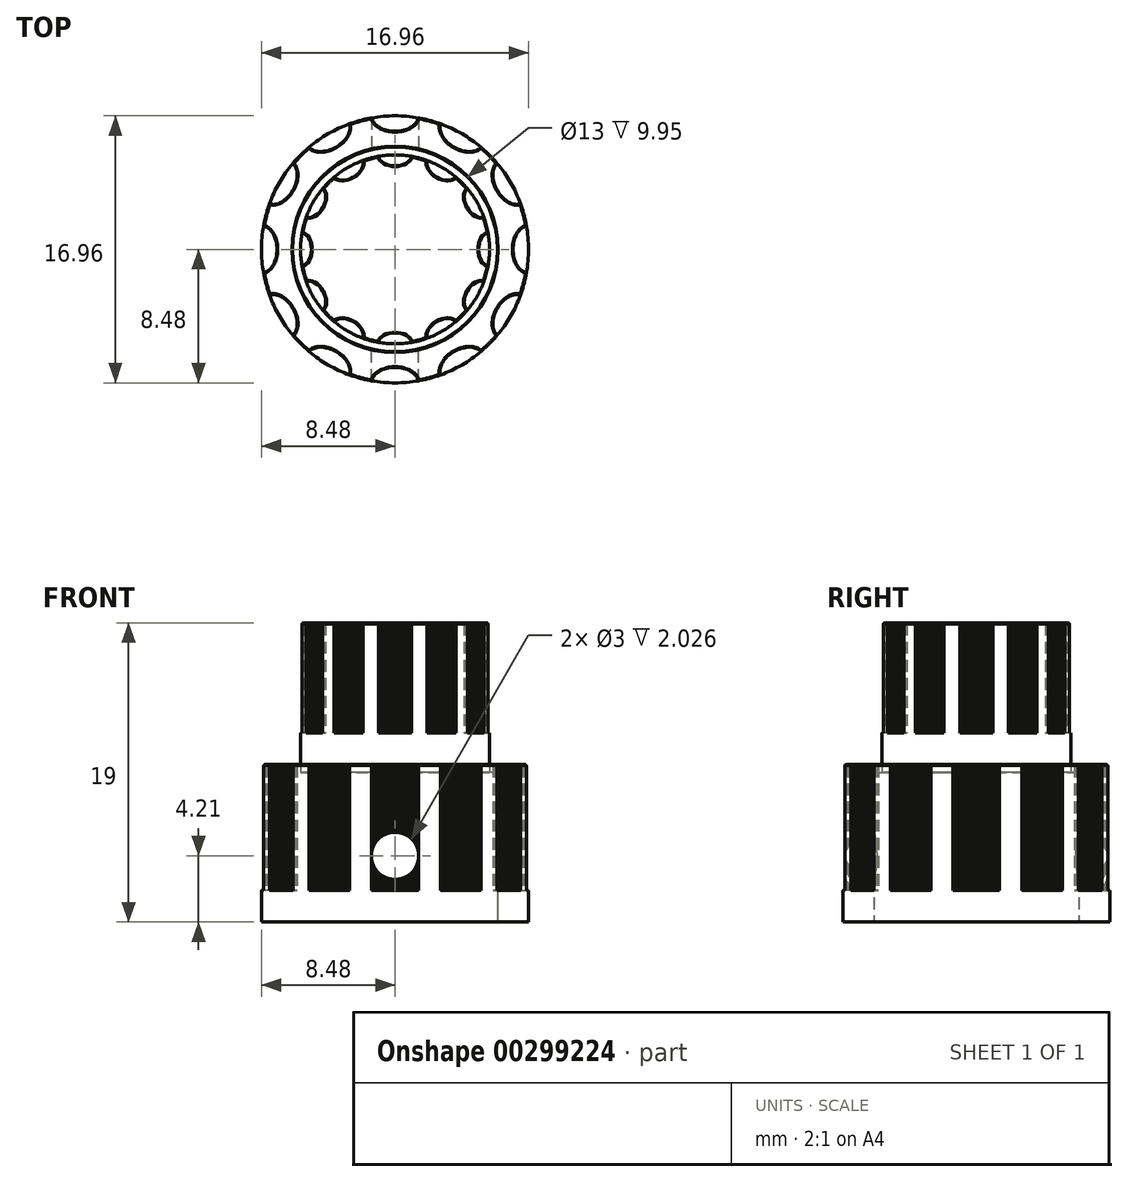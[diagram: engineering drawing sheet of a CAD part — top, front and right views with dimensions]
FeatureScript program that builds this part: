
annotation { "Feature Type Name" : "Feature", "Feature Type Description" : "" }
export const myFeature = defineFeature(function(context is Context, id is Id, definition is map)
    precondition{}
    {
        {
            var Q0;
            Q0=qCreatedBy(makeId("Top.planeOp"),FACE);
            var sketch = newSketch(context, id + "F0", { "sketchPlane" : qUnion([Q0])});
            skLineSegment(sketch, "E0", {"start": v(1.05, 5.92) * mm, "end": v(1.03, 5.86) * mm});
            skLineSegment(sketch, "E1", {"start": v(1.03, 5.86) * mm, "end": v(1, 5.8) * mm});
            skLineSegment(sketch, "E2", {"start": v(1, 5.8) * mm, "end": v(0.98, 5.74) * mm});
            skLineSegment(sketch, "E3", {"start": v(0.98, 5.74) * mm, "end": v(0.93, 5.68) * mm});
            skLineSegment(sketch, "E4", {"start": v(0.93, 5.68) * mm, "end": v(0.83, 5.57) * mm});
            skLineSegment(sketch, "E5", {"start": v(0.83, 5.57) * mm, "end": v(0.7, 5.48) * mm});
            skLineSegment(sketch, "E6", {"start": v(0.7, 5.48) * mm, "end": v(0.55, 5.4) * mm});
            skLineSegment(sketch, "E7", {"start": v(0.55, 5.4) * mm, "end": v(0.38, 5.35) * mm});
            skLineSegment(sketch, "E8", {"start": v(0.38, 5.35) * mm, "end": v(0.2, 5.32) * mm});
            skLineSegment(sketch, "E9", {"start": v(0.2, 5.32) * mm, "end": v(0, 5.3) * mm});
            skLineSegment(sketch, "E10", {"start": v(0, 5.3) * mm, "end": v(-0.2, 5.32) * mm});
            skLineSegment(sketch, "E11", {"start": v(-0.2, 5.32) * mm, "end": v(-0.38, 5.35) * mm});
            skLineSegment(sketch, "E12", {"start": v(-0.38, 5.35) * mm, "end": v(-0.55, 5.4) * mm});
            skLineSegment(sketch, "E13", {"start": v(-0.55, 5.4) * mm, "end": v(-0.7, 5.48) * mm});
            skLineSegment(sketch, "E14", {"start": v(-0.7, 5.48) * mm, "end": v(-0.83, 5.57) * mm});
            skLineSegment(sketch, "E15", {"start": v(-0.83, 5.57) * mm, "end": v(-0.93, 5.68) * mm});
            skLineSegment(sketch, "E16", {"start": v(-0.93, 5.68) * mm, "end": v(-0.98, 5.74) * mm});
            skLineSegment(sketch, "E17", {"start": v(-0.98, 5.74) * mm, "end": v(-1, 5.8) * mm});
            skLineSegment(sketch, "E18", {"start": v(-1, 5.8) * mm, "end": v(-1.03, 5.86) * mm});
            skLineSegment(sketch, "E19", {"start": v(-1.03, 5.86) * mm, "end": v(-1.05, 5.92) * mm});
            skLineSegment(sketch, "E20", {"start": v(3.87, 4.6) * mm, "end": v(3.82, 4.55) * mm});
            skLineSegment(sketch, "E21", {"start": v(3.82, 4.55) * mm, "end": v(3.77, 4.51) * mm});
            skLineSegment(sketch, "E22", {"start": v(3.77, 4.51) * mm, "end": v(3.7, 4.48) * mm});
            skLineSegment(sketch, "E23", {"start": v(3.7, 4.48) * mm, "end": v(3.64, 4.45) * mm});
            skLineSegment(sketch, "E24", {"start": v(3.64, 4.45) * mm, "end": v(3.5, 4.41) * mm});
            skLineSegment(sketch, "E25", {"start": v(3.5, 4.41) * mm, "end": v(3.35, 4.4) * mm});
            skLineSegment(sketch, "E26", {"start": v(3.35, 4.4) * mm, "end": v(3.18, 4.4) * mm});
            skLineSegment(sketch, "E27", {"start": v(3.18, 4.4) * mm, "end": v(3, 4.45) * mm});
            skLineSegment(sketch, "E28", {"start": v(3, 4.45) * mm, "end": v(2.83, 4.5) * mm});
            skLineSegment(sketch, "E29", {"start": v(2.83, 4.5) * mm, "end": v(2.65, 4.6) * mm});
            skLineSegment(sketch, "E30", {"start": v(2.65, 4.6) * mm, "end": v(2.49, 4.7) * mm});
            skLineSegment(sketch, "E31", {"start": v(2.49, 4.7) * mm, "end": v(2.35, 4.83) * mm});
            skLineSegment(sketch, "E32", {"start": v(2.35, 4.83) * mm, "end": v(2.23, 4.96) * mm});
            skLineSegment(sketch, "E33", {"start": v(2.23, 4.96) * mm, "end": v(2.13, 5.1) * mm});
            skLineSegment(sketch, "E34", {"start": v(2.13, 5.1) * mm, "end": v(2.07, 5.24) * mm});
            skLineSegment(sketch, "E35", {"start": v(2.07, 5.24) * mm, "end": v(2.03, 5.38) * mm});
            skLineSegment(sketch, "E36", {"start": v(2.03, 5.38) * mm, "end": v(2.02, 5.45) * mm});
            skLineSegment(sketch, "E37", {"start": v(2.02, 5.45) * mm, "end": v(2.02, 5.52) * mm});
            skLineSegment(sketch, "E38", {"start": v(2.02, 5.52) * mm, "end": v(2.03, 5.59) * mm});
            skLineSegment(sketch, "E39", {"start": v(2.03, 5.59) * mm, "end": v(2.05, 5.65) * mm});
            skLineSegment(sketch, "E40", {"start": v(-3.87, 4.6) * mm, "end": v(-3.82, 4.55) * mm});
            skLineSegment(sketch, "E41", {"start": v(-3.82, 4.55) * mm, "end": v(-3.77, 4.51) * mm});
            skLineSegment(sketch, "E42", {"start": v(-3.77, 4.51) * mm, "end": v(-3.7, 4.48) * mm});
            skLineSegment(sketch, "E43", {"start": v(-3.7, 4.48) * mm, "end": v(-3.64, 4.45) * mm});
            skLineSegment(sketch, "E44", {"start": v(-3.64, 4.45) * mm, "end": v(-3.5, 4.41) * mm});
            skLineSegment(sketch, "E45", {"start": v(-3.5, 4.41) * mm, "end": v(-3.35, 4.4) * mm});
            skLineSegment(sketch, "E46", {"start": v(-3.35, 4.4) * mm, "end": v(-3.18, 4.4) * mm});
            skLineSegment(sketch, "E47", {"start": v(-3.18, 4.4) * mm, "end": v(-3, 4.45) * mm});
            skLineSegment(sketch, "E48", {"start": v(-3, 4.45) * mm, "end": v(-2.83, 4.5) * mm});
            skLineSegment(sketch, "E49", {"start": v(-2.83, 4.5) * mm, "end": v(-2.65, 4.6) * mm});
            skLineSegment(sketch, "E50", {"start": v(-2.65, 4.6) * mm, "end": v(-2.49, 4.7) * mm});
            skLineSegment(sketch, "E51", {"start": v(-2.49, 4.7) * mm, "end": v(-2.35, 4.83) * mm});
            skLineSegment(sketch, "E52", {"start": v(-2.35, 4.83) * mm, "end": v(-2.23, 4.96) * mm});
            skLineSegment(sketch, "E53", {"start": v(-2.23, 4.96) * mm, "end": v(-2.13, 5.1) * mm});
            skLineSegment(sketch, "E54", {"start": v(-2.13, 5.1) * mm, "end": v(-2.07, 5.24) * mm});
            skLineSegment(sketch, "E55", {"start": v(-2.07, 5.24) * mm, "end": v(-2.03, 5.38) * mm});
            skLineSegment(sketch, "E56", {"start": v(-2.03, 5.38) * mm, "end": v(-2.02, 5.45) * mm});
            skLineSegment(sketch, "E57", {"start": v(-2.02, 5.45) * mm, "end": v(-2.02, 5.52) * mm});
            skLineSegment(sketch, "E58", {"start": v(-2.02, 5.52) * mm, "end": v(-2.03, 5.59) * mm});
            skLineSegment(sketch, "E59", {"start": v(-2.03, 5.59) * mm, "end": v(-2.05, 5.65) * mm});
            skLineSegment(sketch, "E60", {"start": v(5.65, 2.05) * mm, "end": v(5.59, 2.03) * mm});
            skLineSegment(sketch, "E61", {"start": v(5.59, 2.03) * mm, "end": v(5.52, 2.02) * mm});
            skLineSegment(sketch, "E62", {"start": v(5.52, 2.02) * mm, "end": v(5.45, 2.02) * mm});
            skLineSegment(sketch, "E63", {"start": v(5.45, 2.02) * mm, "end": v(5.38, 2.03) * mm});
            skLineSegment(sketch, "E64", {"start": v(5.38, 2.03) * mm, "end": v(5.24, 2.07) * mm});
            skLineSegment(sketch, "E65", {"start": v(5.24, 2.07) * mm, "end": v(5.1, 2.13) * mm});
            skLineSegment(sketch, "E66", {"start": v(5.1, 2.13) * mm, "end": v(4.96, 2.23) * mm});
            skLineSegment(sketch, "E67", {"start": v(4.96, 2.23) * mm, "end": v(4.83, 2.35) * mm});
            skLineSegment(sketch, "E68", {"start": v(4.83, 2.35) * mm, "end": v(4.7, 2.49) * mm});
            skLineSegment(sketch, "E69", {"start": v(4.7, 2.49) * mm, "end": v(4.6, 2.65) * mm});
            skLineSegment(sketch, "E70", {"start": v(4.6, 2.65) * mm, "end": v(4.5, 2.83) * mm});
            skLineSegment(sketch, "E71", {"start": v(4.5, 2.83) * mm, "end": v(4.45, 3) * mm});
            skLineSegment(sketch, "E72", {"start": v(4.45, 3) * mm, "end": v(4.4, 3.18) * mm});
            skLineSegment(sketch, "E73", {"start": v(4.4, 3.18) * mm, "end": v(4.4, 3.35) * mm});
            skLineSegment(sketch, "E74", {"start": v(4.4, 3.35) * mm, "end": v(4.41, 3.5) * mm});
            skLineSegment(sketch, "E75", {"start": v(4.41, 3.5) * mm, "end": v(4.45, 3.64) * mm});
            skLineSegment(sketch, "E76", {"start": v(4.45, 3.64) * mm, "end": v(4.48, 3.7) * mm});
            skLineSegment(sketch, "E77", {"start": v(4.48, 3.7) * mm, "end": v(4.51, 3.77) * mm});
            skLineSegment(sketch, "E78", {"start": v(4.51, 3.77) * mm, "end": v(4.55, 3.82) * mm});
            skLineSegment(sketch, "E79", {"start": v(4.55, 3.82) * mm, "end": v(4.6, 3.87) * mm});
            skLineSegment(sketch, "E80", {"start": v(5.92, 1.05) * mm, "end": v(5.86, 1.03) * mm});
            skLineSegment(sketch, "E81", {"start": v(5.86, 1.03) * mm, "end": v(5.8, 1) * mm});
            skLineSegment(sketch, "E82", {"start": v(5.8, 1) * mm, "end": v(5.74, 0.98) * mm});
            skLineSegment(sketch, "E83", {"start": v(5.74, 0.98) * mm, "end": v(5.68, 0.93) * mm});
            skLineSegment(sketch, "E84", {"start": v(5.68, 0.93) * mm, "end": v(5.57, 0.83) * mm});
            skLineSegment(sketch, "E85", {"start": v(5.57, 0.83) * mm, "end": v(5.48, 0.7) * mm});
            skLineSegment(sketch, "E86", {"start": v(5.48, 0.7) * mm, "end": v(5.4, 0.55) * mm});
            skLineSegment(sketch, "E87", {"start": v(5.4, 0.55) * mm, "end": v(5.35, 0.38) * mm});
            skLineSegment(sketch, "E88", {"start": v(5.35, 0.38) * mm, "end": v(5.32, 0.2) * mm});
            skLineSegment(sketch, "E89", {"start": v(5.32, 0.2) * mm, "end": v(5.3, 0) * mm});
            skLineSegment(sketch, "E90", {"start": v(5.3, 0) * mm, "end": v(5.32, -0.2) * mm});
            skLineSegment(sketch, "E91", {"start": v(5.32, -0.2) * mm, "end": v(5.35, -0.38) * mm});
            skLineSegment(sketch, "E92", {"start": v(5.35, -0.38) * mm, "end": v(5.4, -0.55) * mm});
            skLineSegment(sketch, "E93", {"start": v(5.4, -0.55) * mm, "end": v(5.48, -0.7) * mm});
            skLineSegment(sketch, "E94", {"start": v(5.48, -0.7) * mm, "end": v(5.57, -0.83) * mm});
            skLineSegment(sketch, "E95", {"start": v(5.57, -0.83) * mm, "end": v(5.68, -0.93) * mm});
            skLineSegment(sketch, "E96", {"start": v(5.68, -0.93) * mm, "end": v(5.74, -0.98) * mm});
            skLineSegment(sketch, "E97", {"start": v(5.74, -0.98) * mm, "end": v(5.8, -1) * mm});
            skLineSegment(sketch, "E98", {"start": v(5.8, -1) * mm, "end": v(5.86, -1.03) * mm});
            skLineSegment(sketch, "E99", {"start": v(5.86, -1.03) * mm, "end": v(5.92, -1.05) * mm});
            skLineSegment(sketch, "E100", {"start": v(-5.65, 2.05) * mm, "end": v(-5.59, 2.03) * mm});
            skLineSegment(sketch, "E101", {"start": v(-5.59, 2.03) * mm, "end": v(-5.52, 2.02) * mm});
            skLineSegment(sketch, "E102", {"start": v(-5.52, 2.02) * mm, "end": v(-5.45, 2.02) * mm});
            skLineSegment(sketch, "E103", {"start": v(-5.45, 2.02) * mm, "end": v(-5.38, 2.03) * mm});
            skLineSegment(sketch, "E104", {"start": v(-5.38, 2.03) * mm, "end": v(-5.24, 2.07) * mm});
            skLineSegment(sketch, "E105", {"start": v(-5.24, 2.07) * mm, "end": v(-5.1, 2.13) * mm});
            skLineSegment(sketch, "E106", {"start": v(-5.1, 2.13) * mm, "end": v(-4.96, 2.23) * mm});
            skLineSegment(sketch, "E107", {"start": v(-4.96, 2.23) * mm, "end": v(-4.83, 2.35) * mm});
            skLineSegment(sketch, "E108", {"start": v(-4.83, 2.35) * mm, "end": v(-4.7, 2.49) * mm});
            skLineSegment(sketch, "E109", {"start": v(-4.7, 2.49) * mm, "end": v(-4.6, 2.65) * mm});
            skLineSegment(sketch, "E110", {"start": v(-4.6, 2.65) * mm, "end": v(-4.5, 2.83) * mm});
            skLineSegment(sketch, "E111", {"start": v(-4.5, 2.83) * mm, "end": v(-4.45, 3) * mm});
            skLineSegment(sketch, "E112", {"start": v(-4.45, 3) * mm, "end": v(-4.4, 3.18) * mm});
            skLineSegment(sketch, "E113", {"start": v(-4.4, 3.18) * mm, "end": v(-4.4, 3.35) * mm});
            skLineSegment(sketch, "E114", {"start": v(-4.4, 3.35) * mm, "end": v(-4.41, 3.5) * mm});
            skLineSegment(sketch, "E115", {"start": v(-4.41, 3.5) * mm, "end": v(-4.45, 3.64) * mm});
            skLineSegment(sketch, "E116", {"start": v(-4.45, 3.64) * mm, "end": v(-4.48, 3.7) * mm});
            skLineSegment(sketch, "E117", {"start": v(-4.48, 3.7) * mm, "end": v(-4.51, 3.77) * mm});
            skLineSegment(sketch, "E118", {"start": v(-4.51, 3.77) * mm, "end": v(-4.55, 3.82) * mm});
            skLineSegment(sketch, "E119", {"start": v(-4.55, 3.82) * mm, "end": v(-4.6, 3.87) * mm});
            skLineSegment(sketch, "E120", {"start": v(5.65, -2.05) * mm, "end": v(5.59, -2.03) * mm});
            skLineSegment(sketch, "E121", {"start": v(5.59, -2.03) * mm, "end": v(5.52, -2.02) * mm});
            skLineSegment(sketch, "E122", {"start": v(5.52, -2.02) * mm, "end": v(5.45, -2.02) * mm});
            skLineSegment(sketch, "E123", {"start": v(5.45, -2.02) * mm, "end": v(5.38, -2.03) * mm});
            skLineSegment(sketch, "E124", {"start": v(5.38, -2.03) * mm, "end": v(5.24, -2.07) * mm});
            skLineSegment(sketch, "E125", {"start": v(5.24, -2.07) * mm, "end": v(5.1, -2.13) * mm});
            skLineSegment(sketch, "E126", {"start": v(5.1, -2.13) * mm, "end": v(4.96, -2.23) * mm});
            skLineSegment(sketch, "E127", {"start": v(4.96, -2.23) * mm, "end": v(4.83, -2.35) * mm});
            skLineSegment(sketch, "E128", {"start": v(4.83, -2.35) * mm, "end": v(4.7, -2.49) * mm});
            skLineSegment(sketch, "E129", {"start": v(4.7, -2.49) * mm, "end": v(4.6, -2.65) * mm});
            skLineSegment(sketch, "E130", {"start": v(4.6, -2.65) * mm, "end": v(4.5, -2.83) * mm});
            skLineSegment(sketch, "E131", {"start": v(4.5, -2.83) * mm, "end": v(4.45, -3) * mm});
            skLineSegment(sketch, "E132", {"start": v(4.45, -3) * mm, "end": v(4.4, -3.18) * mm});
            skLineSegment(sketch, "E133", {"start": v(4.4, -3.18) * mm, "end": v(4.4, -3.35) * mm});
            skLineSegment(sketch, "E134", {"start": v(4.4, -3.35) * mm, "end": v(4.41, -3.5) * mm});
            skLineSegment(sketch, "E135", {"start": v(4.41, -3.5) * mm, "end": v(4.45, -3.64) * mm});
            skLineSegment(sketch, "E136", {"start": v(4.45, -3.64) * mm, "end": v(4.48, -3.7) * mm});
            skLineSegment(sketch, "E137", {"start": v(4.48, -3.7) * mm, "end": v(4.51, -3.77) * mm});
            skLineSegment(sketch, "E138", {"start": v(4.51, -3.77) * mm, "end": v(4.55, -3.82) * mm});
            skLineSegment(sketch, "E139", {"start": v(4.55, -3.82) * mm, "end": v(4.6, -3.87) * mm});
            skLineSegment(sketch, "E140", {"start": v(-5.92, -1.05) * mm, "end": v(-5.86, -1.03) * mm});
            skLineSegment(sketch, "E141", {"start": v(-5.86, -1.03) * mm, "end": v(-5.8, -1) * mm});
            skLineSegment(sketch, "E142", {"start": v(-5.8, -1) * mm, "end": v(-5.74, -0.98) * mm});
            skLineSegment(sketch, "E143", {"start": v(-5.74, -0.98) * mm, "end": v(-5.68, -0.93) * mm});
            skLineSegment(sketch, "E144", {"start": v(-5.68, -0.93) * mm, "end": v(-5.57, -0.83) * mm});
            skLineSegment(sketch, "E145", {"start": v(-5.57, -0.83) * mm, "end": v(-5.48, -0.7) * mm});
            skLineSegment(sketch, "E146", {"start": v(-5.48, -0.7) * mm, "end": v(-5.4, -0.55) * mm});
            skLineSegment(sketch, "E147", {"start": v(-5.4, -0.55) * mm, "end": v(-5.35, -0.38) * mm});
            skLineSegment(sketch, "E148", {"start": v(-5.35, -0.38) * mm, "end": v(-5.32, -0.2) * mm});
            skLineSegment(sketch, "E149", {"start": v(-5.32, -0.2) * mm, "end": v(-5.3, 0) * mm});
            skLineSegment(sketch, "E150", {"start": v(-5.3, 0) * mm, "end": v(-5.32, 0.2) * mm});
            skLineSegment(sketch, "E151", {"start": v(-5.32, 0.2) * mm, "end": v(-5.35, 0.38) * mm});
            skLineSegment(sketch, "E152", {"start": v(-5.35, 0.38) * mm, "end": v(-5.4, 0.55) * mm});
            skLineSegment(sketch, "E153", {"start": v(-5.4, 0.55) * mm, "end": v(-5.48, 0.7) * mm});
            skLineSegment(sketch, "E154", {"start": v(-5.48, 0.7) * mm, "end": v(-5.57, 0.83) * mm});
            skLineSegment(sketch, "E155", {"start": v(-5.57, 0.83) * mm, "end": v(-5.68, 0.93) * mm});
            skLineSegment(sketch, "E156", {"start": v(-5.68, 0.93) * mm, "end": v(-5.74, 0.98) * mm});
            skLineSegment(sketch, "E157", {"start": v(-5.74, 0.98) * mm, "end": v(-5.8, 1) * mm});
            skLineSegment(sketch, "E158", {"start": v(-5.8, 1) * mm, "end": v(-5.86, 1.03) * mm});
            skLineSegment(sketch, "E159", {"start": v(-5.86, 1.03) * mm, "end": v(-5.92, 1.05) * mm});
            skLineSegment(sketch, "E160", {"start": v(-5.65, -2.05) * mm, "end": v(-5.59, -2.03) * mm});
            skLineSegment(sketch, "E161", {"start": v(-5.59, -2.03) * mm, "end": v(-5.52, -2.02) * mm});
            skLineSegment(sketch, "E162", {"start": v(-5.52, -2.02) * mm, "end": v(-5.45, -2.02) * mm});
            skLineSegment(sketch, "E163", {"start": v(-5.45, -2.02) * mm, "end": v(-5.38, -2.03) * mm});
            skLineSegment(sketch, "E164", {"start": v(-5.38, -2.03) * mm, "end": v(-5.24, -2.07) * mm});
            skLineSegment(sketch, "E165", {"start": v(-5.24, -2.07) * mm, "end": v(-5.1, -2.13) * mm});
            skLineSegment(sketch, "E166", {"start": v(-5.1, -2.13) * mm, "end": v(-4.96, -2.23) * mm});
            skLineSegment(sketch, "E167", {"start": v(-4.96, -2.23) * mm, "end": v(-4.83, -2.35) * mm});
            skLineSegment(sketch, "E168", {"start": v(-4.83, -2.35) * mm, "end": v(-4.7, -2.49) * mm});
            skLineSegment(sketch, "E169", {"start": v(-4.7, -2.49) * mm, "end": v(-4.6, -2.65) * mm});
            skLineSegment(sketch, "E170", {"start": v(-4.6, -2.65) * mm, "end": v(-4.5, -2.83) * mm});
            skLineSegment(sketch, "E171", {"start": v(-4.5, -2.83) * mm, "end": v(-4.45, -3) * mm});
            skLineSegment(sketch, "E172", {"start": v(-4.45, -3) * mm, "end": v(-4.4, -3.18) * mm});
            skLineSegment(sketch, "E173", {"start": v(-4.4, -3.18) * mm, "end": v(-4.4, -3.35) * mm});
            skLineSegment(sketch, "E174", {"start": v(-4.4, -3.35) * mm, "end": v(-4.41, -3.5) * mm});
            skLineSegment(sketch, "E175", {"start": v(-4.41, -3.5) * mm, "end": v(-4.45, -3.64) * mm});
            skLineSegment(sketch, "E176", {"start": v(-4.45, -3.64) * mm, "end": v(-4.48, -3.7) * mm});
            skLineSegment(sketch, "E177", {"start": v(-4.48, -3.7) * mm, "end": v(-4.51, -3.77) * mm});
            skLineSegment(sketch, "E178", {"start": v(-4.51, -3.77) * mm, "end": v(-4.55, -3.82) * mm});
            skLineSegment(sketch, "E179", {"start": v(-4.55, -3.82) * mm, "end": v(-4.6, -3.87) * mm});
            skLineSegment(sketch, "E180", {"start": v(3.87, -4.6) * mm, "end": v(3.82, -4.55) * mm});
            skLineSegment(sketch, "E181", {"start": v(3.82, -4.55) * mm, "end": v(3.77, -4.51) * mm});
            skLineSegment(sketch, "E182", {"start": v(3.77, -4.51) * mm, "end": v(3.7, -4.48) * mm});
            skLineSegment(sketch, "E183", {"start": v(3.7, -4.48) * mm, "end": v(3.64, -4.45) * mm});
            skLineSegment(sketch, "E184", {"start": v(3.64, -4.45) * mm, "end": v(3.5, -4.41) * mm});
            skLineSegment(sketch, "E185", {"start": v(3.5, -4.41) * mm, "end": v(3.35, -4.4) * mm});
            skLineSegment(sketch, "E186", {"start": v(3.35, -4.4) * mm, "end": v(3.18, -4.4) * mm});
            skLineSegment(sketch, "E187", {"start": v(3.18, -4.4) * mm, "end": v(3, -4.45) * mm});
            skLineSegment(sketch, "E188", {"start": v(3, -4.45) * mm, "end": v(2.83, -4.5) * mm});
            skLineSegment(sketch, "E189", {"start": v(2.83, -4.5) * mm, "end": v(2.65, -4.6) * mm});
            skLineSegment(sketch, "E190", {"start": v(2.65, -4.6) * mm, "end": v(2.49, -4.7) * mm});
            skLineSegment(sketch, "E191", {"start": v(2.49, -4.7) * mm, "end": v(2.35, -4.83) * mm});
            skLineSegment(sketch, "E192", {"start": v(2.35, -4.83) * mm, "end": v(2.23, -4.96) * mm});
            skLineSegment(sketch, "E193", {"start": v(2.23, -4.96) * mm, "end": v(2.13, -5.1) * mm});
            skLineSegment(sketch, "E194", {"start": v(2.13, -5.1) * mm, "end": v(2.07, -5.24) * mm});
            skLineSegment(sketch, "E195", {"start": v(2.07, -5.24) * mm, "end": v(2.03, -5.38) * mm});
            skLineSegment(sketch, "E196", {"start": v(2.03, -5.38) * mm, "end": v(2.02, -5.45) * mm});
            skLineSegment(sketch, "E197", {"start": v(2.02, -5.45) * mm, "end": v(2.02, -5.52) * mm});
            skLineSegment(sketch, "E198", {"start": v(2.02, -5.52) * mm, "end": v(2.03, -5.59) * mm});
            skLineSegment(sketch, "E199", {"start": v(2.03, -5.59) * mm, "end": v(2.05, -5.65) * mm});
            skLineSegment(sketch, "E200", {"start": v(-3.87, -4.6) * mm, "end": v(-3.82, -4.55) * mm});
            skLineSegment(sketch, "E201", {"start": v(-3.82, -4.55) * mm, "end": v(-3.77, -4.51) * mm});
            skLineSegment(sketch, "E202", {"start": v(-3.77, -4.51) * mm, "end": v(-3.7, -4.48) * mm});
            skLineSegment(sketch, "E203", {"start": v(-3.7, -4.48) * mm, "end": v(-3.64, -4.45) * mm});
            skLineSegment(sketch, "E204", {"start": v(-3.64, -4.45) * mm, "end": v(-3.5, -4.41) * mm});
            skLineSegment(sketch, "E205", {"start": v(-3.5, -4.41) * mm, "end": v(-3.35, -4.4) * mm});
            skLineSegment(sketch, "E206", {"start": v(-3.35, -4.4) * mm, "end": v(-3.18, -4.4) * mm});
            skLineSegment(sketch, "E207", {"start": v(-3.18, -4.4) * mm, "end": v(-3, -4.45) * mm});
            skLineSegment(sketch, "E208", {"start": v(-3, -4.45) * mm, "end": v(-2.83, -4.5) * mm});
            skLineSegment(sketch, "E209", {"start": v(-2.83, -4.5) * mm, "end": v(-2.65, -4.6) * mm});
            skLineSegment(sketch, "E210", {"start": v(-2.65, -4.6) * mm, "end": v(-2.49, -4.7) * mm});
            skLineSegment(sketch, "E211", {"start": v(-2.49, -4.7) * mm, "end": v(-2.35, -4.83) * mm});
            skLineSegment(sketch, "E212", {"start": v(-2.35, -4.83) * mm, "end": v(-2.23, -4.96) * mm});
            skLineSegment(sketch, "E213", {"start": v(-2.23, -4.96) * mm, "end": v(-2.13, -5.1) * mm});
            skLineSegment(sketch, "E214", {"start": v(-2.13, -5.1) * mm, "end": v(-2.07, -5.24) * mm});
            skLineSegment(sketch, "E215", {"start": v(-2.07, -5.24) * mm, "end": v(-2.03, -5.38) * mm});
            skLineSegment(sketch, "E216", {"start": v(-2.03, -5.38) * mm, "end": v(-2.02, -5.45) * mm});
            skLineSegment(sketch, "E217", {"start": v(-2.02, -5.45) * mm, "end": v(-2.02, -5.52) * mm});
            skLineSegment(sketch, "E218", {"start": v(-2.02, -5.52) * mm, "end": v(-2.03, -5.59) * mm});
            skLineSegment(sketch, "E219", {"start": v(-2.03, -5.59) * mm, "end": v(-2.05, -5.65) * mm});
            skLineSegment(sketch, "E220", {"start": v(1.05, -5.92) * mm, "end": v(1.03, -5.86) * mm});
            skLineSegment(sketch, "E221", {"start": v(1.03, -5.86) * mm, "end": v(1, -5.8) * mm});
            skLineSegment(sketch, "E222", {"start": v(1, -5.8) * mm, "end": v(0.98, -5.74) * mm});
            skLineSegment(sketch, "E223", {"start": v(0.98, -5.74) * mm, "end": v(0.93, -5.68) * mm});
            skLineSegment(sketch, "E224", {"start": v(0.93, -5.68) * mm, "end": v(0.83, -5.57) * mm});
            skLineSegment(sketch, "E225", {"start": v(0.83, -5.57) * mm, "end": v(0.7, -5.48) * mm});
            skLineSegment(sketch, "E226", {"start": v(0.7, -5.48) * mm, "end": v(0.55, -5.4) * mm});
            skLineSegment(sketch, "E227", {"start": v(0.55, -5.4) * mm, "end": v(0.38, -5.35) * mm});
            skLineSegment(sketch, "E228", {"start": v(0.38, -5.35) * mm, "end": v(0.2, -5.32) * mm});
            skLineSegment(sketch, "E229", {"start": v(0.2, -5.32) * mm, "end": v(0, -5.3) * mm});
            skLineSegment(sketch, "E230", {"start": v(0, -5.3) * mm, "end": v(-0.2, -5.32) * mm});
            skLineSegment(sketch, "E231", {"start": v(-0.2, -5.32) * mm, "end": v(-0.38, -5.35) * mm});
            skLineSegment(sketch, "E232", {"start": v(-0.38, -5.35) * mm, "end": v(-0.55, -5.4) * mm});
            skLineSegment(sketch, "E233", {"start": v(-0.55, -5.4) * mm, "end": v(-0.7, -5.48) * mm});
            skLineSegment(sketch, "E234", {"start": v(-0.7, -5.48) * mm, "end": v(-0.83, -5.57) * mm});
            skLineSegment(sketch, "E235", {"start": v(-0.83, -5.57) * mm, "end": v(-0.93, -5.68) * mm});
            skLineSegment(sketch, "E236", {"start": v(-0.93, -5.68) * mm, "end": v(-0.98, -5.74) * mm});
            skLineSegment(sketch, "E237", {"start": v(-0.98, -5.74) * mm, "end": v(-1, -5.8) * mm});
            skLineSegment(sketch, "E238", {"start": v(-1, -5.8) * mm, "end": v(-1.03, -5.86) * mm});
            skLineSegment(sketch, "E239", {"start": v(-1.03, -5.86) * mm, "end": v(-1.05, -5.92) * mm});
            skArc(sketch, "E240", {"start": v(0, 6) * mm, "mid": v(-4.24, 4.24) * mm, "end": v(-6, 0) * mm});
            skArc(sketch, "E241", {"start": v(-6, 0) * mm, "mid": v(-4.24, -4.24) * mm, "end": v(0, -6) * mm});
            skArc(sketch, "E242", {"start": v(0, -6) * mm, "mid": v(4.24, -4.24) * mm, "end": v(6, 0) * mm});
            skArc(sketch, "E243", {"start": v(6, 0) * mm, "mid": v(4.24, 4.24) * mm, "end": v(0, 6) * mm});
            skArc(sketch, "E244", {"start": v(6.5, 0) * mm, "mid": v(4.6, 4.6) * mm, "end": v(0, 6.5) * mm});
            skArc(sketch, "E245", {"start": v(0, 6.5) * mm, "mid": v(-4.6, 4.6) * mm, "end": v(-6.5, 0) * mm});
            skArc(sketch, "E246", {"start": v(-6.5, 0) * mm, "mid": v(-4.6, -4.6) * mm, "end": v(0, -6.5) * mm});
            skArc(sketch, "E247", {"start": v(0, -6.5) * mm, "mid": v(4.6, -4.6) * mm, "end": v(6.5, 0) * mm});
            skLineSegment(sketch, "E248", {"start": v(1.49, 8.37) * mm, "end": v(1.46, 8.28) * mm});
            skLineSegment(sketch, "E249", {"start": v(1.46, 8.28) * mm, "end": v(1.43, 8.19) * mm});
            skLineSegment(sketch, "E250", {"start": v(1.43, 8.19) * mm, "end": v(1.38, 8.1) * mm});
            skLineSegment(sketch, "E251", {"start": v(1.38, 8.1) * mm, "end": v(1.32, 8.03) * mm});
            skLineSegment(sketch, "E252", {"start": v(1.32, 8.03) * mm, "end": v(1.25, 7.95) * mm});
            skLineSegment(sketch, "E253", {"start": v(1.25, 7.95) * mm, "end": v(1.17, 7.88) * mm});
            skLineSegment(sketch, "E254", {"start": v(1.17, 7.88) * mm, "end": v(1.09, 7.81) * mm});
            skLineSegment(sketch, "E255", {"start": v(1.09, 7.81) * mm, "end": v(1, 7.75) * mm});
            skLineSegment(sketch, "E256", {"start": v(1, 7.75) * mm, "end": v(0.89, 7.7) * mm});
            skLineSegment(sketch, "E257", {"start": v(0.89, 7.7) * mm, "end": v(0.78, 7.65) * mm});
            skLineSegment(sketch, "E258", {"start": v(0.78, 7.65) * mm, "end": v(0.66, 7.6) * mm});
            skLineSegment(sketch, "E259", {"start": v(0.66, 7.6) * mm, "end": v(0.54, 7.57) * mm});
            skLineSegment(sketch, "E260", {"start": v(0.54, 7.57) * mm, "end": v(0.41, 7.54) * mm});
            skLineSegment(sketch, "E261", {"start": v(0.41, 7.54) * mm, "end": v(0.28, 7.52) * mm});
            skLineSegment(sketch, "E262", {"start": v(0.28, 7.52) * mm, "end": v(0.14, 7.5) * mm});
            skLineSegment(sketch, "E263", {"start": v(0.14, 7.5) * mm, "end": v(0, 7.5) * mm});
            skLineSegment(sketch, "E264", {"start": v(0, 7.5) * mm, "end": v(-0.14, 7.5) * mm});
            skLineSegment(sketch, "E265", {"start": v(-0.14, 7.5) * mm, "end": v(-0.28, 7.52) * mm});
            skLineSegment(sketch, "E266", {"start": v(-0.28, 7.52) * mm, "end": v(-0.41, 7.54) * mm});
            skLineSegment(sketch, "E267", {"start": v(-0.41, 7.54) * mm, "end": v(-0.54, 7.57) * mm});
            skLineSegment(sketch, "E268", {"start": v(-0.54, 7.57) * mm, "end": v(-0.66, 7.6) * mm});
            skLineSegment(sketch, "E269", {"start": v(-0.66, 7.6) * mm, "end": v(-0.78, 7.65) * mm});
            skLineSegment(sketch, "E270", {"start": v(-0.78, 7.65) * mm, "end": v(-0.89, 7.7) * mm});
            skLineSegment(sketch, "E271", {"start": v(-0.89, 7.7) * mm, "end": v(-1, 7.75) * mm});
            skLineSegment(sketch, "E272", {"start": v(-1, 7.75) * mm, "end": v(-1.09, 7.81) * mm});
            skLineSegment(sketch, "E273", {"start": v(-1.09, 7.81) * mm, "end": v(-1.17, 7.88) * mm});
            skLineSegment(sketch, "E274", {"start": v(-1.17, 7.88) * mm, "end": v(-1.25, 7.95) * mm});
            skLineSegment(sketch, "E275", {"start": v(-1.25, 7.95) * mm, "end": v(-1.32, 8.03) * mm});
            skLineSegment(sketch, "E276", {"start": v(-1.32, 8.03) * mm, "end": v(-1.38, 8.1) * mm});
            skLineSegment(sketch, "E277", {"start": v(-1.38, 8.1) * mm, "end": v(-1.43, 8.19) * mm});
            skLineSegment(sketch, "E278", {"start": v(-1.43, 8.19) * mm, "end": v(-1.46, 8.28) * mm});
            skLineSegment(sketch, "E279", {"start": v(-1.46, 8.28) * mm, "end": v(-1.49, 8.37) * mm});
            skLineSegment(sketch, "E280", {"start": v(5.47, 6.5) * mm, "end": v(5.4, 6.43) * mm});
            skLineSegment(sketch, "E281", {"start": v(5.4, 6.43) * mm, "end": v(5.32, 6.38) * mm});
            skLineSegment(sketch, "E282", {"start": v(5.32, 6.38) * mm, "end": v(5.24, 6.33) * mm});
            skLineSegment(sketch, "E283", {"start": v(5.24, 6.33) * mm, "end": v(5.15, 6.29) * mm});
            skLineSegment(sketch, "E284", {"start": v(5.15, 6.29) * mm, "end": v(5.05, 6.26) * mm});
            skLineSegment(sketch, "E285", {"start": v(5.05, 6.26) * mm, "end": v(4.95, 6.23) * mm});
            skLineSegment(sketch, "E286", {"start": v(4.95, 6.23) * mm, "end": v(4.84, 6.22) * mm});
            skLineSegment(sketch, "E287", {"start": v(4.84, 6.22) * mm, "end": v(4.73, 6.22) * mm});
            skLineSegment(sketch, "E288", {"start": v(4.73, 6.22) * mm, "end": v(4.61, 6.22) * mm});
            skLineSegment(sketch, "E289", {"start": v(4.61, 6.22) * mm, "end": v(4.5, 6.23) * mm});
            skLineSegment(sketch, "E290", {"start": v(4.5, 6.23) * mm, "end": v(4.37, 6.25) * mm});
            skLineSegment(sketch, "E291", {"start": v(4.37, 6.25) * mm, "end": v(4.25, 6.28) * mm});
            skLineSegment(sketch, "E292", {"start": v(4.25, 6.28) * mm, "end": v(4.12, 6.32) * mm});
            skLineSegment(sketch, "E293", {"start": v(4.12, 6.32) * mm, "end": v(4, 6.37) * mm});
            skLineSegment(sketch, "E294", {"start": v(4, 6.37) * mm, "end": v(3.87, 6.43) * mm});
            skLineSegment(sketch, "E295", {"start": v(3.87, 6.43) * mm, "end": v(3.75, 6.5) * mm});
            skLineSegment(sketch, "E296", {"start": v(3.75, 6.5) * mm, "end": v(3.63, 6.57) * mm});
            skLineSegment(sketch, "E297", {"start": v(3.63, 6.57) * mm, "end": v(3.52, 6.65) * mm});
            skLineSegment(sketch, "E298", {"start": v(3.52, 6.65) * mm, "end": v(3.41, 6.73) * mm});
            skLineSegment(sketch, "E299", {"start": v(3.41, 6.73) * mm, "end": v(3.32, 6.82) * mm});
            skLineSegment(sketch, "E300", {"start": v(3.32, 6.82) * mm, "end": v(3.23, 6.92) * mm});
            skLineSegment(sketch, "E301", {"start": v(3.23, 6.92) * mm, "end": v(3.15, 7.01) * mm});
            skLineSegment(sketch, "E302", {"start": v(3.15, 7.01) * mm, "end": v(3.08, 7.1) * mm});
            skLineSegment(sketch, "E303", {"start": v(3.08, 7.1) * mm, "end": v(3.02, 7.2) * mm});
            skLineSegment(sketch, "E304", {"start": v(3.02, 7.2) * mm, "end": v(2.96, 7.3) * mm});
            skLineSegment(sketch, "E305", {"start": v(2.96, 7.3) * mm, "end": v(2.92, 7.4) * mm});
            skLineSegment(sketch, "E306", {"start": v(2.92, 7.4) * mm, "end": v(2.9, 7.5) * mm});
            skLineSegment(sketch, "E307", {"start": v(2.9, 7.5) * mm, "end": v(2.87, 7.6) * mm});
            skLineSegment(sketch, "E308", {"start": v(2.87, 7.6) * mm, "end": v(2.86, 7.7) * mm});
            skLineSegment(sketch, "E309", {"start": v(2.86, 7.7) * mm, "end": v(2.86, 7.8) * mm});
            skLineSegment(sketch, "E310", {"start": v(2.86, 7.8) * mm, "end": v(2.87, 7.9) * mm});
            skLineSegment(sketch, "E311", {"start": v(2.87, 7.9) * mm, "end": v(2.9, 7.99) * mm});
            skLineSegment(sketch, "E312", {"start": v(-5.47, 6.5) * mm, "end": v(-5.4, 6.43) * mm});
            skLineSegment(sketch, "E313", {"start": v(-5.4, 6.43) * mm, "end": v(-5.32, 6.38) * mm});
            skLineSegment(sketch, "E314", {"start": v(-5.32, 6.38) * mm, "end": v(-5.24, 6.33) * mm});
            skLineSegment(sketch, "E315", {"start": v(-5.24, 6.33) * mm, "end": v(-5.15, 6.29) * mm});
            skLineSegment(sketch, "E316", {"start": v(-5.15, 6.29) * mm, "end": v(-5.05, 6.26) * mm});
            skLineSegment(sketch, "E317", {"start": v(-5.05, 6.26) * mm, "end": v(-4.95, 6.23) * mm});
            skLineSegment(sketch, "E318", {"start": v(-4.95, 6.23) * mm, "end": v(-4.84, 6.22) * mm});
            skLineSegment(sketch, "E319", {"start": v(-4.84, 6.22) * mm, "end": v(-4.73, 6.22) * mm});
            skLineSegment(sketch, "E320", {"start": v(-4.73, 6.22) * mm, "end": v(-4.61, 6.22) * mm});
            skLineSegment(sketch, "E321", {"start": v(-4.61, 6.22) * mm, "end": v(-4.5, 6.23) * mm});
            skLineSegment(sketch, "E322", {"start": v(-4.5, 6.23) * mm, "end": v(-4.37, 6.25) * mm});
            skLineSegment(sketch, "E323", {"start": v(-4.37, 6.25) * mm, "end": v(-4.25, 6.28) * mm});
            skLineSegment(sketch, "E324", {"start": v(-4.25, 6.28) * mm, "end": v(-4.12, 6.32) * mm});
            skLineSegment(sketch, "E325", {"start": v(-4.12, 6.32) * mm, "end": v(-4, 6.37) * mm});
            skLineSegment(sketch, "E326", {"start": v(-4, 6.37) * mm, "end": v(-3.87, 6.43) * mm});
            skLineSegment(sketch, "E327", {"start": v(-3.87, 6.43) * mm, "end": v(-3.75, 6.5) * mm});
            skLineSegment(sketch, "E328", {"start": v(-3.75, 6.5) * mm, "end": v(-3.63, 6.57) * mm});
            skLineSegment(sketch, "E329", {"start": v(-3.63, 6.57) * mm, "end": v(-3.52, 6.65) * mm});
            skLineSegment(sketch, "E330", {"start": v(-3.52, 6.65) * mm, "end": v(-3.41, 6.73) * mm});
            skLineSegment(sketch, "E331", {"start": v(-3.41, 6.73) * mm, "end": v(-3.32, 6.82) * mm});
            skLineSegment(sketch, "E332", {"start": v(-3.32, 6.82) * mm, "end": v(-3.23, 6.92) * mm});
            skLineSegment(sketch, "E333", {"start": v(-3.23, 6.92) * mm, "end": v(-3.15, 7.01) * mm});
            skLineSegment(sketch, "E334", {"start": v(-3.15, 7.01) * mm, "end": v(-3.08, 7.1) * mm});
            skLineSegment(sketch, "E335", {"start": v(-3.08, 7.1) * mm, "end": v(-3.02, 7.2) * mm});
            skLineSegment(sketch, "E336", {"start": v(-3.02, 7.2) * mm, "end": v(-2.96, 7.3) * mm});
            skLineSegment(sketch, "E337", {"start": v(-2.96, 7.3) * mm, "end": v(-2.92, 7.4) * mm});
            skLineSegment(sketch, "E338", {"start": v(-2.92, 7.4) * mm, "end": v(-2.9, 7.5) * mm});
            skLineSegment(sketch, "E339", {"start": v(-2.9, 7.5) * mm, "end": v(-2.87, 7.6) * mm});
            skLineSegment(sketch, "E340", {"start": v(-2.87, 7.6) * mm, "end": v(-2.86, 7.7) * mm});
            skLineSegment(sketch, "E341", {"start": v(-2.86, 7.7) * mm, "end": v(-2.86, 7.8) * mm});
            skLineSegment(sketch, "E342", {"start": v(-2.86, 7.8) * mm, "end": v(-2.87, 7.9) * mm});
            skLineSegment(sketch, "E343", {"start": v(-2.87, 7.9) * mm, "end": v(-2.9, 7.99) * mm});
            skLineSegment(sketch, "E344", {"start": v(7.99, 2.9) * mm, "end": v(7.9, 2.87) * mm});
            skLineSegment(sketch, "E345", {"start": v(7.9, 2.87) * mm, "end": v(7.8, 2.86) * mm});
            skLineSegment(sketch, "E346", {"start": v(7.8, 2.86) * mm, "end": v(7.7, 2.86) * mm});
            skLineSegment(sketch, "E347", {"start": v(7.7, 2.86) * mm, "end": v(7.6, 2.87) * mm});
            skLineSegment(sketch, "E348", {"start": v(7.6, 2.87) * mm, "end": v(7.5, 2.9) * mm});
            skLineSegment(sketch, "E349", {"start": v(7.5, 2.9) * mm, "end": v(7.4, 2.92) * mm});
            skLineSegment(sketch, "E350", {"start": v(7.4, 2.92) * mm, "end": v(7.3, 2.96) * mm});
            skLineSegment(sketch, "E351", {"start": v(7.3, 2.96) * mm, "end": v(7.2, 3.02) * mm});
            skLineSegment(sketch, "E352", {"start": v(7.2, 3.02) * mm, "end": v(7.1, 3.08) * mm});
            skLineSegment(sketch, "E353", {"start": v(7.1, 3.08) * mm, "end": v(7.01, 3.15) * mm});
            skLineSegment(sketch, "E354", {"start": v(7.01, 3.15) * mm, "end": v(6.92, 3.23) * mm});
            skLineSegment(sketch, "E355", {"start": v(6.92, 3.23) * mm, "end": v(6.82, 3.32) * mm});
            skLineSegment(sketch, "E356", {"start": v(6.82, 3.32) * mm, "end": v(6.73, 3.41) * mm});
            skLineSegment(sketch, "E357", {"start": v(6.73, 3.41) * mm, "end": v(6.65, 3.52) * mm});
            skLineSegment(sketch, "E358", {"start": v(6.65, 3.52) * mm, "end": v(6.57, 3.63) * mm});
            skLineSegment(sketch, "E359", {"start": v(6.57, 3.63) * mm, "end": v(6.5, 3.75) * mm});
            skLineSegment(sketch, "E360", {"start": v(6.5, 3.75) * mm, "end": v(6.43, 3.87) * mm});
            skLineSegment(sketch, "E361", {"start": v(6.43, 3.87) * mm, "end": v(6.37, 4) * mm});
            skLineSegment(sketch, "E362", {"start": v(6.37, 4) * mm, "end": v(6.32, 4.12) * mm});
            skLineSegment(sketch, "E363", {"start": v(6.32, 4.12) * mm, "end": v(6.28, 4.25) * mm});
            skLineSegment(sketch, "E364", {"start": v(6.28, 4.25) * mm, "end": v(6.25, 4.37) * mm});
            skLineSegment(sketch, "E365", {"start": v(6.25, 4.37) * mm, "end": v(6.23, 4.5) * mm});
            skLineSegment(sketch, "E366", {"start": v(6.23, 4.5) * mm, "end": v(6.22, 4.61) * mm});
            skLineSegment(sketch, "E367", {"start": v(6.22, 4.61) * mm, "end": v(6.22, 4.73) * mm});
            skLineSegment(sketch, "E368", {"start": v(6.22, 4.73) * mm, "end": v(6.22, 4.84) * mm});
            skLineSegment(sketch, "E369", {"start": v(6.22, 4.84) * mm, "end": v(6.23, 4.95) * mm});
            skLineSegment(sketch, "E370", {"start": v(6.23, 4.95) * mm, "end": v(6.26, 5.05) * mm});
            skLineSegment(sketch, "E371", {"start": v(6.26, 5.05) * mm, "end": v(6.29, 5.15) * mm});
            skLineSegment(sketch, "E372", {"start": v(6.29, 5.15) * mm, "end": v(6.33, 5.24) * mm});
            skLineSegment(sketch, "E373", {"start": v(6.33, 5.24) * mm, "end": v(6.38, 5.32) * mm});
            skLineSegment(sketch, "E374", {"start": v(6.38, 5.32) * mm, "end": v(6.43, 5.4) * mm});
            skLineSegment(sketch, "E375", {"start": v(6.43, 5.4) * mm, "end": v(6.5, 5.47) * mm});
            skLineSegment(sketch, "E376", {"start": v(8.37, 1.49) * mm, "end": v(8.28, 1.46) * mm});
            skLineSegment(sketch, "E377", {"start": v(8.28, 1.46) * mm, "end": v(8.19, 1.43) * mm});
            skLineSegment(sketch, "E378", {"start": v(8.19, 1.43) * mm, "end": v(8.1, 1.38) * mm});
            skLineSegment(sketch, "E379", {"start": v(8.1, 1.38) * mm, "end": v(8.03, 1.32) * mm});
            skLineSegment(sketch, "E380", {"start": v(8.03, 1.32) * mm, "end": v(7.95, 1.25) * mm});
            skLineSegment(sketch, "E381", {"start": v(7.95, 1.25) * mm, "end": v(7.88, 1.17) * mm});
            skLineSegment(sketch, "E382", {"start": v(7.88, 1.17) * mm, "end": v(7.81, 1.09) * mm});
            skLineSegment(sketch, "E383", {"start": v(7.81, 1.09) * mm, "end": v(7.75, 1) * mm});
            skLineSegment(sketch, "E384", {"start": v(7.75, 1) * mm, "end": v(7.7, 0.89) * mm});
            skLineSegment(sketch, "E385", {"start": v(7.7, 0.89) * mm, "end": v(7.65, 0.78) * mm});
            skLineSegment(sketch, "E386", {"start": v(7.65, 0.78) * mm, "end": v(7.6, 0.66) * mm});
            skLineSegment(sketch, "E387", {"start": v(7.6, 0.66) * mm, "end": v(7.57, 0.54) * mm});
            skLineSegment(sketch, "E388", {"start": v(7.57, 0.54) * mm, "end": v(7.54, 0.41) * mm});
            skLineSegment(sketch, "E389", {"start": v(7.54, 0.41) * mm, "end": v(7.52, 0.28) * mm});
            skLineSegment(sketch, "E390", {"start": v(7.52, 0.28) * mm, "end": v(7.5, 0.14) * mm});
            skLineSegment(sketch, "E391", {"start": v(7.5, 0.14) * mm, "end": v(7.5, 0) * mm});
            skLineSegment(sketch, "E392", {"start": v(7.5, 0) * mm, "end": v(7.5, -0.14) * mm});
            skLineSegment(sketch, "E393", {"start": v(7.5, -0.14) * mm, "end": v(7.52, -0.28) * mm});
            skLineSegment(sketch, "E394", {"start": v(7.52, -0.28) * mm, "end": v(7.54, -0.41) * mm});
            skLineSegment(sketch, "E395", {"start": v(7.54, -0.41) * mm, "end": v(7.57, -0.54) * mm});
            skLineSegment(sketch, "E396", {"start": v(7.57, -0.54) * mm, "end": v(7.6, -0.66) * mm});
            skLineSegment(sketch, "E397", {"start": v(7.6, -0.66) * mm, "end": v(7.65, -0.78) * mm});
            skLineSegment(sketch, "E398", {"start": v(7.65, -0.78) * mm, "end": v(7.7, -0.89) * mm});
            skLineSegment(sketch, "E399", {"start": v(7.7, -0.89) * mm, "end": v(7.75, -1) * mm});
            skLineSegment(sketch, "E400", {"start": v(7.75, -1) * mm, "end": v(7.81, -1.09) * mm});
            skLineSegment(sketch, "E401", {"start": v(7.81, -1.09) * mm, "end": v(7.88, -1.17) * mm});
            skLineSegment(sketch, "E402", {"start": v(7.88, -1.17) * mm, "end": v(7.95, -1.25) * mm});
            skLineSegment(sketch, "E403", {"start": v(7.95, -1.25) * mm, "end": v(8.03, -1.32) * mm});
            skLineSegment(sketch, "E404", {"start": v(8.03, -1.32) * mm, "end": v(8.1, -1.38) * mm});
            skLineSegment(sketch, "E405", {"start": v(8.1, -1.38) * mm, "end": v(8.19, -1.43) * mm});
            skLineSegment(sketch, "E406", {"start": v(8.19, -1.43) * mm, "end": v(8.28, -1.46) * mm});
            skLineSegment(sketch, "E407", {"start": v(8.28, -1.46) * mm, "end": v(8.37, -1.49) * mm});
            skLineSegment(sketch, "E408", {"start": v(-7.99, 2.9) * mm, "end": v(-7.9, 2.87) * mm});
            skLineSegment(sketch, "E409", {"start": v(-7.9, 2.87) * mm, "end": v(-7.8, 2.86) * mm});
            skLineSegment(sketch, "E410", {"start": v(-7.8, 2.86) * mm, "end": v(-7.7, 2.86) * mm});
            skLineSegment(sketch, "E411", {"start": v(-7.7, 2.86) * mm, "end": v(-7.6, 2.87) * mm});
            skLineSegment(sketch, "E412", {"start": v(-7.6, 2.87) * mm, "end": v(-7.5, 2.9) * mm});
            skLineSegment(sketch, "E413", {"start": v(-7.5, 2.9) * mm, "end": v(-7.4, 2.92) * mm});
            skLineSegment(sketch, "E414", {"start": v(-7.4, 2.92) * mm, "end": v(-7.3, 2.96) * mm});
            skLineSegment(sketch, "E415", {"start": v(-7.3, 2.96) * mm, "end": v(-7.2, 3.02) * mm});
            skLineSegment(sketch, "E416", {"start": v(-7.2, 3.02) * mm, "end": v(-7.1, 3.08) * mm});
            skLineSegment(sketch, "E417", {"start": v(-7.1, 3.08) * mm, "end": v(-7.01, 3.15) * mm});
            skLineSegment(sketch, "E418", {"start": v(-7.01, 3.15) * mm, "end": v(-6.92, 3.23) * mm});
            skLineSegment(sketch, "E419", {"start": v(-6.92, 3.23) * mm, "end": v(-6.82, 3.32) * mm});
            skLineSegment(sketch, "E420", {"start": v(-6.82, 3.32) * mm, "end": v(-6.73, 3.41) * mm});
            skLineSegment(sketch, "E421", {"start": v(-6.73, 3.41) * mm, "end": v(-6.65, 3.52) * mm});
            skLineSegment(sketch, "E422", {"start": v(-6.65, 3.52) * mm, "end": v(-6.57, 3.63) * mm});
            skLineSegment(sketch, "E423", {"start": v(-6.57, 3.63) * mm, "end": v(-6.5, 3.75) * mm});
            skLineSegment(sketch, "E424", {"start": v(-6.5, 3.75) * mm, "end": v(-6.43, 3.87) * mm});
            skLineSegment(sketch, "E425", {"start": v(-6.43, 3.87) * mm, "end": v(-6.37, 4) * mm});
            skLineSegment(sketch, "E426", {"start": v(-6.37, 4) * mm, "end": v(-6.32, 4.12) * mm});
            skLineSegment(sketch, "E427", {"start": v(-6.32, 4.12) * mm, "end": v(-6.28, 4.25) * mm});
            skLineSegment(sketch, "E428", {"start": v(-6.28, 4.25) * mm, "end": v(-6.25, 4.37) * mm});
            skLineSegment(sketch, "E429", {"start": v(-6.25, 4.37) * mm, "end": v(-6.23, 4.5) * mm});
            skLineSegment(sketch, "E430", {"start": v(-6.23, 4.5) * mm, "end": v(-6.22, 4.61) * mm});
            skLineSegment(sketch, "E431", {"start": v(-6.22, 4.61) * mm, "end": v(-6.22, 4.73) * mm});
            skLineSegment(sketch, "E432", {"start": v(-6.22, 4.73) * mm, "end": v(-6.22, 4.84) * mm});
            skLineSegment(sketch, "E433", {"start": v(-6.22, 4.84) * mm, "end": v(-6.23, 4.95) * mm});
            skLineSegment(sketch, "E434", {"start": v(-6.23, 4.95) * mm, "end": v(-6.26, 5.05) * mm});
            skLineSegment(sketch, "E435", {"start": v(-6.26, 5.05) * mm, "end": v(-6.29, 5.15) * mm});
            skLineSegment(sketch, "E436", {"start": v(-6.29, 5.15) * mm, "end": v(-6.33, 5.24) * mm});
            skLineSegment(sketch, "E437", {"start": v(-6.33, 5.24) * mm, "end": v(-6.38, 5.32) * mm});
            skLineSegment(sketch, "E438", {"start": v(-6.38, 5.32) * mm, "end": v(-6.43, 5.4) * mm});
            skLineSegment(sketch, "E439", {"start": v(-6.43, 5.4) * mm, "end": v(-6.5, 5.47) * mm});
            skLineSegment(sketch, "E440", {"start": v(7.99, -2.9) * mm, "end": v(7.9, -2.87) * mm});
            skLineSegment(sketch, "E441", {"start": v(7.9, -2.87) * mm, "end": v(7.8, -2.86) * mm});
            skLineSegment(sketch, "E442", {"start": v(7.8, -2.86) * mm, "end": v(7.7, -2.86) * mm});
            skLineSegment(sketch, "E443", {"start": v(7.7, -2.86) * mm, "end": v(7.6, -2.87) * mm});
            skLineSegment(sketch, "E444", {"start": v(7.6, -2.87) * mm, "end": v(7.5, -2.9) * mm});
            skLineSegment(sketch, "E445", {"start": v(7.5, -2.9) * mm, "end": v(7.4, -2.92) * mm});
            skLineSegment(sketch, "E446", {"start": v(7.4, -2.92) * mm, "end": v(7.3, -2.96) * mm});
            skLineSegment(sketch, "E447", {"start": v(7.3, -2.96) * mm, "end": v(7.2, -3.02) * mm});
            skLineSegment(sketch, "E448", {"start": v(7.2, -3.02) * mm, "end": v(7.1, -3.08) * mm});
            skLineSegment(sketch, "E449", {"start": v(7.1, -3.08) * mm, "end": v(7.01, -3.15) * mm});
            skLineSegment(sketch, "E450", {"start": v(7.01, -3.15) * mm, "end": v(6.92, -3.23) * mm});
            skLineSegment(sketch, "E451", {"start": v(6.92, -3.23) * mm, "end": v(6.82, -3.32) * mm});
            skLineSegment(sketch, "E452", {"start": v(6.82, -3.32) * mm, "end": v(6.73, -3.41) * mm});
            skLineSegment(sketch, "E453", {"start": v(6.73, -3.41) * mm, "end": v(6.65, -3.52) * mm});
            skLineSegment(sketch, "E454", {"start": v(6.65, -3.52) * mm, "end": v(6.57, -3.63) * mm});
            skLineSegment(sketch, "E455", {"start": v(6.57, -3.63) * mm, "end": v(6.5, -3.75) * mm});
            skLineSegment(sketch, "E456", {"start": v(6.5, -3.75) * mm, "end": v(6.43, -3.87) * mm});
            skLineSegment(sketch, "E457", {"start": v(6.43, -3.87) * mm, "end": v(6.37, -4) * mm});
            skLineSegment(sketch, "E458", {"start": v(6.37, -4) * mm, "end": v(6.32, -4.12) * mm});
            skLineSegment(sketch, "E459", {"start": v(6.32, -4.12) * mm, "end": v(6.28, -4.25) * mm});
            skLineSegment(sketch, "E460", {"start": v(6.28, -4.25) * mm, "end": v(6.25, -4.37) * mm});
            skLineSegment(sketch, "E461", {"start": v(6.25, -4.37) * mm, "end": v(6.23, -4.5) * mm});
            skLineSegment(sketch, "E462", {"start": v(6.23, -4.5) * mm, "end": v(6.22, -4.61) * mm});
            skLineSegment(sketch, "E463", {"start": v(6.22, -4.61) * mm, "end": v(6.22, -4.73) * mm});
            skLineSegment(sketch, "E464", {"start": v(6.22, -4.73) * mm, "end": v(6.22, -4.84) * mm});
            skLineSegment(sketch, "E465", {"start": v(6.22, -4.84) * mm, "end": v(6.23, -4.95) * mm});
            skLineSegment(sketch, "E466", {"start": v(6.23, -4.95) * mm, "end": v(6.26, -5.05) * mm});
            skLineSegment(sketch, "E467", {"start": v(6.26, -5.05) * mm, "end": v(6.29, -5.15) * mm});
            skLineSegment(sketch, "E468", {"start": v(6.29, -5.15) * mm, "end": v(6.33, -5.24) * mm});
            skLineSegment(sketch, "E469", {"start": v(6.33, -5.24) * mm, "end": v(6.38, -5.32) * mm});
            skLineSegment(sketch, "E470", {"start": v(6.38, -5.32) * mm, "end": v(6.43, -5.4) * mm});
            skLineSegment(sketch, "E471", {"start": v(6.43, -5.4) * mm, "end": v(6.5, -5.47) * mm});
            skLineSegment(sketch, "E472", {"start": v(-8.37, -1.49) * mm, "end": v(-8.28, -1.46) * mm});
            skLineSegment(sketch, "E473", {"start": v(-8.28, -1.46) * mm, "end": v(-8.19, -1.43) * mm});
            skLineSegment(sketch, "E474", {"start": v(-8.19, -1.43) * mm, "end": v(-8.1, -1.38) * mm});
            skLineSegment(sketch, "E475", {"start": v(-8.1, -1.38) * mm, "end": v(-8.03, -1.32) * mm});
            skLineSegment(sketch, "E476", {"start": v(-8.03, -1.32) * mm, "end": v(-7.95, -1.25) * mm});
            skLineSegment(sketch, "E477", {"start": v(-7.95, -1.25) * mm, "end": v(-7.88, -1.17) * mm});
            skLineSegment(sketch, "E478", {"start": v(-7.88, -1.17) * mm, "end": v(-7.81, -1.09) * mm});
            skLineSegment(sketch, "E479", {"start": v(-7.81, -1.09) * mm, "end": v(-7.75, -1) * mm});
            skLineSegment(sketch, "E480", {"start": v(-7.75, -1) * mm, "end": v(-7.7, -0.89) * mm});
            skLineSegment(sketch, "E481", {"start": v(-7.7, -0.89) * mm, "end": v(-7.65, -0.78) * mm});
            skLineSegment(sketch, "E482", {"start": v(-7.65, -0.78) * mm, "end": v(-7.6, -0.66) * mm});
            skLineSegment(sketch, "E483", {"start": v(-7.6, -0.66) * mm, "end": v(-7.57, -0.54) * mm});
            skLineSegment(sketch, "E484", {"start": v(-7.57, -0.54) * mm, "end": v(-7.54, -0.41) * mm});
            skLineSegment(sketch, "E485", {"start": v(-7.54, -0.41) * mm, "end": v(-7.52, -0.28) * mm});
            skLineSegment(sketch, "E486", {"start": v(-7.52, -0.28) * mm, "end": v(-7.5, -0.14) * mm});
            skLineSegment(sketch, "E487", {"start": v(-7.5, -0.14) * mm, "end": v(-7.5, 0) * mm});
            skLineSegment(sketch, "E488", {"start": v(-7.5, 0) * mm, "end": v(-7.5, 0.14) * mm});
            skLineSegment(sketch, "E489", {"start": v(-7.5, 0.14) * mm, "end": v(-7.52, 0.28) * mm});
            skLineSegment(sketch, "E490", {"start": v(-7.52, 0.28) * mm, "end": v(-7.54, 0.41) * mm});
            skLineSegment(sketch, "E491", {"start": v(-7.54, 0.41) * mm, "end": v(-7.57, 0.54) * mm});
            skLineSegment(sketch, "E492", {"start": v(-7.57, 0.54) * mm, "end": v(-7.6, 0.66) * mm});
            skLineSegment(sketch, "E493", {"start": v(-7.6, 0.66) * mm, "end": v(-7.65, 0.78) * mm});
            skLineSegment(sketch, "E494", {"start": v(-7.65, 0.78) * mm, "end": v(-7.7, 0.89) * mm});
            skLineSegment(sketch, "E495", {"start": v(-7.7, 0.89) * mm, "end": v(-7.75, 1) * mm});
            skLineSegment(sketch, "E496", {"start": v(-7.75, 1) * mm, "end": v(-7.81, 1.09) * mm});
            skLineSegment(sketch, "E497", {"start": v(-7.81, 1.09) * mm, "end": v(-7.88, 1.17) * mm});
            skLineSegment(sketch, "E498", {"start": v(-7.88, 1.17) * mm, "end": v(-7.95, 1.25) * mm});
            skLineSegment(sketch, "E499", {"start": v(-7.95, 1.25) * mm, "end": v(-8.03, 1.32) * mm});
            skLineSegment(sketch, "E500", {"start": v(-8.03, 1.32) * mm, "end": v(-8.1, 1.38) * mm});
            skLineSegment(sketch, "E501", {"start": v(-8.1, 1.38) * mm, "end": v(-8.19, 1.43) * mm});
            skLineSegment(sketch, "E502", {"start": v(-8.19, 1.43) * mm, "end": v(-8.28, 1.46) * mm});
            skLineSegment(sketch, "E503", {"start": v(-8.28, 1.46) * mm, "end": v(-8.37, 1.49) * mm});
            skLineSegment(sketch, "E504", {"start": v(-7.99, -2.9) * mm, "end": v(-7.9, -2.87) * mm});
            skLineSegment(sketch, "E505", {"start": v(-7.9, -2.87) * mm, "end": v(-7.8, -2.86) * mm});
            skLineSegment(sketch, "E506", {"start": v(-7.8, -2.86) * mm, "end": v(-7.7, -2.86) * mm});
            skLineSegment(sketch, "E507", {"start": v(-7.7, -2.86) * mm, "end": v(-7.6, -2.87) * mm});
            skLineSegment(sketch, "E508", {"start": v(-7.6, -2.87) * mm, "end": v(-7.5, -2.9) * mm});
            skLineSegment(sketch, "E509", {"start": v(-7.5, -2.9) * mm, "end": v(-7.4, -2.92) * mm});
            skLineSegment(sketch, "E510", {"start": v(-7.4, -2.92) * mm, "end": v(-7.3, -2.96) * mm});
            skLineSegment(sketch, "E511", {"start": v(-7.3, -2.96) * mm, "end": v(-7.2, -3.02) * mm});
            skLineSegment(sketch, "E512", {"start": v(-7.2, -3.02) * mm, "end": v(-7.1, -3.08) * mm});
            skLineSegment(sketch, "E513", {"start": v(-7.1, -3.08) * mm, "end": v(-7.01, -3.15) * mm});
            skLineSegment(sketch, "E514", {"start": v(-7.01, -3.15) * mm, "end": v(-6.92, -3.23) * mm});
            skLineSegment(sketch, "E515", {"start": v(-6.92, -3.23) * mm, "end": v(-6.82, -3.32) * mm});
            skLineSegment(sketch, "E516", {"start": v(-6.82, -3.32) * mm, "end": v(-6.73, -3.41) * mm});
            skLineSegment(sketch, "E517", {"start": v(-6.73, -3.41) * mm, "end": v(-6.65, -3.52) * mm});
            skLineSegment(sketch, "E518", {"start": v(-6.65, -3.52) * mm, "end": v(-6.57, -3.63) * mm});
            skLineSegment(sketch, "E519", {"start": v(-6.57, -3.63) * mm, "end": v(-6.5, -3.75) * mm});
            skLineSegment(sketch, "E520", {"start": v(-6.5, -3.75) * mm, "end": v(-6.43, -3.87) * mm});
            skLineSegment(sketch, "E521", {"start": v(-6.43, -3.87) * mm, "end": v(-6.37, -4) * mm});
            skLineSegment(sketch, "E522", {"start": v(-6.37, -4) * mm, "end": v(-6.32, -4.12) * mm});
            skLineSegment(sketch, "E523", {"start": v(-6.32, -4.12) * mm, "end": v(-6.28, -4.25) * mm});
            skLineSegment(sketch, "E524", {"start": v(-6.28, -4.25) * mm, "end": v(-6.25, -4.37) * mm});
            skLineSegment(sketch, "E525", {"start": v(-6.25, -4.37) * mm, "end": v(-6.23, -4.5) * mm});
            skLineSegment(sketch, "E526", {"start": v(-6.23, -4.5) * mm, "end": v(-6.22, -4.61) * mm});
            skLineSegment(sketch, "E527", {"start": v(-6.22, -4.61) * mm, "end": v(-6.22, -4.73) * mm});
            skLineSegment(sketch, "E528", {"start": v(-6.22, -4.73) * mm, "end": v(-6.22, -4.84) * mm});
            skLineSegment(sketch, "E529", {"start": v(-6.22, -4.84) * mm, "end": v(-6.23, -4.95) * mm});
            skLineSegment(sketch, "E530", {"start": v(-6.23, -4.95) * mm, "end": v(-6.26, -5.05) * mm});
            skLineSegment(sketch, "E531", {"start": v(-6.26, -5.05) * mm, "end": v(-6.29, -5.15) * mm});
            skLineSegment(sketch, "E532", {"start": v(-6.29, -5.15) * mm, "end": v(-6.33, -5.24) * mm});
            skLineSegment(sketch, "E533", {"start": v(-6.33, -5.24) * mm, "end": v(-6.38, -5.32) * mm});
            skLineSegment(sketch, "E534", {"start": v(-6.38, -5.32) * mm, "end": v(-6.43, -5.4) * mm});
            skLineSegment(sketch, "E535", {"start": v(-6.43, -5.4) * mm, "end": v(-6.5, -5.47) * mm});
            skLineSegment(sketch, "E536", {"start": v(5.47, -6.5) * mm, "end": v(5.4, -6.43) * mm});
            skLineSegment(sketch, "E537", {"start": v(5.4, -6.43) * mm, "end": v(5.32, -6.38) * mm});
            skLineSegment(sketch, "E538", {"start": v(5.32, -6.38) * mm, "end": v(5.24, -6.33) * mm});
            skLineSegment(sketch, "E539", {"start": v(5.24, -6.33) * mm, "end": v(5.15, -6.29) * mm});
            skLineSegment(sketch, "E540", {"start": v(5.15, -6.29) * mm, "end": v(5.05, -6.26) * mm});
            skLineSegment(sketch, "E541", {"start": v(5.05, -6.26) * mm, "end": v(4.95, -6.23) * mm});
            skLineSegment(sketch, "E542", {"start": v(4.95, -6.23) * mm, "end": v(4.84, -6.22) * mm});
            skLineSegment(sketch, "E543", {"start": v(4.84, -6.22) * mm, "end": v(4.73, -6.22) * mm});
            skLineSegment(sketch, "E544", {"start": v(4.73, -6.22) * mm, "end": v(4.61, -6.22) * mm});
            skLineSegment(sketch, "E545", {"start": v(4.61, -6.22) * mm, "end": v(4.5, -6.23) * mm});
            skLineSegment(sketch, "E546", {"start": v(4.5, -6.23) * mm, "end": v(4.37, -6.25) * mm});
            skLineSegment(sketch, "E547", {"start": v(4.37, -6.25) * mm, "end": v(4.25, -6.28) * mm});
            skLineSegment(sketch, "E548", {"start": v(4.25, -6.28) * mm, "end": v(4.12, -6.32) * mm});
            skLineSegment(sketch, "E549", {"start": v(4.12, -6.32) * mm, "end": v(4, -6.37) * mm});
            skLineSegment(sketch, "E550", {"start": v(4, -6.37) * mm, "end": v(3.87, -6.43) * mm});
            skLineSegment(sketch, "E551", {"start": v(3.87, -6.43) * mm, "end": v(3.75, -6.5) * mm});
            skLineSegment(sketch, "E552", {"start": v(3.75, -6.5) * mm, "end": v(3.63, -6.57) * mm});
            skLineSegment(sketch, "E553", {"start": v(3.63, -6.57) * mm, "end": v(3.52, -6.65) * mm});
            skLineSegment(sketch, "E554", {"start": v(3.52, -6.65) * mm, "end": v(3.41, -6.73) * mm});
            skLineSegment(sketch, "E555", {"start": v(3.41, -6.73) * mm, "end": v(3.32, -6.82) * mm});
            skLineSegment(sketch, "E556", {"start": v(3.32, -6.82) * mm, "end": v(3.23, -6.92) * mm});
            skLineSegment(sketch, "E557", {"start": v(3.23, -6.92) * mm, "end": v(3.15, -7.01) * mm});
            skLineSegment(sketch, "E558", {"start": v(3.15, -7.01) * mm, "end": v(3.08, -7.1) * mm});
            skLineSegment(sketch, "E559", {"start": v(3.08, -7.1) * mm, "end": v(3.02, -7.2) * mm});
            skLineSegment(sketch, "E560", {"start": v(3.02, -7.2) * mm, "end": v(2.96, -7.3) * mm});
            skLineSegment(sketch, "E561", {"start": v(2.96, -7.3) * mm, "end": v(2.92, -7.4) * mm});
            skLineSegment(sketch, "E562", {"start": v(2.92, -7.4) * mm, "end": v(2.9, -7.5) * mm});
            skLineSegment(sketch, "E563", {"start": v(2.9, -7.5) * mm, "end": v(2.87, -7.6) * mm});
            skLineSegment(sketch, "E564", {"start": v(2.87, -7.6) * mm, "end": v(2.86, -7.7) * mm});
            skLineSegment(sketch, "E565", {"start": v(2.86, -7.7) * mm, "end": v(2.86, -7.8) * mm});
            skLineSegment(sketch, "E566", {"start": v(2.86, -7.8) * mm, "end": v(2.87, -7.9) * mm});
            skLineSegment(sketch, "E567", {"start": v(2.87, -7.9) * mm, "end": v(2.9, -7.99) * mm});
            skLineSegment(sketch, "E568", {"start": v(-5.47, -6.5) * mm, "end": v(-5.4, -6.43) * mm});
            skLineSegment(sketch, "E569", {"start": v(-5.4, -6.43) * mm, "end": v(-5.32, -6.38) * mm});
            skLineSegment(sketch, "E570", {"start": v(-5.32, -6.38) * mm, "end": v(-5.24, -6.33) * mm});
            skLineSegment(sketch, "E571", {"start": v(-5.24, -6.33) * mm, "end": v(-5.15, -6.29) * mm});
            skLineSegment(sketch, "E572", {"start": v(-5.15, -6.29) * mm, "end": v(-5.05, -6.26) * mm});
            skLineSegment(sketch, "E573", {"start": v(-5.05, -6.26) * mm, "end": v(-4.95, -6.23) * mm});
            skLineSegment(sketch, "E574", {"start": v(-4.95, -6.23) * mm, "end": v(-4.84, -6.22) * mm});
            skLineSegment(sketch, "E575", {"start": v(-4.84, -6.22) * mm, "end": v(-4.73, -6.22) * mm});
            skLineSegment(sketch, "E576", {"start": v(-4.73, -6.22) * mm, "end": v(-4.61, -6.22) * mm});
            skLineSegment(sketch, "E577", {"start": v(-4.61, -6.22) * mm, "end": v(-4.5, -6.23) * mm});
            skLineSegment(sketch, "E578", {"start": v(-4.5, -6.23) * mm, "end": v(-4.37, -6.25) * mm});
            skLineSegment(sketch, "E579", {"start": v(-4.37, -6.25) * mm, "end": v(-4.25, -6.28) * mm});
            skLineSegment(sketch, "E580", {"start": v(-4.25, -6.28) * mm, "end": v(-4.12, -6.32) * mm});
            skLineSegment(sketch, "E581", {"start": v(-4.12, -6.32) * mm, "end": v(-4, -6.37) * mm});
            skLineSegment(sketch, "E582", {"start": v(-4, -6.37) * mm, "end": v(-3.87, -6.43) * mm});
            skLineSegment(sketch, "E583", {"start": v(-3.87, -6.43) * mm, "end": v(-3.75, -6.5) * mm});
            skLineSegment(sketch, "E584", {"start": v(-3.75, -6.5) * mm, "end": v(-3.63, -6.57) * mm});
            skLineSegment(sketch, "E585", {"start": v(-3.63, -6.57) * mm, "end": v(-3.52, -6.65) * mm});
            skLineSegment(sketch, "E586", {"start": v(-3.52, -6.65) * mm, "end": v(-3.41, -6.73) * mm});
            skLineSegment(sketch, "E587", {"start": v(-3.41, -6.73) * mm, "end": v(-3.32, -6.82) * mm});
            skLineSegment(sketch, "E588", {"start": v(-3.32, -6.82) * mm, "end": v(-3.23, -6.92) * mm});
            skLineSegment(sketch, "E589", {"start": v(-3.23, -6.92) * mm, "end": v(-3.15, -7.01) * mm});
            skLineSegment(sketch, "E590", {"start": v(-3.15, -7.01) * mm, "end": v(-3.08, -7.1) * mm});
            skLineSegment(sketch, "E591", {"start": v(-3.08, -7.1) * mm, "end": v(-3.02, -7.2) * mm});
            skLineSegment(sketch, "E592", {"start": v(-3.02, -7.2) * mm, "end": v(-2.96, -7.3) * mm});
            skLineSegment(sketch, "E593", {"start": v(-2.96, -7.3) * mm, "end": v(-2.92, -7.4) * mm});
            skLineSegment(sketch, "E594", {"start": v(-2.92, -7.4) * mm, "end": v(-2.9, -7.5) * mm});
            skLineSegment(sketch, "E595", {"start": v(-2.9, -7.5) * mm, "end": v(-2.87, -7.6) * mm});
            skLineSegment(sketch, "E596", {"start": v(-2.87, -7.6) * mm, "end": v(-2.86, -7.7) * mm});
            skLineSegment(sketch, "E597", {"start": v(-2.86, -7.7) * mm, "end": v(-2.86, -7.8) * mm});
            skLineSegment(sketch, "E598", {"start": v(-2.86, -7.8) * mm, "end": v(-2.87, -7.9) * mm});
            skLineSegment(sketch, "E599", {"start": v(-2.87, -7.9) * mm, "end": v(-2.9, -7.99) * mm});
            skLineSegment(sketch, "E600", {"start": v(1.49, -8.37) * mm, "end": v(1.46, -8.28) * mm});
            skLineSegment(sketch, "E601", {"start": v(1.46, -8.28) * mm, "end": v(1.43, -8.19) * mm});
            skLineSegment(sketch, "E602", {"start": v(1.43, -8.19) * mm, "end": v(1.38, -8.1) * mm});
            skLineSegment(sketch, "E603", {"start": v(1.38, -8.1) * mm, "end": v(1.32, -8.03) * mm});
            skLineSegment(sketch, "E604", {"start": v(1.32, -8.03) * mm, "end": v(1.25, -7.95) * mm});
            skLineSegment(sketch, "E605", {"start": v(1.25, -7.95) * mm, "end": v(1.17, -7.88) * mm});
            skLineSegment(sketch, "E606", {"start": v(1.17, -7.88) * mm, "end": v(1.09, -7.81) * mm});
            skLineSegment(sketch, "E607", {"start": v(1.09, -7.81) * mm, "end": v(1, -7.75) * mm});
            skLineSegment(sketch, "E608", {"start": v(1, -7.75) * mm, "end": v(0.89, -7.7) * mm});
            skLineSegment(sketch, "E609", {"start": v(0.89, -7.7) * mm, "end": v(0.78, -7.65) * mm});
            skLineSegment(sketch, "E610", {"start": v(0.78, -7.65) * mm, "end": v(0.66, -7.6) * mm});
            skLineSegment(sketch, "E611", {"start": v(0.66, -7.6) * mm, "end": v(0.54, -7.57) * mm});
            skLineSegment(sketch, "E612", {"start": v(0.54, -7.57) * mm, "end": v(0.41, -7.54) * mm});
            skLineSegment(sketch, "E613", {"start": v(0.41, -7.54) * mm, "end": v(0.28, -7.52) * mm});
            skLineSegment(sketch, "E614", {"start": v(0.28, -7.52) * mm, "end": v(0.14, -7.5) * mm});
            skLineSegment(sketch, "E615", {"start": v(0.14, -7.5) * mm, "end": v(0, -7.5) * mm});
            skLineSegment(sketch, "E616", {"start": v(0, -7.5) * mm, "end": v(-0.14, -7.5) * mm});
            skLineSegment(sketch, "E617", {"start": v(-0.14, -7.5) * mm, "end": v(-0.28, -7.52) * mm});
            skLineSegment(sketch, "E618", {"start": v(-0.28, -7.52) * mm, "end": v(-0.41, -7.54) * mm});
            skLineSegment(sketch, "E619", {"start": v(-0.41, -7.54) * mm, "end": v(-0.54, -7.57) * mm});
            skLineSegment(sketch, "E620", {"start": v(-0.54, -7.57) * mm, "end": v(-0.66, -7.6) * mm});
            skLineSegment(sketch, "E621", {"start": v(-0.66, -7.6) * mm, "end": v(-0.78, -7.65) * mm});
            skLineSegment(sketch, "E622", {"start": v(-0.78, -7.65) * mm, "end": v(-0.89, -7.7) * mm});
            skLineSegment(sketch, "E623", {"start": v(-0.89, -7.7) * mm, "end": v(-1, -7.75) * mm});
            skLineSegment(sketch, "E624", {"start": v(-1, -7.75) * mm, "end": v(-1.09, -7.81) * mm});
            skLineSegment(sketch, "E625", {"start": v(-1.09, -7.81) * mm, "end": v(-1.17, -7.88) * mm});
            skLineSegment(sketch, "E626", {"start": v(-1.17, -7.88) * mm, "end": v(-1.25, -7.95) * mm});
            skLineSegment(sketch, "E627", {"start": v(-1.25, -7.95) * mm, "end": v(-1.32, -8.03) * mm});
            skLineSegment(sketch, "E628", {"start": v(-1.32, -8.03) * mm, "end": v(-1.38, -8.1) * mm});
            skLineSegment(sketch, "E629", {"start": v(-1.38, -8.1) * mm, "end": v(-1.43, -8.19) * mm});
            skLineSegment(sketch, "E630", {"start": v(-1.43, -8.19) * mm, "end": v(-1.46, -8.28) * mm});
            skLineSegment(sketch, "E631", {"start": v(-1.46, -8.28) * mm, "end": v(-1.49, -8.37) * mm});
            skArc(sketch, "E632", {"start": v(0, 8.48) * mm, "mid": v(-6, 6) * mm, "end": v(-8.48, 0) * mm});
            skArc(sketch, "E633", {"start": v(-8.48, 0) * mm, "mid": v(-6, -6) * mm, "end": v(0, -8.48) * mm});
            skArc(sketch, "E634", {"start": v(0, -8.48) * mm, "mid": v(6, -6) * mm, "end": v(8.48, 0) * mm});
            skArc(sketch, "E635", {"start": v(8.48, 0) * mm, "mid": v(6, 6) * mm, "end": v(0, 8.48) * mm});
            skSolve(sketch);
        }
        {
            var Q0;
            Q0=makeQuery(id+"F0.imprint","IMPRINT",FACE,{"disambiguationData":[TD([[makeQuery(id+"F0.imprint","IMPRINT",EDGE,{"derivedFrom":sQuery(id+"F0.wireOp",EDGE,"E244")}),-1.0]])]});
            extrude(context, id + "F1", {"entities" : qUnion([Q0]), "depth" : 10 * mm});
        }
        {
            var Q0;
            {var subQ40=sQuery(id+"F0.wireOp",EDGE,"E1");Q0=makeQuery(id+"F0.imprint","IMPRINT",FACE,{"disambiguationData":[TD([[makeQuery(id+"F0.imprint","IMPRINT",EDGE,{"derivedFrom":subQ40}),1.0]])]});}
            extrude(context, id + "F2", {"entities" : qUnion([Q0]), "operationType" : NewBodyOperationType.ADD, "depth" : 19 * mm});
        }
        {
            var Q0;
            {var subQ0=sQuery(id+"F0.wireOp",EDGE,"E249");Q0=makeQuery(id+"F0.imprint","IMPRINT",FACE,{"disambiguationData":[TD([[makeQuery(id+"F0.imprint","IMPRINT",EDGE,{"derivedFrom":subQ0}),-1.0]])]});}
            var Q1;
            {var subQ0=sQuery(id+"F0.wireOp",EDGE,"E313");Q1=makeQuery(id+"F0.imprint","IMPRINT",FACE,{"disambiguationData":[TD([[makeQuery(id+"F0.imprint","IMPRINT",EDGE,{"derivedFrom":subQ0}),1.0]])]});}
            var Q2;
            {var subQ0=sQuery(id+"F0.wireOp",EDGE,"E409");Q2=makeQuery(id+"F0.imprint","IMPRINT",FACE,{"disambiguationData":[TD([[makeQuery(id+"F0.imprint","IMPRINT",EDGE,{"derivedFrom":subQ0}),1.0]])]});}
            var Q3;
            {var subQ0=sQuery(id+"F0.wireOp",EDGE,"E473");Q3=makeQuery(id+"F0.imprint","IMPRINT",FACE,{"disambiguationData":[TD([[makeQuery(id+"F0.imprint","IMPRINT",EDGE,{"derivedFrom":subQ0}),1.0]])]});}
            var Q4;
            {var subQ0=sQuery(id+"F0.wireOp",EDGE,"E505");Q4=makeQuery(id+"F0.imprint","IMPRINT",FACE,{"disambiguationData":[TD([[makeQuery(id+"F0.imprint","IMPRINT",EDGE,{"derivedFrom":subQ0}),-1.0]])]});}
            var Q5;
            {var subQ0=sQuery(id+"F0.wireOp",EDGE,"E569");Q5=makeQuery(id+"F0.imprint","IMPRINT",FACE,{"disambiguationData":[TD([[makeQuery(id+"F0.imprint","IMPRINT",EDGE,{"derivedFrom":subQ0}),-1.0]])]});}
            var Q6;
            {var subQ0=sQuery(id+"F0.wireOp",EDGE,"E601");Q6=makeQuery(id+"F0.imprint","IMPRINT",FACE,{"disambiguationData":[TD([[makeQuery(id+"F0.imprint","IMPRINT",EDGE,{"derivedFrom":subQ0}),1.0]])]});}
            var Q7;
            {var subQ5=sQuery(id+"F0.wireOp",EDGE,"E537");Q7=makeQuery(id+"F0.imprint","IMPRINT",FACE,{"disambiguationData":[TD([[makeQuery(id+"F0.imprint","IMPRINT",EDGE,{"derivedFrom":subQ5}),1.0]])]});}
            var Q8;
            {var subQ0=sQuery(id+"F0.wireOp",EDGE,"E441");Q8=makeQuery(id+"F0.imprint","IMPRINT",FACE,{"disambiguationData":[TD([[makeQuery(id+"F0.imprint","IMPRINT",EDGE,{"derivedFrom":subQ0}),1.0]])]});}
            var Q9;
            {var subQ0=sQuery(id+"F0.wireOp",EDGE,"E377");Q9=makeQuery(id+"F0.imprint","IMPRINT",FACE,{"disambiguationData":[TD([[makeQuery(id+"F0.imprint","IMPRINT",EDGE,{"derivedFrom":subQ0}),1.0]])]});}
            var Q10;
            {var subQ0=sQuery(id+"F0.wireOp",EDGE,"E345");Q10=makeQuery(id+"F0.imprint","IMPRINT",FACE,{"disambiguationData":[TD([[makeQuery(id+"F0.imprint","IMPRINT",EDGE,{"derivedFrom":subQ0}),-1.0]])]});}
            var Q11;
            {var subQ0=sQuery(id+"F0.wireOp",EDGE,"E281");Q11=makeQuery(id+"F0.imprint","IMPRINT",FACE,{"disambiguationData":[TD([[makeQuery(id+"F0.imprint","IMPRINT",EDGE,{"derivedFrom":subQ0}),-1.0]])]});}
            extrude(context, id + "F3", {"entities" : qUnion([Q0, Q1, Q2, Q3, Q4, Q5, Q6, Q7, Q8, Q9, Q10, Q11]), "operationType" : NewBodyOperationType.ADD, "depth" : 2 * mm});
        }
        {
            var Q0;
            Q0=makeQuery(id+"F0.imprint","IMPRINT",FACE,{"disambiguationData":[TD([[makeQuery(id+"F0.imprint","IMPRINT",EDGE,{"derivedFrom":sQuery(id+"F0.wireOp",EDGE,"E244")}),1.0]])]});
            extrude(context, id + "F4", {"entities" : qUnion([Q0]), "depth" : 9.5 * mm});
        }
        {
            var Q0;
            {var subQ0=sQuery(id+"F0.wireOp",EDGE,"E41");Q0=makeQuery(id+"F0.imprint","IMPRINT",FACE,{"disambiguationData":[TD([[makeQuery(id+"F0.imprint","IMPRINT",EDGE,{"derivedFrom":subQ0}),1.0]])]});}
            var Q1;
            {var subQ0=sQuery(id+"F0.wireOp",EDGE,"E1");Q1=makeQuery(id+"F0.imprint","IMPRINT",FACE,{"disambiguationData":[TD([[makeQuery(id+"F0.imprint","IMPRINT",EDGE,{"derivedFrom":subQ0}),-1.0]])]});}
            var Q2;
            {var subQ0=sQuery(id+"F0.wireOp",EDGE,"E21");Q2=makeQuery(id+"F0.imprint","IMPRINT",FACE,{"disambiguationData":[TD([[makeQuery(id+"F0.imprint","IMPRINT",EDGE,{"derivedFrom":subQ0}),-1.0]])]});}
            var Q3;
            {var subQ0=sQuery(id+"F0.wireOp",EDGE,"E61");Q3=makeQuery(id+"F0.imprint","IMPRINT",FACE,{"disambiguationData":[TD([[makeQuery(id+"F0.imprint","IMPRINT",EDGE,{"derivedFrom":subQ0}),-1.0]])]});}
            var Q4;
            {var subQ0=sQuery(id+"F0.wireOp",EDGE,"E81");Q4=makeQuery(id+"F0.imprint","IMPRINT",FACE,{"disambiguationData":[TD([[makeQuery(id+"F0.imprint","IMPRINT",EDGE,{"derivedFrom":subQ0}),1.0]])]});}
            var Q5;
            {var subQ0=sQuery(id+"F0.wireOp",EDGE,"E121");Q5=makeQuery(id+"F0.imprint","IMPRINT",FACE,{"disambiguationData":[TD([[makeQuery(id+"F0.imprint","IMPRINT",EDGE,{"derivedFrom":subQ0}),1.0]])]});}
            var Q6;
            {var subQ5=sQuery(id+"F0.wireOp",EDGE,"E181");Q6=makeQuery(id+"F0.imprint","IMPRINT",FACE,{"disambiguationData":[TD([[makeQuery(id+"F0.imprint","IMPRINT",EDGE,{"derivedFrom":subQ5}),1.0]])]});}
            var Q7;
            {var subQ0=sQuery(id+"F0.wireOp",EDGE,"E221");Q7=makeQuery(id+"F0.imprint","IMPRINT",FACE,{"disambiguationData":[TD([[makeQuery(id+"F0.imprint","IMPRINT",EDGE,{"derivedFrom":subQ0}),1.0]])]});}
            var Q8;
            {var subQ5=sQuery(id+"F0.wireOp",EDGE,"E201");Q8=makeQuery(id+"F0.imprint","IMPRINT",FACE,{"disambiguationData":[TD([[makeQuery(id+"F0.imprint","IMPRINT",EDGE,{"derivedFrom":subQ5}),-1.0]])]});}
            var Q9;
            {var subQ0=sQuery(id+"F0.wireOp",EDGE,"E161");Q9=makeQuery(id+"F0.imprint","IMPRINT",FACE,{"disambiguationData":[TD([[makeQuery(id+"F0.imprint","IMPRINT",EDGE,{"derivedFrom":subQ0}),-1.0]])]});}
            var Q10;
            {var subQ0=sQuery(id+"F0.wireOp",EDGE,"E141");Q10=makeQuery(id+"F0.imprint","IMPRINT",FACE,{"disambiguationData":[TD([[makeQuery(id+"F0.imprint","IMPRINT",EDGE,{"derivedFrom":subQ0}),1.0]])]});}
            var Q11;
            {var subQ5=sQuery(id+"F0.wireOp",EDGE,"E101");Q11=makeQuery(id+"F0.imprint","IMPRINT",FACE,{"disambiguationData":[TD([[makeQuery(id+"F0.imprint","IMPRINT",EDGE,{"derivedFrom":subQ5}),1.0]])]});}
            extrude(context, id + "F5", {"entities" : qUnion([Q0, Q1, Q2, Q3, Q4, Q5, Q6, Q7, Q8, Q9, Q10, Q11]), "operationType" : NewBodyOperationType.ADD, "depth" : 12 * mm});
        }
        {
            var Q0;
            Q0=makeQuery(id+"F2.opExtrude","CAP_FACE",FACE,{"disambiguationData":[OSD([sQuery(id+"F0.wireOp",EDGE,"E0"),sQuery(id+"F0.wireOp",EDGE,"E1"),sQuery(id+"F0.wireOp",EDGE,"E2"),sQuery(id+"F0.wireOp",EDGE,"E3"),sQuery(id+"F0.wireOp",EDGE,"E4"),sQuery(id+"F0.wireOp",EDGE,"E5"),sQuery(id+"F0.wireOp",EDGE,"E6"),sQuery(id+"F0.wireOp",EDGE,"E7"),sQuery(id+"F0.wireOp",EDGE,"E8"),sQuery(id+"F0.wireOp",EDGE,"E9"),sQuery(id+"F0.wireOp",EDGE,"E10"),sQuery(id+"F0.wireOp",EDGE,"E11"),sQuery(id+"F0.wireOp",EDGE,"E12"),sQuery(id+"F0.wireOp",EDGE,"E13"),sQuery(id+"F0.wireOp",EDGE,"E14"),sQuery(id+"F0.wireOp",EDGE,"E15"),sQuery(id+"F0.wireOp",EDGE,"E16"),sQuery(id+"F0.wireOp",EDGE,"E17"),sQuery(id+"F0.wireOp",EDGE,"E18"),sQuery(id+"F0.wireOp",EDGE,"E19"),sQuery(id+"F0.wireOp",EDGE,"E20"),sQuery(id+"F0.wireOp",EDGE,"E21"),sQuery(id+"F0.wireOp",EDGE,"E22"),sQuery(id+"F0.wireOp",EDGE,"E23"),sQuery(id+"F0.wireOp",EDGE,"E24"),sQuery(id+"F0.wireOp",EDGE,"E25"),sQuery(id+"F0.wireOp",EDGE,"E26"),sQuery(id+"F0.wireOp",EDGE,"E27"),sQuery(id+"F0.wireOp",EDGE,"E28"),sQuery(id+"F0.wireOp",EDGE,"E29"),sQuery(id+"F0.wireOp",EDGE,"E30"),sQuery(id+"F0.wireOp",EDGE,"E31"),sQuery(id+"F0.wireOp",EDGE,"E32"),sQuery(id+"F0.wireOp",EDGE,"E33"),sQuery(id+"F0.wireOp",EDGE,"E34"),sQuery(id+"F0.wireOp",EDGE,"E35"),sQuery(id+"F0.wireOp",EDGE,"E36"),sQuery(id+"F0.wireOp",EDGE,"E37"),sQuery(id+"F0.wireOp",EDGE,"E38"),sQuery(id+"F0.wireOp",EDGE,"E39"),sQuery(id+"F0.wireOp",EDGE,"E40"),sQuery(id+"F0.wireOp",EDGE,"E41"),sQuery(id+"F0.wireOp",EDGE,"E42"),sQuery(id+"F0.wireOp",EDGE,"E43"),sQuery(id+"F0.wireOp",EDGE,"E44"),sQuery(id+"F0.wireOp",EDGE,"E45"),sQuery(id+"F0.wireOp",EDGE,"E46"),sQuery(id+"F0.wireOp",EDGE,"E47"),sQuery(id+"F0.wireOp",EDGE,"E48"),sQuery(id+"F0.wireOp",EDGE,"E49"),sQuery(id+"F0.wireOp",EDGE,"E50"),sQuery(id+"F0.wireOp",EDGE,"E51"),sQuery(id+"F0.wireOp",EDGE,"E52"),sQuery(id+"F0.wireOp",EDGE,"E53"),sQuery(id+"F0.wireOp",EDGE,"E54"),sQuery(id+"F0.wireOp",EDGE,"E55"),sQuery(id+"F0.wireOp",EDGE,"E56"),sQuery(id+"F0.wireOp",EDGE,"E57"),sQuery(id+"F0.wireOp",EDGE,"E58"),sQuery(id+"F0.wireOp",EDGE,"E59"),sQuery(id+"F0.wireOp",EDGE,"E60"),sQuery(id+"F0.wireOp",EDGE,"E61"),sQuery(id+"F0.wireOp",EDGE,"E62"),sQuery(id+"F0.wireOp",EDGE,"E63"),sQuery(id+"F0.wireOp",EDGE,"E64"),sQuery(id+"F0.wireOp",EDGE,"E65"),sQuery(id+"F0.wireOp",EDGE,"E66"),sQuery(id+"F0.wireOp",EDGE,"E67"),sQuery(id+"F0.wireOp",EDGE,"E68"),sQuery(id+"F0.wireOp",EDGE,"E69"),sQuery(id+"F0.wireOp",EDGE,"E70"),sQuery(id+"F0.wireOp",EDGE,"E71"),sQuery(id+"F0.wireOp",EDGE,"E72"),sQuery(id+"F0.wireOp",EDGE,"E73"),sQuery(id+"F0.wireOp",EDGE,"E74"),sQuery(id+"F0.wireOp",EDGE,"E75"),sQuery(id+"F0.wireOp",EDGE,"E76"),sQuery(id+"F0.wireOp",EDGE,"E77"),sQuery(id+"F0.wireOp",EDGE,"E78"),sQuery(id+"F0.wireOp",EDGE,"E79"),sQuery(id+"F0.wireOp",EDGE,"E80"),sQuery(id+"F0.wireOp",EDGE,"E81"),sQuery(id+"F0.wireOp",EDGE,"E82"),sQuery(id+"F0.wireOp",EDGE,"E83"),sQuery(id+"F0.wireOp",EDGE,"E84"),sQuery(id+"F0.wireOp",EDGE,"E85"),sQuery(id+"F0.wireOp",EDGE,"E86"),sQuery(id+"F0.wireOp",EDGE,"E87"),sQuery(id+"F0.wireOp",EDGE,"E88"),sQuery(id+"F0.wireOp",EDGE,"E89"),sQuery(id+"F0.wireOp",EDGE,"E90"),sQuery(id+"F0.wireOp",EDGE,"E91"),sQuery(id+"F0.wireOp",EDGE,"E92"),sQuery(id+"F0.wireOp",EDGE,"E93"),sQuery(id+"F0.wireOp",EDGE,"E94"),sQuery(id+"F0.wireOp",EDGE,"E95"),sQuery(id+"F0.wireOp",EDGE,"E96"),sQuery(id+"F0.wireOp",EDGE,"E97"),sQuery(id+"F0.wireOp",EDGE,"E98"),sQuery(id+"F0.wireOp",EDGE,"E99"),sQuery(id+"F0.wireOp",EDGE,"E100"),sQuery(id+"F0.wireOp",EDGE,"E101"),sQuery(id+"F0.wireOp",EDGE,"E102"),sQuery(id+"F0.wireOp",EDGE,"E103"),sQuery(id+"F0.wireOp",EDGE,"E104"),sQuery(id+"F0.wireOp",EDGE,"E105"),sQuery(id+"F0.wireOp",EDGE,"E106"),sQuery(id+"F0.wireOp",EDGE,"E107"),sQuery(id+"F0.wireOp",EDGE,"E108"),sQuery(id+"F0.wireOp",EDGE,"E109"),sQuery(id+"F0.wireOp",EDGE,"E110"),sQuery(id+"F0.wireOp",EDGE,"E111"),sQuery(id+"F0.wireOp",EDGE,"E112"),sQuery(id+"F0.wireOp",EDGE,"E113"),sQuery(id+"F0.wireOp",EDGE,"E114"),sQuery(id+"F0.wireOp",EDGE,"E115"),sQuery(id+"F0.wireOp",EDGE,"E116"),sQuery(id+"F0.wireOp",EDGE,"E117"),sQuery(id+"F0.wireOp",EDGE,"E118"),sQuery(id+"F0.wireOp",EDGE,"E119"),sQuery(id+"F0.wireOp",EDGE,"E120"),sQuery(id+"F0.wireOp",EDGE,"E121"),sQuery(id+"F0.wireOp",EDGE,"E122"),sQuery(id+"F0.wireOp",EDGE,"E123"),sQuery(id+"F0.wireOp",EDGE,"E124"),sQuery(id+"F0.wireOp",EDGE,"E125"),sQuery(id+"F0.wireOp",EDGE,"E126"),sQuery(id+"F0.wireOp",EDGE,"E127"),sQuery(id+"F0.wireOp",EDGE,"E128"),sQuery(id+"F0.wireOp",EDGE,"E129"),sQuery(id+"F0.wireOp",EDGE,"E130"),sQuery(id+"F0.wireOp",EDGE,"E131"),sQuery(id+"F0.wireOp",EDGE,"E132"),sQuery(id+"F0.wireOp",EDGE,"E133"),sQuery(id+"F0.wireOp",EDGE,"E134"),sQuery(id+"F0.wireOp",EDGE,"E135"),sQuery(id+"F0.wireOp",EDGE,"E136"),sQuery(id+"F0.wireOp",EDGE,"E137"),sQuery(id+"F0.wireOp",EDGE,"E138"),sQuery(id+"F0.wireOp",EDGE,"E139"),sQuery(id+"F0.wireOp",EDGE,"E140"),sQuery(id+"F0.wireOp",EDGE,"E141"),sQuery(id+"F0.wireOp",EDGE,"E142"),sQuery(id+"F0.wireOp",EDGE,"E143"),sQuery(id+"F0.wireOp",EDGE,"E144"),sQuery(id+"F0.wireOp",EDGE,"E145"),sQuery(id+"F0.wireOp",EDGE,"E146"),sQuery(id+"F0.wireOp",EDGE,"E147"),sQuery(id+"F0.wireOp",EDGE,"E148"),sQuery(id+"F0.wireOp",EDGE,"E149"),sQuery(id+"F0.wireOp",EDGE,"E150"),sQuery(id+"F0.wireOp",EDGE,"E151"),sQuery(id+"F0.wireOp",EDGE,"E152"),sQuery(id+"F0.wireOp",EDGE,"E153"),sQuery(id+"F0.wireOp",EDGE,"E154"),sQuery(id+"F0.wireOp",EDGE,"E155"),sQuery(id+"F0.wireOp",EDGE,"E156"),sQuery(id+"F0.wireOp",EDGE,"E157"),sQuery(id+"F0.wireOp",EDGE,"E158"),sQuery(id+"F0.wireOp",EDGE,"E159"),sQuery(id+"F0.wireOp",EDGE,"E160"),sQuery(id+"F0.wireOp",EDGE,"E161"),sQuery(id+"F0.wireOp",EDGE,"E162"),sQuery(id+"F0.wireOp",EDGE,"E163"),sQuery(id+"F0.wireOp",EDGE,"E164"),sQuery(id+"F0.wireOp",EDGE,"E165"),sQuery(id+"F0.wireOp",EDGE,"E166"),sQuery(id+"F0.wireOp",EDGE,"E167"),sQuery(id+"F0.wireOp",EDGE,"E168"),sQuery(id+"F0.wireOp",EDGE,"E169"),sQuery(id+"F0.wireOp",EDGE,"E170"),sQuery(id+"F0.wireOp",EDGE,"E171"),sQuery(id+"F0.wireOp",EDGE,"E172"),sQuery(id+"F0.wireOp",EDGE,"E173"),sQuery(id+"F0.wireOp",EDGE,"E174"),sQuery(id+"F0.wireOp",EDGE,"E175"),sQuery(id+"F0.wireOp",EDGE,"E176"),sQuery(id+"F0.wireOp",EDGE,"E177"),sQuery(id+"F0.wireOp",EDGE,"E178"),sQuery(id+"F0.wireOp",EDGE,"E179"),sQuery(id+"F0.wireOp",EDGE,"E180"),sQuery(id+"F0.wireOp",EDGE,"E181"),sQuery(id+"F0.wireOp",EDGE,"E182"),sQuery(id+"F0.wireOp",EDGE,"E183"),sQuery(id+"F0.wireOp",EDGE,"E184"),sQuery(id+"F0.wireOp",EDGE,"E185"),sQuery(id+"F0.wireOp",EDGE,"E186"),sQuery(id+"F0.wireOp",EDGE,"E187"),sQuery(id+"F0.wireOp",EDGE,"E188"),sQuery(id+"F0.wireOp",EDGE,"E189"),sQuery(id+"F0.wireOp",EDGE,"E190"),sQuery(id+"F0.wireOp",EDGE,"E191"),sQuery(id+"F0.wireOp",EDGE,"E192"),sQuery(id+"F0.wireOp",EDGE,"E193"),sQuery(id+"F0.wireOp",EDGE,"E194"),sQuery(id+"F0.wireOp",EDGE,"E195"),sQuery(id+"F0.wireOp",EDGE,"E196"),sQuery(id+"F0.wireOp",EDGE,"E197"),sQuery(id+"F0.wireOp",EDGE,"E198"),sQuery(id+"F0.wireOp",EDGE,"E199"),sQuery(id+"F0.wireOp",EDGE,"E200"),sQuery(id+"F0.wireOp",EDGE,"E201"),sQuery(id+"F0.wireOp",EDGE,"E202"),sQuery(id+"F0.wireOp",EDGE,"E203"),sQuery(id+"F0.wireOp",EDGE,"E204"),sQuery(id+"F0.wireOp",EDGE,"E205"),sQuery(id+"F0.wireOp",EDGE,"E206"),sQuery(id+"F0.wireOp",EDGE,"E207"),sQuery(id+"F0.wireOp",EDGE,"E208"),sQuery(id+"F0.wireOp",EDGE,"E209"),sQuery(id+"F0.wireOp",EDGE,"E210"),sQuery(id+"F0.wireOp",EDGE,"E211"),sQuery(id+"F0.wireOp",EDGE,"E212"),sQuery(id+"F0.wireOp",EDGE,"E213"),sQuery(id+"F0.wireOp",EDGE,"E214"),sQuery(id+"F0.wireOp",EDGE,"E215"),sQuery(id+"F0.wireOp",EDGE,"E216"),sQuery(id+"F0.wireOp",EDGE,"E217"),sQuery(id+"F0.wireOp",EDGE,"E218"),sQuery(id+"F0.wireOp",EDGE,"E219"),sQuery(id+"F0.wireOp",EDGE,"E220"),sQuery(id+"F0.wireOp",EDGE,"E221"),sQuery(id+"F0.wireOp",EDGE,"E222"),sQuery(id+"F0.wireOp",EDGE,"E223"),sQuery(id+"F0.wireOp",EDGE,"E224"),sQuery(id+"F0.wireOp",EDGE,"E225"),sQuery(id+"F0.wireOp",EDGE,"E226"),sQuery(id+"F0.wireOp",EDGE,"E227"),sQuery(id+"F0.wireOp",EDGE,"E228"),sQuery(id+"F0.wireOp",EDGE,"E229"),sQuery(id+"F0.wireOp",EDGE,"E230"),sQuery(id+"F0.wireOp",EDGE,"E231"),sQuery(id+"F0.wireOp",EDGE,"E232"),sQuery(id+"F0.wireOp",EDGE,"E233"),sQuery(id+"F0.wireOp",EDGE,"E234"),sQuery(id+"F0.wireOp",EDGE,"E235"),sQuery(id+"F0.wireOp",EDGE,"E236"),sQuery(id+"F0.wireOp",EDGE,"E237"),sQuery(id+"F0.wireOp",EDGE,"E238"),sQuery(id+"F0.wireOp",EDGE,"E239"),sQuery(id+"F0.wireOp",EDGE,"E240"),sQuery(id+"F0.wireOp",EDGE,"E241"),sQuery(id+"F0.wireOp",EDGE,"E242"),sQuery(id+"F0.wireOp",EDGE,"E243")])],"isStart":false});
            var Q1;
            Q1=makeQuery(id+"F1.opExtrude","CAP_FACE",FACE,{"disambiguationData":[OSD([sQuery(id+"F0.wireOp",EDGE,"E244"),sQuery(id+"F0.wireOp",EDGE,"E245"),sQuery(id+"F0.wireOp",EDGE,"E246"),sQuery(id+"F0.wireOp",EDGE,"E247"),sQuery(id+"F0.wireOp",EDGE,"E248"),sQuery(id+"F0.wireOp",EDGE,"E249"),sQuery(id+"F0.wireOp",EDGE,"E250"),sQuery(id+"F0.wireOp",EDGE,"E251"),sQuery(id+"F0.wireOp",EDGE,"E252"),sQuery(id+"F0.wireOp",EDGE,"E253"),sQuery(id+"F0.wireOp",EDGE,"E254"),sQuery(id+"F0.wireOp",EDGE,"E255"),sQuery(id+"F0.wireOp",EDGE,"E256"),sQuery(id+"F0.wireOp",EDGE,"E257"),sQuery(id+"F0.wireOp",EDGE,"E258"),sQuery(id+"F0.wireOp",EDGE,"E259"),sQuery(id+"F0.wireOp",EDGE,"E260"),sQuery(id+"F0.wireOp",EDGE,"E261"),sQuery(id+"F0.wireOp",EDGE,"E262"),sQuery(id+"F0.wireOp",EDGE,"E263"),sQuery(id+"F0.wireOp",EDGE,"E264"),sQuery(id+"F0.wireOp",EDGE,"E265"),sQuery(id+"F0.wireOp",EDGE,"E266"),sQuery(id+"F0.wireOp",EDGE,"E267"),sQuery(id+"F0.wireOp",EDGE,"E268"),sQuery(id+"F0.wireOp",EDGE,"E269"),sQuery(id+"F0.wireOp",EDGE,"E270"),sQuery(id+"F0.wireOp",EDGE,"E271"),sQuery(id+"F0.wireOp",EDGE,"E272"),sQuery(id+"F0.wireOp",EDGE,"E273"),sQuery(id+"F0.wireOp",EDGE,"E274"),sQuery(id+"F0.wireOp",EDGE,"E275"),sQuery(id+"F0.wireOp",EDGE,"E276"),sQuery(id+"F0.wireOp",EDGE,"E277"),sQuery(id+"F0.wireOp",EDGE,"E278"),sQuery(id+"F0.wireOp",EDGE,"E279"),sQuery(id+"F0.wireOp",EDGE,"E280"),sQuery(id+"F0.wireOp",EDGE,"E281"),sQuery(id+"F0.wireOp",EDGE,"E282"),sQuery(id+"F0.wireOp",EDGE,"E283"),sQuery(id+"F0.wireOp",EDGE,"E284"),sQuery(id+"F0.wireOp",EDGE,"E285"),sQuery(id+"F0.wireOp",EDGE,"E286"),sQuery(id+"F0.wireOp",EDGE,"E287"),sQuery(id+"F0.wireOp",EDGE,"E288"),sQuery(id+"F0.wireOp",EDGE,"E289"),sQuery(id+"F0.wireOp",EDGE,"E290"),sQuery(id+"F0.wireOp",EDGE,"E291"),sQuery(id+"F0.wireOp",EDGE,"E292"),sQuery(id+"F0.wireOp",EDGE,"E293"),sQuery(id+"F0.wireOp",EDGE,"E294"),sQuery(id+"F0.wireOp",EDGE,"E295"),sQuery(id+"F0.wireOp",EDGE,"E296"),sQuery(id+"F0.wireOp",EDGE,"E297"),sQuery(id+"F0.wireOp",EDGE,"E298"),sQuery(id+"F0.wireOp",EDGE,"E299"),sQuery(id+"F0.wireOp",EDGE,"E300"),sQuery(id+"F0.wireOp",EDGE,"E301"),sQuery(id+"F0.wireOp",EDGE,"E302"),sQuery(id+"F0.wireOp",EDGE,"E303"),sQuery(id+"F0.wireOp",EDGE,"E304"),sQuery(id+"F0.wireOp",EDGE,"E305"),sQuery(id+"F0.wireOp",EDGE,"E306"),sQuery(id+"F0.wireOp",EDGE,"E307"),sQuery(id+"F0.wireOp",EDGE,"E308"),sQuery(id+"F0.wireOp",EDGE,"E309"),sQuery(id+"F0.wireOp",EDGE,"E310"),sQuery(id+"F0.wireOp",EDGE,"E311"),sQuery(id+"F0.wireOp",EDGE,"E312"),sQuery(id+"F0.wireOp",EDGE,"E313"),sQuery(id+"F0.wireOp",EDGE,"E314"),sQuery(id+"F0.wireOp",EDGE,"E315"),sQuery(id+"F0.wireOp",EDGE,"E316"),sQuery(id+"F0.wireOp",EDGE,"E317"),sQuery(id+"F0.wireOp",EDGE,"E318"),sQuery(id+"F0.wireOp",EDGE,"E319"),sQuery(id+"F0.wireOp",EDGE,"E320"),sQuery(id+"F0.wireOp",EDGE,"E321"),sQuery(id+"F0.wireOp",EDGE,"E322"),sQuery(id+"F0.wireOp",EDGE,"E323"),sQuery(id+"F0.wireOp",EDGE,"E324"),sQuery(id+"F0.wireOp",EDGE,"E325"),sQuery(id+"F0.wireOp",EDGE,"E326"),sQuery(id+"F0.wireOp",EDGE,"E327"),sQuery(id+"F0.wireOp",EDGE,"E328"),sQuery(id+"F0.wireOp",EDGE,"E329"),sQuery(id+"F0.wireOp",EDGE,"E330"),sQuery(id+"F0.wireOp",EDGE,"E331"),sQuery(id+"F0.wireOp",EDGE,"E332"),sQuery(id+"F0.wireOp",EDGE,"E333"),sQuery(id+"F0.wireOp",EDGE,"E334"),sQuery(id+"F0.wireOp",EDGE,"E335"),sQuery(id+"F0.wireOp",EDGE,"E336"),sQuery(id+"F0.wireOp",EDGE,"E337"),sQuery(id+"F0.wireOp",EDGE,"E338"),sQuery(id+"F0.wireOp",EDGE,"E339"),sQuery(id+"F0.wireOp",EDGE,"E340"),sQuery(id+"F0.wireOp",EDGE,"E341"),sQuery(id+"F0.wireOp",EDGE,"E342"),sQuery(id+"F0.wireOp",EDGE,"E343"),sQuery(id+"F0.wireOp",EDGE,"E344"),sQuery(id+"F0.wireOp",EDGE,"E345"),sQuery(id+"F0.wireOp",EDGE,"E346"),sQuery(id+"F0.wireOp",EDGE,"E347"),sQuery(id+"F0.wireOp",EDGE,"E348"),sQuery(id+"F0.wireOp",EDGE,"E349"),sQuery(id+"F0.wireOp",EDGE,"E350"),sQuery(id+"F0.wireOp",EDGE,"E351"),sQuery(id+"F0.wireOp",EDGE,"E352"),sQuery(id+"F0.wireOp",EDGE,"E353"),sQuery(id+"F0.wireOp",EDGE,"E354"),sQuery(id+"F0.wireOp",EDGE,"E355"),sQuery(id+"F0.wireOp",EDGE,"E356"),sQuery(id+"F0.wireOp",EDGE,"E357"),sQuery(id+"F0.wireOp",EDGE,"E358"),sQuery(id+"F0.wireOp",EDGE,"E359"),sQuery(id+"F0.wireOp",EDGE,"E360"),sQuery(id+"F0.wireOp",EDGE,"E361"),sQuery(id+"F0.wireOp",EDGE,"E362"),sQuery(id+"F0.wireOp",EDGE,"E363"),sQuery(id+"F0.wireOp",EDGE,"E364"),sQuery(id+"F0.wireOp",EDGE,"E365"),sQuery(id+"F0.wireOp",EDGE,"E366"),sQuery(id+"F0.wireOp",EDGE,"E367"),sQuery(id+"F0.wireOp",EDGE,"E368"),sQuery(id+"F0.wireOp",EDGE,"E369"),sQuery(id+"F0.wireOp",EDGE,"E370"),sQuery(id+"F0.wireOp",EDGE,"E371"),sQuery(id+"F0.wireOp",EDGE,"E372"),sQuery(id+"F0.wireOp",EDGE,"E373"),sQuery(id+"F0.wireOp",EDGE,"E374"),sQuery(id+"F0.wireOp",EDGE,"E375"),sQuery(id+"F0.wireOp",EDGE,"E376"),sQuery(id+"F0.wireOp",EDGE,"E377"),sQuery(id+"F0.wireOp",EDGE,"E378"),sQuery(id+"F0.wireOp",EDGE,"E379"),sQuery(id+"F0.wireOp",EDGE,"E380"),sQuery(id+"F0.wireOp",EDGE,"E381"),sQuery(id+"F0.wireOp",EDGE,"E382"),sQuery(id+"F0.wireOp",EDGE,"E383"),sQuery(id+"F0.wireOp",EDGE,"E384"),sQuery(id+"F0.wireOp",EDGE,"E385"),sQuery(id+"F0.wireOp",EDGE,"E386"),sQuery(id+"F0.wireOp",EDGE,"E387"),sQuery(id+"F0.wireOp",EDGE,"E388"),sQuery(id+"F0.wireOp",EDGE,"E389"),sQuery(id+"F0.wireOp",EDGE,"E390"),sQuery(id+"F0.wireOp",EDGE,"E391"),sQuery(id+"F0.wireOp",EDGE,"E392"),sQuery(id+"F0.wireOp",EDGE,"E393"),sQuery(id+"F0.wireOp",EDGE,"E394"),sQuery(id+"F0.wireOp",EDGE,"E395"),sQuery(id+"F0.wireOp",EDGE,"E396"),sQuery(id+"F0.wireOp",EDGE,"E397"),sQuery(id+"F0.wireOp",EDGE,"E398"),sQuery(id+"F0.wireOp",EDGE,"E399"),sQuery(id+"F0.wireOp",EDGE,"E400"),sQuery(id+"F0.wireOp",EDGE,"E401"),sQuery(id+"F0.wireOp",EDGE,"E402"),sQuery(id+"F0.wireOp",EDGE,"E403"),sQuery(id+"F0.wireOp",EDGE,"E404"),sQuery(id+"F0.wireOp",EDGE,"E405"),sQuery(id+"F0.wireOp",EDGE,"E406"),sQuery(id+"F0.wireOp",EDGE,"E407"),sQuery(id+"F0.wireOp",EDGE,"E408"),sQuery(id+"F0.wireOp",EDGE,"E409"),sQuery(id+"F0.wireOp",EDGE,"E410"),sQuery(id+"F0.wireOp",EDGE,"E411"),sQuery(id+"F0.wireOp",EDGE,"E412"),sQuery(id+"F0.wireOp",EDGE,"E413"),sQuery(id+"F0.wireOp",EDGE,"E414"),sQuery(id+"F0.wireOp",EDGE,"E415"),sQuery(id+"F0.wireOp",EDGE,"E416"),sQuery(id+"F0.wireOp",EDGE,"E417"),sQuery(id+"F0.wireOp",EDGE,"E418"),sQuery(id+"F0.wireOp",EDGE,"E419"),sQuery(id+"F0.wireOp",EDGE,"E420"),sQuery(id+"F0.wireOp",EDGE,"E421"),sQuery(id+"F0.wireOp",EDGE,"E422"),sQuery(id+"F0.wireOp",EDGE,"E423"),sQuery(id+"F0.wireOp",EDGE,"E424"),sQuery(id+"F0.wireOp",EDGE,"E425"),sQuery(id+"F0.wireOp",EDGE,"E426"),sQuery(id+"F0.wireOp",EDGE,"E427"),sQuery(id+"F0.wireOp",EDGE,"E428"),sQuery(id+"F0.wireOp",EDGE,"E429"),sQuery(id+"F0.wireOp",EDGE,"E430"),sQuery(id+"F0.wireOp",EDGE,"E431"),sQuery(id+"F0.wireOp",EDGE,"E432"),sQuery(id+"F0.wireOp",EDGE,"E433"),sQuery(id+"F0.wireOp",EDGE,"E434"),sQuery(id+"F0.wireOp",EDGE,"E435"),sQuery(id+"F0.wireOp",EDGE,"E436"),sQuery(id+"F0.wireOp",EDGE,"E437"),sQuery(id+"F0.wireOp",EDGE,"E438"),sQuery(id+"F0.wireOp",EDGE,"E439"),sQuery(id+"F0.wireOp",EDGE,"E440"),sQuery(id+"F0.wireOp",EDGE,"E441"),sQuery(id+"F0.wireOp",EDGE,"E442"),sQuery(id+"F0.wireOp",EDGE,"E443"),sQuery(id+"F0.wireOp",EDGE,"E444"),sQuery(id+"F0.wireOp",EDGE,"E445"),sQuery(id+"F0.wireOp",EDGE,"E446"),sQuery(id+"F0.wireOp",EDGE,"E447"),sQuery(id+"F0.wireOp",EDGE,"E448"),sQuery(id+"F0.wireOp",EDGE,"E449"),sQuery(id+"F0.wireOp",EDGE,"E450"),sQuery(id+"F0.wireOp",EDGE,"E451"),sQuery(id+"F0.wireOp",EDGE,"E452"),sQuery(id+"F0.wireOp",EDGE,"E453"),sQuery(id+"F0.wireOp",EDGE,"E454"),sQuery(id+"F0.wireOp",EDGE,"E455"),sQuery(id+"F0.wireOp",EDGE,"E456"),sQuery(id+"F0.wireOp",EDGE,"E457"),sQuery(id+"F0.wireOp",EDGE,"E458"),sQuery(id+"F0.wireOp",EDGE,"E459"),sQuery(id+"F0.wireOp",EDGE,"E460"),sQuery(id+"F0.wireOp",EDGE,"E461"),sQuery(id+"F0.wireOp",EDGE,"E462"),sQuery(id+"F0.wireOp",EDGE,"E463"),sQuery(id+"F0.wireOp",EDGE,"E464"),sQuery(id+"F0.wireOp",EDGE,"E465"),sQuery(id+"F0.wireOp",EDGE,"E466"),sQuery(id+"F0.wireOp",EDGE,"E467"),sQuery(id+"F0.wireOp",EDGE,"E468"),sQuery(id+"F0.wireOp",EDGE,"E469"),sQuery(id+"F0.wireOp",EDGE,"E470"),sQuery(id+"F0.wireOp",EDGE,"E471"),sQuery(id+"F0.wireOp",EDGE,"E472"),sQuery(id+"F0.wireOp",EDGE,"E473"),sQuery(id+"F0.wireOp",EDGE,"E474"),sQuery(id+"F0.wireOp",EDGE,"E475"),sQuery(id+"F0.wireOp",EDGE,"E476"),sQuery(id+"F0.wireOp",EDGE,"E477"),sQuery(id+"F0.wireOp",EDGE,"E478"),sQuery(id+"F0.wireOp",EDGE,"E479"),sQuery(id+"F0.wireOp",EDGE,"E480"),sQuery(id+"F0.wireOp",EDGE,"E481"),sQuery(id+"F0.wireOp",EDGE,"E482"),sQuery(id+"F0.wireOp",EDGE,"E483"),sQuery(id+"F0.wireOp",EDGE,"E484"),sQuery(id+"F0.wireOp",EDGE,"E485"),sQuery(id+"F0.wireOp",EDGE,"E486"),sQuery(id+"F0.wireOp",EDGE,"E487"),sQuery(id+"F0.wireOp",EDGE,"E488"),sQuery(id+"F0.wireOp",EDGE,"E489"),sQuery(id+"F0.wireOp",EDGE,"E490"),sQuery(id+"F0.wireOp",EDGE,"E491"),sQuery(id+"F0.wireOp",EDGE,"E492"),sQuery(id+"F0.wireOp",EDGE,"E493"),sQuery(id+"F0.wireOp",EDGE,"E494"),sQuery(id+"F0.wireOp",EDGE,"E495"),sQuery(id+"F0.wireOp",EDGE,"E496"),sQuery(id+"F0.wireOp",EDGE,"E497"),sQuery(id+"F0.wireOp",EDGE,"E498"),sQuery(id+"F0.wireOp",EDGE,"E499"),sQuery(id+"F0.wireOp",EDGE,"E500"),sQuery(id+"F0.wireOp",EDGE,"E501"),sQuery(id+"F0.wireOp",EDGE,"E502"),sQuery(id+"F0.wireOp",EDGE,"E503"),sQuery(id+"F0.wireOp",EDGE,"E504"),sQuery(id+"F0.wireOp",EDGE,"E505"),sQuery(id+"F0.wireOp",EDGE,"E506"),sQuery(id+"F0.wireOp",EDGE,"E507"),sQuery(id+"F0.wireOp",EDGE,"E508"),sQuery(id+"F0.wireOp",EDGE,"E509"),sQuery(id+"F0.wireOp",EDGE,"E510"),sQuery(id+"F0.wireOp",EDGE,"E511"),sQuery(id+"F0.wireOp",EDGE,"E512"),sQuery(id+"F0.wireOp",EDGE,"E513"),sQuery(id+"F0.wireOp",EDGE,"E514"),sQuery(id+"F0.wireOp",EDGE,"E515"),sQuery(id+"F0.wireOp",EDGE,"E516"),sQuery(id+"F0.wireOp",EDGE,"E517"),sQuery(id+"F0.wireOp",EDGE,"E518"),sQuery(id+"F0.wireOp",EDGE,"E519"),sQuery(id+"F0.wireOp",EDGE,"E520"),sQuery(id+"F0.wireOp",EDGE,"E521"),sQuery(id+"F0.wireOp",EDGE,"E522"),sQuery(id+"F0.wireOp",EDGE,"E523"),sQuery(id+"F0.wireOp",EDGE,"E524"),sQuery(id+"F0.wireOp",EDGE,"E525"),sQuery(id+"F0.wireOp",EDGE,"E526"),sQuery(id+"F0.wireOp",EDGE,"E527"),sQuery(id+"F0.wireOp",EDGE,"E528"),sQuery(id+"F0.wireOp",EDGE,"E529"),sQuery(id+"F0.wireOp",EDGE,"E530"),sQuery(id+"F0.wireOp",EDGE,"E531"),sQuery(id+"F0.wireOp",EDGE,"E532"),sQuery(id+"F0.wireOp",EDGE,"E533"),sQuery(id+"F0.wireOp",EDGE,"E534"),sQuery(id+"F0.wireOp",EDGE,"E535"),sQuery(id+"F0.wireOp",EDGE,"E536"),sQuery(id+"F0.wireOp",EDGE,"E537"),sQuery(id+"F0.wireOp",EDGE,"E538"),sQuery(id+"F0.wireOp",EDGE,"E539"),sQuery(id+"F0.wireOp",EDGE,"E540"),sQuery(id+"F0.wireOp",EDGE,"E541"),sQuery(id+"F0.wireOp",EDGE,"E542"),sQuery(id+"F0.wireOp",EDGE,"E543"),sQuery(id+"F0.wireOp",EDGE,"E544"),sQuery(id+"F0.wireOp",EDGE,"E545"),sQuery(id+"F0.wireOp",EDGE,"E546"),sQuery(id+"F0.wireOp",EDGE,"E547"),sQuery(id+"F0.wireOp",EDGE,"E548"),sQuery(id+"F0.wireOp",EDGE,"E549"),sQuery(id+"F0.wireOp",EDGE,"E550"),sQuery(id+"F0.wireOp",EDGE,"E551"),sQuery(id+"F0.wireOp",EDGE,"E552"),sQuery(id+"F0.wireOp",EDGE,"E553"),sQuery(id+"F0.wireOp",EDGE,"E554"),sQuery(id+"F0.wireOp",EDGE,"E555"),sQuery(id+"F0.wireOp",EDGE,"E556"),sQuery(id+"F0.wireOp",EDGE,"E557"),sQuery(id+"F0.wireOp",EDGE,"E558"),sQuery(id+"F0.wireOp",EDGE,"E559"),sQuery(id+"F0.wireOp",EDGE,"E560"),sQuery(id+"F0.wireOp",EDGE,"E561"),sQuery(id+"F0.wireOp",EDGE,"E562"),sQuery(id+"F0.wireOp",EDGE,"E563"),sQuery(id+"F0.wireOp",EDGE,"E564"),sQuery(id+"F0.wireOp",EDGE,"E565"),sQuery(id+"F0.wireOp",EDGE,"E566"),sQuery(id+"F0.wireOp",EDGE,"E567"),sQuery(id+"F0.wireOp",EDGE,"E568"),sQuery(id+"F0.wireOp",EDGE,"E569"),sQuery(id+"F0.wireOp",EDGE,"E570"),sQuery(id+"F0.wireOp",EDGE,"E571"),sQuery(id+"F0.wireOp",EDGE,"E572"),sQuery(id+"F0.wireOp",EDGE,"E573"),sQuery(id+"F0.wireOp",EDGE,"E574"),sQuery(id+"F0.wireOp",EDGE,"E575"),sQuery(id+"F0.wireOp",EDGE,"E576"),sQuery(id+"F0.wireOp",EDGE,"E577"),sQuery(id+"F0.wireOp",EDGE,"E578"),sQuery(id+"F0.wireOp",EDGE,"E579"),sQuery(id+"F0.wireOp",EDGE,"E580"),sQuery(id+"F0.wireOp",EDGE,"E581"),sQuery(id+"F0.wireOp",EDGE,"E582"),sQuery(id+"F0.wireOp",EDGE,"E583"),sQuery(id+"F0.wireOp",EDGE,"E584"),sQuery(id+"F0.wireOp",EDGE,"E585"),sQuery(id+"F0.wireOp",EDGE,"E586"),sQuery(id+"F0.wireOp",EDGE,"E587"),sQuery(id+"F0.wireOp",EDGE,"E588"),sQuery(id+"F0.wireOp",EDGE,"E589"),sQuery(id+"F0.wireOp",EDGE,"E590"),sQuery(id+"F0.wireOp",EDGE,"E591"),sQuery(id+"F0.wireOp",EDGE,"E592"),sQuery(id+"F0.wireOp",EDGE,"E593"),sQuery(id+"F0.wireOp",EDGE,"E594"),sQuery(id+"F0.wireOp",EDGE,"E595"),sQuery(id+"F0.wireOp",EDGE,"E596"),sQuery(id+"F0.wireOp",EDGE,"E597"),sQuery(id+"F0.wireOp",EDGE,"E598"),sQuery(id+"F0.wireOp",EDGE,"E599"),sQuery(id+"F0.wireOp",EDGE,"E600"),sQuery(id+"F0.wireOp",EDGE,"E601"),sQuery(id+"F0.wireOp",EDGE,"E602"),sQuery(id+"F0.wireOp",EDGE,"E603"),sQuery(id+"F0.wireOp",EDGE,"E604"),sQuery(id+"F0.wireOp",EDGE,"E605"),sQuery(id+"F0.wireOp",EDGE,"E606"),sQuery(id+"F0.wireOp",EDGE,"E607"),sQuery(id+"F0.wireOp",EDGE,"E608"),sQuery(id+"F0.wireOp",EDGE,"E609"),sQuery(id+"F0.wireOp",EDGE,"E610"),sQuery(id+"F0.wireOp",EDGE,"E611"),sQuery(id+"F0.wireOp",EDGE,"E612"),sQuery(id+"F0.wireOp",EDGE,"E613"),sQuery(id+"F0.wireOp",EDGE,"E614"),sQuery(id+"F0.wireOp",EDGE,"E615"),sQuery(id+"F0.wireOp",EDGE,"E616"),sQuery(id+"F0.wireOp",EDGE,"E617"),sQuery(id+"F0.wireOp",EDGE,"E618"),sQuery(id+"F0.wireOp",EDGE,"E619"),sQuery(id+"F0.wireOp",EDGE,"E620"),sQuery(id+"F0.wireOp",EDGE,"E621"),sQuery(id+"F0.wireOp",EDGE,"E622"),sQuery(id+"F0.wireOp",EDGE,"E623"),sQuery(id+"F0.wireOp",EDGE,"E624"),sQuery(id+"F0.wireOp",EDGE,"E625"),sQuery(id+"F0.wireOp",EDGE,"E626"),sQuery(id+"F0.wireOp",EDGE,"E627"),sQuery(id+"F0.wireOp",EDGE,"E628"),sQuery(id+"F0.wireOp",EDGE,"E629"),sQuery(id+"F0.wireOp",EDGE,"E630"),sQuery(id+"F0.wireOp",EDGE,"E631"),sQuery(id+"F0.wireOp",EDGE,"E632"),sQuery(id+"F0.wireOp",EDGE,"E633"),sQuery(id+"F0.wireOp",EDGE,"E634"),sQuery(id+"F0.wireOp",EDGE,"E635")])],"isStart":false});
            chamfer(context, id + "F6", {"entities" : qUnion([Q0, Q1]), "width" : 0.05 * mm, "tangentPropagation" : true});
        }
        {
            var Q0;
            Q0=qCreatedBy(makeId("Front.planeOp"),FACE);
            var sketch = newSketch(context, id + "F7", { "sketchPlane" : qUnion([Q0])});
            skLineSegment(sketch, "E636", {"start": v(0, 0) * mm, "end": v(0, 4.2) * mm});
            skSolve(sketch);
        }
        {
            var Q0;
            Q0=sQuery(id+"F7.wireOp",VERTEX,"E636.end");
            var Q1;
            Q1=makeQuery(id+"F1.opExtrude","SWEPT_BODY",BODY,{"disambiguationData":[OSD([sQuery(id+"F0.wireOp",EDGE,"E244"),sQuery(id+"F0.wireOp",EDGE,"E245"),sQuery(id+"F0.wireOp",EDGE,"E246"),sQuery(id+"F0.wireOp",EDGE,"E247"),sQuery(id+"F0.wireOp",EDGE,"E248"),sQuery(id+"F0.wireOp",EDGE,"E249"),sQuery(id+"F0.wireOp",EDGE,"E250"),sQuery(id+"F0.wireOp",EDGE,"E251"),sQuery(id+"F0.wireOp",EDGE,"E252"),sQuery(id+"F0.wireOp",EDGE,"E253"),sQuery(id+"F0.wireOp",EDGE,"E254"),sQuery(id+"F0.wireOp",EDGE,"E255"),sQuery(id+"F0.wireOp",EDGE,"E256"),sQuery(id+"F0.wireOp",EDGE,"E257"),sQuery(id+"F0.wireOp",EDGE,"E258"),sQuery(id+"F0.wireOp",EDGE,"E259"),sQuery(id+"F0.wireOp",EDGE,"E260"),sQuery(id+"F0.wireOp",EDGE,"E261"),sQuery(id+"F0.wireOp",EDGE,"E262"),sQuery(id+"F0.wireOp",EDGE,"E263"),sQuery(id+"F0.wireOp",EDGE,"E264"),sQuery(id+"F0.wireOp",EDGE,"E265"),sQuery(id+"F0.wireOp",EDGE,"E266"),sQuery(id+"F0.wireOp",EDGE,"E267"),sQuery(id+"F0.wireOp",EDGE,"E268"),sQuery(id+"F0.wireOp",EDGE,"E269"),sQuery(id+"F0.wireOp",EDGE,"E270"),sQuery(id+"F0.wireOp",EDGE,"E271"),sQuery(id+"F0.wireOp",EDGE,"E272"),sQuery(id+"F0.wireOp",EDGE,"E273"),sQuery(id+"F0.wireOp",EDGE,"E274"),sQuery(id+"F0.wireOp",EDGE,"E275"),sQuery(id+"F0.wireOp",EDGE,"E276"),sQuery(id+"F0.wireOp",EDGE,"E277"),sQuery(id+"F0.wireOp",EDGE,"E278"),sQuery(id+"F0.wireOp",EDGE,"E279"),sQuery(id+"F0.wireOp",EDGE,"E280"),sQuery(id+"F0.wireOp",EDGE,"E281"),sQuery(id+"F0.wireOp",EDGE,"E282"),sQuery(id+"F0.wireOp",EDGE,"E283"),sQuery(id+"F0.wireOp",EDGE,"E284"),sQuery(id+"F0.wireOp",EDGE,"E285"),sQuery(id+"F0.wireOp",EDGE,"E286"),sQuery(id+"F0.wireOp",EDGE,"E287"),sQuery(id+"F0.wireOp",EDGE,"E288"),sQuery(id+"F0.wireOp",EDGE,"E289"),sQuery(id+"F0.wireOp",EDGE,"E290"),sQuery(id+"F0.wireOp",EDGE,"E291"),sQuery(id+"F0.wireOp",EDGE,"E292"),sQuery(id+"F0.wireOp",EDGE,"E293"),sQuery(id+"F0.wireOp",EDGE,"E294"),sQuery(id+"F0.wireOp",EDGE,"E295"),sQuery(id+"F0.wireOp",EDGE,"E296"),sQuery(id+"F0.wireOp",EDGE,"E297"),sQuery(id+"F0.wireOp",EDGE,"E298"),sQuery(id+"F0.wireOp",EDGE,"E299"),sQuery(id+"F0.wireOp",EDGE,"E300"),sQuery(id+"F0.wireOp",EDGE,"E301"),sQuery(id+"F0.wireOp",EDGE,"E302"),sQuery(id+"F0.wireOp",EDGE,"E303"),sQuery(id+"F0.wireOp",EDGE,"E304"),sQuery(id+"F0.wireOp",EDGE,"E305"),sQuery(id+"F0.wireOp",EDGE,"E306"),sQuery(id+"F0.wireOp",EDGE,"E307"),sQuery(id+"F0.wireOp",EDGE,"E308"),sQuery(id+"F0.wireOp",EDGE,"E309"),sQuery(id+"F0.wireOp",EDGE,"E310"),sQuery(id+"F0.wireOp",EDGE,"E311"),sQuery(id+"F0.wireOp",EDGE,"E312"),sQuery(id+"F0.wireOp",EDGE,"E313"),sQuery(id+"F0.wireOp",EDGE,"E314"),sQuery(id+"F0.wireOp",EDGE,"E315"),sQuery(id+"F0.wireOp",EDGE,"E316"),sQuery(id+"F0.wireOp",EDGE,"E317"),sQuery(id+"F0.wireOp",EDGE,"E318"),sQuery(id+"F0.wireOp",EDGE,"E319"),sQuery(id+"F0.wireOp",EDGE,"E320"),sQuery(id+"F0.wireOp",EDGE,"E321"),sQuery(id+"F0.wireOp",EDGE,"E322"),sQuery(id+"F0.wireOp",EDGE,"E323"),sQuery(id+"F0.wireOp",EDGE,"E324"),sQuery(id+"F0.wireOp",EDGE,"E325"),sQuery(id+"F0.wireOp",EDGE,"E326"),sQuery(id+"F0.wireOp",EDGE,"E327"),sQuery(id+"F0.wireOp",EDGE,"E328"),sQuery(id+"F0.wireOp",EDGE,"E329"),sQuery(id+"F0.wireOp",EDGE,"E330"),sQuery(id+"F0.wireOp",EDGE,"E331"),sQuery(id+"F0.wireOp",EDGE,"E332"),sQuery(id+"F0.wireOp",EDGE,"E333"),sQuery(id+"F0.wireOp",EDGE,"E334"),sQuery(id+"F0.wireOp",EDGE,"E335"),sQuery(id+"F0.wireOp",EDGE,"E336"),sQuery(id+"F0.wireOp",EDGE,"E337"),sQuery(id+"F0.wireOp",EDGE,"E338"),sQuery(id+"F0.wireOp",EDGE,"E339"),sQuery(id+"F0.wireOp",EDGE,"E340"),sQuery(id+"F0.wireOp",EDGE,"E341"),sQuery(id+"F0.wireOp",EDGE,"E342"),sQuery(id+"F0.wireOp",EDGE,"E343"),sQuery(id+"F0.wireOp",EDGE,"E344"),sQuery(id+"F0.wireOp",EDGE,"E345"),sQuery(id+"F0.wireOp",EDGE,"E346"),sQuery(id+"F0.wireOp",EDGE,"E347"),sQuery(id+"F0.wireOp",EDGE,"E348"),sQuery(id+"F0.wireOp",EDGE,"E349"),sQuery(id+"F0.wireOp",EDGE,"E350"),sQuery(id+"F0.wireOp",EDGE,"E351"),sQuery(id+"F0.wireOp",EDGE,"E352"),sQuery(id+"F0.wireOp",EDGE,"E353"),sQuery(id+"F0.wireOp",EDGE,"E354"),sQuery(id+"F0.wireOp",EDGE,"E355"),sQuery(id+"F0.wireOp",EDGE,"E356"),sQuery(id+"F0.wireOp",EDGE,"E357"),sQuery(id+"F0.wireOp",EDGE,"E358"),sQuery(id+"F0.wireOp",EDGE,"E359"),sQuery(id+"F0.wireOp",EDGE,"E360"),sQuery(id+"F0.wireOp",EDGE,"E361"),sQuery(id+"F0.wireOp",EDGE,"E362"),sQuery(id+"F0.wireOp",EDGE,"E363"),sQuery(id+"F0.wireOp",EDGE,"E364"),sQuery(id+"F0.wireOp",EDGE,"E365"),sQuery(id+"F0.wireOp",EDGE,"E366"),sQuery(id+"F0.wireOp",EDGE,"E367"),sQuery(id+"F0.wireOp",EDGE,"E368"),sQuery(id+"F0.wireOp",EDGE,"E369"),sQuery(id+"F0.wireOp",EDGE,"E370"),sQuery(id+"F0.wireOp",EDGE,"E371"),sQuery(id+"F0.wireOp",EDGE,"E372"),sQuery(id+"F0.wireOp",EDGE,"E373"),sQuery(id+"F0.wireOp",EDGE,"E374"),sQuery(id+"F0.wireOp",EDGE,"E375"),sQuery(id+"F0.wireOp",EDGE,"E376"),sQuery(id+"F0.wireOp",EDGE,"E377"),sQuery(id+"F0.wireOp",EDGE,"E378"),sQuery(id+"F0.wireOp",EDGE,"E379"),sQuery(id+"F0.wireOp",EDGE,"E380"),sQuery(id+"F0.wireOp",EDGE,"E381"),sQuery(id+"F0.wireOp",EDGE,"E382"),sQuery(id+"F0.wireOp",EDGE,"E383"),sQuery(id+"F0.wireOp",EDGE,"E384"),sQuery(id+"F0.wireOp",EDGE,"E385"),sQuery(id+"F0.wireOp",EDGE,"E386"),sQuery(id+"F0.wireOp",EDGE,"E387"),sQuery(id+"F0.wireOp",EDGE,"E388"),sQuery(id+"F0.wireOp",EDGE,"E389"),sQuery(id+"F0.wireOp",EDGE,"E390"),sQuery(id+"F0.wireOp",EDGE,"E391"),sQuery(id+"F0.wireOp",EDGE,"E392"),sQuery(id+"F0.wireOp",EDGE,"E393"),sQuery(id+"F0.wireOp",EDGE,"E394"),sQuery(id+"F0.wireOp",EDGE,"E395"),sQuery(id+"F0.wireOp",EDGE,"E396"),sQuery(id+"F0.wireOp",EDGE,"E397"),sQuery(id+"F0.wireOp",EDGE,"E398"),sQuery(id+"F0.wireOp",EDGE,"E399"),sQuery(id+"F0.wireOp",EDGE,"E400"),sQuery(id+"F0.wireOp",EDGE,"E401"),sQuery(id+"F0.wireOp",EDGE,"E402"),sQuery(id+"F0.wireOp",EDGE,"E403"),sQuery(id+"F0.wireOp",EDGE,"E404"),sQuery(id+"F0.wireOp",EDGE,"E405"),sQuery(id+"F0.wireOp",EDGE,"E406"),sQuery(id+"F0.wireOp",EDGE,"E407"),sQuery(id+"F0.wireOp",EDGE,"E408"),sQuery(id+"F0.wireOp",EDGE,"E409"),sQuery(id+"F0.wireOp",EDGE,"E410"),sQuery(id+"F0.wireOp",EDGE,"E411"),sQuery(id+"F0.wireOp",EDGE,"E412"),sQuery(id+"F0.wireOp",EDGE,"E413"),sQuery(id+"F0.wireOp",EDGE,"E414"),sQuery(id+"F0.wireOp",EDGE,"E415"),sQuery(id+"F0.wireOp",EDGE,"E416"),sQuery(id+"F0.wireOp",EDGE,"E417"),sQuery(id+"F0.wireOp",EDGE,"E418"),sQuery(id+"F0.wireOp",EDGE,"E419"),sQuery(id+"F0.wireOp",EDGE,"E420"),sQuery(id+"F0.wireOp",EDGE,"E421"),sQuery(id+"F0.wireOp",EDGE,"E422"),sQuery(id+"F0.wireOp",EDGE,"E423"),sQuery(id+"F0.wireOp",EDGE,"E424"),sQuery(id+"F0.wireOp",EDGE,"E425"),sQuery(id+"F0.wireOp",EDGE,"E426"),sQuery(id+"F0.wireOp",EDGE,"E427"),sQuery(id+"F0.wireOp",EDGE,"E428"),sQuery(id+"F0.wireOp",EDGE,"E429"),sQuery(id+"F0.wireOp",EDGE,"E430"),sQuery(id+"F0.wireOp",EDGE,"E431"),sQuery(id+"F0.wireOp",EDGE,"E432"),sQuery(id+"F0.wireOp",EDGE,"E433"),sQuery(id+"F0.wireOp",EDGE,"E434"),sQuery(id+"F0.wireOp",EDGE,"E435"),sQuery(id+"F0.wireOp",EDGE,"E436"),sQuery(id+"F0.wireOp",EDGE,"E437"),sQuery(id+"F0.wireOp",EDGE,"E438"),sQuery(id+"F0.wireOp",EDGE,"E439"),sQuery(id+"F0.wireOp",EDGE,"E440"),sQuery(id+"F0.wireOp",EDGE,"E441"),sQuery(id+"F0.wireOp",EDGE,"E442"),sQuery(id+"F0.wireOp",EDGE,"E443"),sQuery(id+"F0.wireOp",EDGE,"E444"),sQuery(id+"F0.wireOp",EDGE,"E445"),sQuery(id+"F0.wireOp",EDGE,"E446"),sQuery(id+"F0.wireOp",EDGE,"E447"),sQuery(id+"F0.wireOp",EDGE,"E448"),sQuery(id+"F0.wireOp",EDGE,"E449"),sQuery(id+"F0.wireOp",EDGE,"E450"),sQuery(id+"F0.wireOp",EDGE,"E451"),sQuery(id+"F0.wireOp",EDGE,"E452"),sQuery(id+"F0.wireOp",EDGE,"E453"),sQuery(id+"F0.wireOp",EDGE,"E454"),sQuery(id+"F0.wireOp",EDGE,"E455"),sQuery(id+"F0.wireOp",EDGE,"E456"),sQuery(id+"F0.wireOp",EDGE,"E457"),sQuery(id+"F0.wireOp",EDGE,"E458"),sQuery(id+"F0.wireOp",EDGE,"E459"),sQuery(id+"F0.wireOp",EDGE,"E460"),sQuery(id+"F0.wireOp",EDGE,"E461"),sQuery(id+"F0.wireOp",EDGE,"E462"),sQuery(id+"F0.wireOp",EDGE,"E463"),sQuery(id+"F0.wireOp",EDGE,"E464"),sQuery(id+"F0.wireOp",EDGE,"E465"),sQuery(id+"F0.wireOp",EDGE,"E466"),sQuery(id+"F0.wireOp",EDGE,"E467"),sQuery(id+"F0.wireOp",EDGE,"E468"),sQuery(id+"F0.wireOp",EDGE,"E469"),sQuery(id+"F0.wireOp",EDGE,"E470"),sQuery(id+"F0.wireOp",EDGE,"E471"),sQuery(id+"F0.wireOp",EDGE,"E472"),sQuery(id+"F0.wireOp",EDGE,"E473"),sQuery(id+"F0.wireOp",EDGE,"E474"),sQuery(id+"F0.wireOp",EDGE,"E475"),sQuery(id+"F0.wireOp",EDGE,"E476"),sQuery(id+"F0.wireOp",EDGE,"E477"),sQuery(id+"F0.wireOp",EDGE,"E478"),sQuery(id+"F0.wireOp",EDGE,"E479"),sQuery(id+"F0.wireOp",EDGE,"E480"),sQuery(id+"F0.wireOp",EDGE,"E481"),sQuery(id+"F0.wireOp",EDGE,"E482"),sQuery(id+"F0.wireOp",EDGE,"E483"),sQuery(id+"F0.wireOp",EDGE,"E484"),sQuery(id+"F0.wireOp",EDGE,"E485"),sQuery(id+"F0.wireOp",EDGE,"E486"),sQuery(id+"F0.wireOp",EDGE,"E487"),sQuery(id+"F0.wireOp",EDGE,"E488"),sQuery(id+"F0.wireOp",EDGE,"E489"),sQuery(id+"F0.wireOp",EDGE,"E490"),sQuery(id+"F0.wireOp",EDGE,"E491"),sQuery(id+"F0.wireOp",EDGE,"E492"),sQuery(id+"F0.wireOp",EDGE,"E493"),sQuery(id+"F0.wireOp",EDGE,"E494"),sQuery(id+"F0.wireOp",EDGE,"E495"),sQuery(id+"F0.wireOp",EDGE,"E496"),sQuery(id+"F0.wireOp",EDGE,"E497"),sQuery(id+"F0.wireOp",EDGE,"E498"),sQuery(id+"F0.wireOp",EDGE,"E499"),sQuery(id+"F0.wireOp",EDGE,"E500"),sQuery(id+"F0.wireOp",EDGE,"E501"),sQuery(id+"F0.wireOp",EDGE,"E502"),sQuery(id+"F0.wireOp",EDGE,"E503"),sQuery(id+"F0.wireOp",EDGE,"E504"),sQuery(id+"F0.wireOp",EDGE,"E505"),sQuery(id+"F0.wireOp",EDGE,"E506"),sQuery(id+"F0.wireOp",EDGE,"E507"),sQuery(id+"F0.wireOp",EDGE,"E508"),sQuery(id+"F0.wireOp",EDGE,"E509"),sQuery(id+"F0.wireOp",EDGE,"E510"),sQuery(id+"F0.wireOp",EDGE,"E511"),sQuery(id+"F0.wireOp",EDGE,"E512"),sQuery(id+"F0.wireOp",EDGE,"E513"),sQuery(id+"F0.wireOp",EDGE,"E514"),sQuery(id+"F0.wireOp",EDGE,"E515"),sQuery(id+"F0.wireOp",EDGE,"E516"),sQuery(id+"F0.wireOp",EDGE,"E517"),sQuery(id+"F0.wireOp",EDGE,"E518"),sQuery(id+"F0.wireOp",EDGE,"E519"),sQuery(id+"F0.wireOp",EDGE,"E520"),sQuery(id+"F0.wireOp",EDGE,"E521"),sQuery(id+"F0.wireOp",EDGE,"E522"),sQuery(id+"F0.wireOp",EDGE,"E523"),sQuery(id+"F0.wireOp",EDGE,"E524"),sQuery(id+"F0.wireOp",EDGE,"E525"),sQuery(id+"F0.wireOp",EDGE,"E526"),sQuery(id+"F0.wireOp",EDGE,"E527"),sQuery(id+"F0.wireOp",EDGE,"E528"),sQuery(id+"F0.wireOp",EDGE,"E529"),sQuery(id+"F0.wireOp",EDGE,"E530"),sQuery(id+"F0.wireOp",EDGE,"E531"),sQuery(id+"F0.wireOp",EDGE,"E532"),sQuery(id+"F0.wireOp",EDGE,"E533"),sQuery(id+"F0.wireOp",EDGE,"E534"),sQuery(id+"F0.wireOp",EDGE,"E535"),sQuery(id+"F0.wireOp",EDGE,"E536"),sQuery(id+"F0.wireOp",EDGE,"E537"),sQuery(id+"F0.wireOp",EDGE,"E538"),sQuery(id+"F0.wireOp",EDGE,"E539"),sQuery(id+"F0.wireOp",EDGE,"E540"),sQuery(id+"F0.wireOp",EDGE,"E541"),sQuery(id+"F0.wireOp",EDGE,"E542"),sQuery(id+"F0.wireOp",EDGE,"E543"),sQuery(id+"F0.wireOp",EDGE,"E544"),sQuery(id+"F0.wireOp",EDGE,"E545"),sQuery(id+"F0.wireOp",EDGE,"E546"),sQuery(id+"F0.wireOp",EDGE,"E547"),sQuery(id+"F0.wireOp",EDGE,"E548"),sQuery(id+"F0.wireOp",EDGE,"E549"),sQuery(id+"F0.wireOp",EDGE,"E550"),sQuery(id+"F0.wireOp",EDGE,"E551"),sQuery(id+"F0.wireOp",EDGE,"E552"),sQuery(id+"F0.wireOp",EDGE,"E553"),sQuery(id+"F0.wireOp",EDGE,"E554"),sQuery(id+"F0.wireOp",EDGE,"E555"),sQuery(id+"F0.wireOp",EDGE,"E556"),sQuery(id+"F0.wireOp",EDGE,"E557"),sQuery(id+"F0.wireOp",EDGE,"E558"),sQuery(id+"F0.wireOp",EDGE,"E559"),sQuery(id+"F0.wireOp",EDGE,"E560"),sQuery(id+"F0.wireOp",EDGE,"E561"),sQuery(id+"F0.wireOp",EDGE,"E562"),sQuery(id+"F0.wireOp",EDGE,"E563"),sQuery(id+"F0.wireOp",EDGE,"E564"),sQuery(id+"F0.wireOp",EDGE,"E565"),sQuery(id+"F0.wireOp",EDGE,"E566"),sQuery(id+"F0.wireOp",EDGE,"E567"),sQuery(id+"F0.wireOp",EDGE,"E568"),sQuery(id+"F0.wireOp",EDGE,"E569"),sQuery(id+"F0.wireOp",EDGE,"E570"),sQuery(id+"F0.wireOp",EDGE,"E571"),sQuery(id+"F0.wireOp",EDGE,"E572"),sQuery(id+"F0.wireOp",EDGE,"E573"),sQuery(id+"F0.wireOp",EDGE,"E574"),sQuery(id+"F0.wireOp",EDGE,"E575"),sQuery(id+"F0.wireOp",EDGE,"E576"),sQuery(id+"F0.wireOp",EDGE,"E577"),sQuery(id+"F0.wireOp",EDGE,"E578"),sQuery(id+"F0.wireOp",EDGE,"E579"),sQuery(id+"F0.wireOp",EDGE,"E580"),sQuery(id+"F0.wireOp",EDGE,"E581"),sQuery(id+"F0.wireOp",EDGE,"E582"),sQuery(id+"F0.wireOp",EDGE,"E583"),sQuery(id+"F0.wireOp",EDGE,"E584"),sQuery(id+"F0.wireOp",EDGE,"E585"),sQuery(id+"F0.wireOp",EDGE,"E586"),sQuery(id+"F0.wireOp",EDGE,"E587"),sQuery(id+"F0.wireOp",EDGE,"E588"),sQuery(id+"F0.wireOp",EDGE,"E589"),sQuery(id+"F0.wireOp",EDGE,"E590"),sQuery(id+"F0.wireOp",EDGE,"E591"),sQuery(id+"F0.wireOp",EDGE,"E592"),sQuery(id+"F0.wireOp",EDGE,"E593"),sQuery(id+"F0.wireOp",EDGE,"E594"),sQuery(id+"F0.wireOp",EDGE,"E595"),sQuery(id+"F0.wireOp",EDGE,"E596"),sQuery(id+"F0.wireOp",EDGE,"E597"),sQuery(id+"F0.wireOp",EDGE,"E598"),sQuery(id+"F0.wireOp",EDGE,"E599"),sQuery(id+"F0.wireOp",EDGE,"E600"),sQuery(id+"F0.wireOp",EDGE,"E601"),sQuery(id+"F0.wireOp",EDGE,"E602"),sQuery(id+"F0.wireOp",EDGE,"E603"),sQuery(id+"F0.wireOp",EDGE,"E604"),sQuery(id+"F0.wireOp",EDGE,"E605"),sQuery(id+"F0.wireOp",EDGE,"E606"),sQuery(id+"F0.wireOp",EDGE,"E607"),sQuery(id+"F0.wireOp",EDGE,"E608"),sQuery(id+"F0.wireOp",EDGE,"E609"),sQuery(id+"F0.wireOp",EDGE,"E610"),sQuery(id+"F0.wireOp",EDGE,"E611"),sQuery(id+"F0.wireOp",EDGE,"E612"),sQuery(id+"F0.wireOp",EDGE,"E613"),sQuery(id+"F0.wireOp",EDGE,"E614"),sQuery(id+"F0.wireOp",EDGE,"E615"),sQuery(id+"F0.wireOp",EDGE,"E616"),sQuery(id+"F0.wireOp",EDGE,"E617"),sQuery(id+"F0.wireOp",EDGE,"E618"),sQuery(id+"F0.wireOp",EDGE,"E619"),sQuery(id+"F0.wireOp",EDGE,"E620"),sQuery(id+"F0.wireOp",EDGE,"E621"),sQuery(id+"F0.wireOp",EDGE,"E622"),sQuery(id+"F0.wireOp",EDGE,"E623"),sQuery(id+"F0.wireOp",EDGE,"E624"),sQuery(id+"F0.wireOp",EDGE,"E625"),sQuery(id+"F0.wireOp",EDGE,"E626"),sQuery(id+"F0.wireOp",EDGE,"E627"),sQuery(id+"F0.wireOp",EDGE,"E628"),sQuery(id+"F0.wireOp",EDGE,"E629"),sQuery(id+"F0.wireOp",EDGE,"E630"),sQuery(id+"F0.wireOp",EDGE,"E631"),sQuery(id+"F0.wireOp",EDGE,"E632"),sQuery(id+"F0.wireOp",EDGE,"E633"),sQuery(id+"F0.wireOp",EDGE,"E634"),sQuery(id+"F0.wireOp",EDGE,"E635")])]});
            hole(context, id + "F8", {"style" : HoleStyle.SIMPLE, "endStyle" : HoleEndStyle.THROUGH, "holeDiameter" : 3 * mm, "tappedDepth" : 12 * mm, "tapClearance" : 3, "locations" : qUnion([Q0]), "scope" : qUnion([Q1])});
        }
        {
            var Q0;
            Q0=sQuery(id+"F7.wireOp",VERTEX,"E636.end");
            var Q1;
            Q1=makeQuery(id+"F1.opExtrude","SWEPT_BODY",BODY,{"disambiguationData":[OSD([sQuery(id+"F0.wireOp",EDGE,"E244"),sQuery(id+"F0.wireOp",EDGE,"E245"),sQuery(id+"F0.wireOp",EDGE,"E246"),sQuery(id+"F0.wireOp",EDGE,"E247"),sQuery(id+"F0.wireOp",EDGE,"E248"),sQuery(id+"F0.wireOp",EDGE,"E249"),sQuery(id+"F0.wireOp",EDGE,"E250"),sQuery(id+"F0.wireOp",EDGE,"E251"),sQuery(id+"F0.wireOp",EDGE,"E252"),sQuery(id+"F0.wireOp",EDGE,"E253"),sQuery(id+"F0.wireOp",EDGE,"E254"),sQuery(id+"F0.wireOp",EDGE,"E255"),sQuery(id+"F0.wireOp",EDGE,"E256"),sQuery(id+"F0.wireOp",EDGE,"E257"),sQuery(id+"F0.wireOp",EDGE,"E258"),sQuery(id+"F0.wireOp",EDGE,"E259"),sQuery(id+"F0.wireOp",EDGE,"E260"),sQuery(id+"F0.wireOp",EDGE,"E261"),sQuery(id+"F0.wireOp",EDGE,"E262"),sQuery(id+"F0.wireOp",EDGE,"E263"),sQuery(id+"F0.wireOp",EDGE,"E264"),sQuery(id+"F0.wireOp",EDGE,"E265"),sQuery(id+"F0.wireOp",EDGE,"E266"),sQuery(id+"F0.wireOp",EDGE,"E267"),sQuery(id+"F0.wireOp",EDGE,"E268"),sQuery(id+"F0.wireOp",EDGE,"E269"),sQuery(id+"F0.wireOp",EDGE,"E270"),sQuery(id+"F0.wireOp",EDGE,"E271"),sQuery(id+"F0.wireOp",EDGE,"E272"),sQuery(id+"F0.wireOp",EDGE,"E273"),sQuery(id+"F0.wireOp",EDGE,"E274"),sQuery(id+"F0.wireOp",EDGE,"E275"),sQuery(id+"F0.wireOp",EDGE,"E276"),sQuery(id+"F0.wireOp",EDGE,"E277"),sQuery(id+"F0.wireOp",EDGE,"E278"),sQuery(id+"F0.wireOp",EDGE,"E279"),sQuery(id+"F0.wireOp",EDGE,"E280"),sQuery(id+"F0.wireOp",EDGE,"E281"),sQuery(id+"F0.wireOp",EDGE,"E282"),sQuery(id+"F0.wireOp",EDGE,"E283"),sQuery(id+"F0.wireOp",EDGE,"E284"),sQuery(id+"F0.wireOp",EDGE,"E285"),sQuery(id+"F0.wireOp",EDGE,"E286"),sQuery(id+"F0.wireOp",EDGE,"E287"),sQuery(id+"F0.wireOp",EDGE,"E288"),sQuery(id+"F0.wireOp",EDGE,"E289"),sQuery(id+"F0.wireOp",EDGE,"E290"),sQuery(id+"F0.wireOp",EDGE,"E291"),sQuery(id+"F0.wireOp",EDGE,"E292"),sQuery(id+"F0.wireOp",EDGE,"E293"),sQuery(id+"F0.wireOp",EDGE,"E294"),sQuery(id+"F0.wireOp",EDGE,"E295"),sQuery(id+"F0.wireOp",EDGE,"E296"),sQuery(id+"F0.wireOp",EDGE,"E297"),sQuery(id+"F0.wireOp",EDGE,"E298"),sQuery(id+"F0.wireOp",EDGE,"E299"),sQuery(id+"F0.wireOp",EDGE,"E300"),sQuery(id+"F0.wireOp",EDGE,"E301"),sQuery(id+"F0.wireOp",EDGE,"E302"),sQuery(id+"F0.wireOp",EDGE,"E303"),sQuery(id+"F0.wireOp",EDGE,"E304"),sQuery(id+"F0.wireOp",EDGE,"E305"),sQuery(id+"F0.wireOp",EDGE,"E306"),sQuery(id+"F0.wireOp",EDGE,"E307"),sQuery(id+"F0.wireOp",EDGE,"E308"),sQuery(id+"F0.wireOp",EDGE,"E309"),sQuery(id+"F0.wireOp",EDGE,"E310"),sQuery(id+"F0.wireOp",EDGE,"E311"),sQuery(id+"F0.wireOp",EDGE,"E312"),sQuery(id+"F0.wireOp",EDGE,"E313"),sQuery(id+"F0.wireOp",EDGE,"E314"),sQuery(id+"F0.wireOp",EDGE,"E315"),sQuery(id+"F0.wireOp",EDGE,"E316"),sQuery(id+"F0.wireOp",EDGE,"E317"),sQuery(id+"F0.wireOp",EDGE,"E318"),sQuery(id+"F0.wireOp",EDGE,"E319"),sQuery(id+"F0.wireOp",EDGE,"E320"),sQuery(id+"F0.wireOp",EDGE,"E321"),sQuery(id+"F0.wireOp",EDGE,"E322"),sQuery(id+"F0.wireOp",EDGE,"E323"),sQuery(id+"F0.wireOp",EDGE,"E324"),sQuery(id+"F0.wireOp",EDGE,"E325"),sQuery(id+"F0.wireOp",EDGE,"E326"),sQuery(id+"F0.wireOp",EDGE,"E327"),sQuery(id+"F0.wireOp",EDGE,"E328"),sQuery(id+"F0.wireOp",EDGE,"E329"),sQuery(id+"F0.wireOp",EDGE,"E330"),sQuery(id+"F0.wireOp",EDGE,"E331"),sQuery(id+"F0.wireOp",EDGE,"E332"),sQuery(id+"F0.wireOp",EDGE,"E333"),sQuery(id+"F0.wireOp",EDGE,"E334"),sQuery(id+"F0.wireOp",EDGE,"E335"),sQuery(id+"F0.wireOp",EDGE,"E336"),sQuery(id+"F0.wireOp",EDGE,"E337"),sQuery(id+"F0.wireOp",EDGE,"E338"),sQuery(id+"F0.wireOp",EDGE,"E339"),sQuery(id+"F0.wireOp",EDGE,"E340"),sQuery(id+"F0.wireOp",EDGE,"E341"),sQuery(id+"F0.wireOp",EDGE,"E342"),sQuery(id+"F0.wireOp",EDGE,"E343"),sQuery(id+"F0.wireOp",EDGE,"E344"),sQuery(id+"F0.wireOp",EDGE,"E345"),sQuery(id+"F0.wireOp",EDGE,"E346"),sQuery(id+"F0.wireOp",EDGE,"E347"),sQuery(id+"F0.wireOp",EDGE,"E348"),sQuery(id+"F0.wireOp",EDGE,"E349"),sQuery(id+"F0.wireOp",EDGE,"E350"),sQuery(id+"F0.wireOp",EDGE,"E351"),sQuery(id+"F0.wireOp",EDGE,"E352"),sQuery(id+"F0.wireOp",EDGE,"E353"),sQuery(id+"F0.wireOp",EDGE,"E354"),sQuery(id+"F0.wireOp",EDGE,"E355"),sQuery(id+"F0.wireOp",EDGE,"E356"),sQuery(id+"F0.wireOp",EDGE,"E357"),sQuery(id+"F0.wireOp",EDGE,"E358"),sQuery(id+"F0.wireOp",EDGE,"E359"),sQuery(id+"F0.wireOp",EDGE,"E360"),sQuery(id+"F0.wireOp",EDGE,"E361"),sQuery(id+"F0.wireOp",EDGE,"E362"),sQuery(id+"F0.wireOp",EDGE,"E363"),sQuery(id+"F0.wireOp",EDGE,"E364"),sQuery(id+"F0.wireOp",EDGE,"E365"),sQuery(id+"F0.wireOp",EDGE,"E366"),sQuery(id+"F0.wireOp",EDGE,"E367"),sQuery(id+"F0.wireOp",EDGE,"E368"),sQuery(id+"F0.wireOp",EDGE,"E369"),sQuery(id+"F0.wireOp",EDGE,"E370"),sQuery(id+"F0.wireOp",EDGE,"E371"),sQuery(id+"F0.wireOp",EDGE,"E372"),sQuery(id+"F0.wireOp",EDGE,"E373"),sQuery(id+"F0.wireOp",EDGE,"E374"),sQuery(id+"F0.wireOp",EDGE,"E375"),sQuery(id+"F0.wireOp",EDGE,"E376"),sQuery(id+"F0.wireOp",EDGE,"E377"),sQuery(id+"F0.wireOp",EDGE,"E378"),sQuery(id+"F0.wireOp",EDGE,"E379"),sQuery(id+"F0.wireOp",EDGE,"E380"),sQuery(id+"F0.wireOp",EDGE,"E381"),sQuery(id+"F0.wireOp",EDGE,"E382"),sQuery(id+"F0.wireOp",EDGE,"E383"),sQuery(id+"F0.wireOp",EDGE,"E384"),sQuery(id+"F0.wireOp",EDGE,"E385"),sQuery(id+"F0.wireOp",EDGE,"E386"),sQuery(id+"F0.wireOp",EDGE,"E387"),sQuery(id+"F0.wireOp",EDGE,"E388"),sQuery(id+"F0.wireOp",EDGE,"E389"),sQuery(id+"F0.wireOp",EDGE,"E390"),sQuery(id+"F0.wireOp",EDGE,"E391"),sQuery(id+"F0.wireOp",EDGE,"E392"),sQuery(id+"F0.wireOp",EDGE,"E393"),sQuery(id+"F0.wireOp",EDGE,"E394"),sQuery(id+"F0.wireOp",EDGE,"E395"),sQuery(id+"F0.wireOp",EDGE,"E396"),sQuery(id+"F0.wireOp",EDGE,"E397"),sQuery(id+"F0.wireOp",EDGE,"E398"),sQuery(id+"F0.wireOp",EDGE,"E399"),sQuery(id+"F0.wireOp",EDGE,"E400"),sQuery(id+"F0.wireOp",EDGE,"E401"),sQuery(id+"F0.wireOp",EDGE,"E402"),sQuery(id+"F0.wireOp",EDGE,"E403"),sQuery(id+"F0.wireOp",EDGE,"E404"),sQuery(id+"F0.wireOp",EDGE,"E405"),sQuery(id+"F0.wireOp",EDGE,"E406"),sQuery(id+"F0.wireOp",EDGE,"E407"),sQuery(id+"F0.wireOp",EDGE,"E408"),sQuery(id+"F0.wireOp",EDGE,"E409"),sQuery(id+"F0.wireOp",EDGE,"E410"),sQuery(id+"F0.wireOp",EDGE,"E411"),sQuery(id+"F0.wireOp",EDGE,"E412"),sQuery(id+"F0.wireOp",EDGE,"E413"),sQuery(id+"F0.wireOp",EDGE,"E414"),sQuery(id+"F0.wireOp",EDGE,"E415"),sQuery(id+"F0.wireOp",EDGE,"E416"),sQuery(id+"F0.wireOp",EDGE,"E417"),sQuery(id+"F0.wireOp",EDGE,"E418"),sQuery(id+"F0.wireOp",EDGE,"E419"),sQuery(id+"F0.wireOp",EDGE,"E420"),sQuery(id+"F0.wireOp",EDGE,"E421"),sQuery(id+"F0.wireOp",EDGE,"E422"),sQuery(id+"F0.wireOp",EDGE,"E423"),sQuery(id+"F0.wireOp",EDGE,"E424"),sQuery(id+"F0.wireOp",EDGE,"E425"),sQuery(id+"F0.wireOp",EDGE,"E426"),sQuery(id+"F0.wireOp",EDGE,"E427"),sQuery(id+"F0.wireOp",EDGE,"E428"),sQuery(id+"F0.wireOp",EDGE,"E429"),sQuery(id+"F0.wireOp",EDGE,"E430"),sQuery(id+"F0.wireOp",EDGE,"E431"),sQuery(id+"F0.wireOp",EDGE,"E432"),sQuery(id+"F0.wireOp",EDGE,"E433"),sQuery(id+"F0.wireOp",EDGE,"E434"),sQuery(id+"F0.wireOp",EDGE,"E435"),sQuery(id+"F0.wireOp",EDGE,"E436"),sQuery(id+"F0.wireOp",EDGE,"E437"),sQuery(id+"F0.wireOp",EDGE,"E438"),sQuery(id+"F0.wireOp",EDGE,"E439"),sQuery(id+"F0.wireOp",EDGE,"E440"),sQuery(id+"F0.wireOp",EDGE,"E441"),sQuery(id+"F0.wireOp",EDGE,"E442"),sQuery(id+"F0.wireOp",EDGE,"E443"),sQuery(id+"F0.wireOp",EDGE,"E444"),sQuery(id+"F0.wireOp",EDGE,"E445"),sQuery(id+"F0.wireOp",EDGE,"E446"),sQuery(id+"F0.wireOp",EDGE,"E447"),sQuery(id+"F0.wireOp",EDGE,"E448"),sQuery(id+"F0.wireOp",EDGE,"E449"),sQuery(id+"F0.wireOp",EDGE,"E450"),sQuery(id+"F0.wireOp",EDGE,"E451"),sQuery(id+"F0.wireOp",EDGE,"E452"),sQuery(id+"F0.wireOp",EDGE,"E453"),sQuery(id+"F0.wireOp",EDGE,"E454"),sQuery(id+"F0.wireOp",EDGE,"E455"),sQuery(id+"F0.wireOp",EDGE,"E456"),sQuery(id+"F0.wireOp",EDGE,"E457"),sQuery(id+"F0.wireOp",EDGE,"E458"),sQuery(id+"F0.wireOp",EDGE,"E459"),sQuery(id+"F0.wireOp",EDGE,"E460"),sQuery(id+"F0.wireOp",EDGE,"E461"),sQuery(id+"F0.wireOp",EDGE,"E462"),sQuery(id+"F0.wireOp",EDGE,"E463"),sQuery(id+"F0.wireOp",EDGE,"E464"),sQuery(id+"F0.wireOp",EDGE,"E465"),sQuery(id+"F0.wireOp",EDGE,"E466"),sQuery(id+"F0.wireOp",EDGE,"E467"),sQuery(id+"F0.wireOp",EDGE,"E468"),sQuery(id+"F0.wireOp",EDGE,"E469"),sQuery(id+"F0.wireOp",EDGE,"E470"),sQuery(id+"F0.wireOp",EDGE,"E471"),sQuery(id+"F0.wireOp",EDGE,"E472"),sQuery(id+"F0.wireOp",EDGE,"E473"),sQuery(id+"F0.wireOp",EDGE,"E474"),sQuery(id+"F0.wireOp",EDGE,"E475"),sQuery(id+"F0.wireOp",EDGE,"E476"),sQuery(id+"F0.wireOp",EDGE,"E477"),sQuery(id+"F0.wireOp",EDGE,"E478"),sQuery(id+"F0.wireOp",EDGE,"E479"),sQuery(id+"F0.wireOp",EDGE,"E480"),sQuery(id+"F0.wireOp",EDGE,"E481"),sQuery(id+"F0.wireOp",EDGE,"E482"),sQuery(id+"F0.wireOp",EDGE,"E483"),sQuery(id+"F0.wireOp",EDGE,"E484"),sQuery(id+"F0.wireOp",EDGE,"E485"),sQuery(id+"F0.wireOp",EDGE,"E486"),sQuery(id+"F0.wireOp",EDGE,"E487"),sQuery(id+"F0.wireOp",EDGE,"E488"),sQuery(id+"F0.wireOp",EDGE,"E489"),sQuery(id+"F0.wireOp",EDGE,"E490"),sQuery(id+"F0.wireOp",EDGE,"E491"),sQuery(id+"F0.wireOp",EDGE,"E492"),sQuery(id+"F0.wireOp",EDGE,"E493"),sQuery(id+"F0.wireOp",EDGE,"E494"),sQuery(id+"F0.wireOp",EDGE,"E495"),sQuery(id+"F0.wireOp",EDGE,"E496"),sQuery(id+"F0.wireOp",EDGE,"E497"),sQuery(id+"F0.wireOp",EDGE,"E498"),sQuery(id+"F0.wireOp",EDGE,"E499"),sQuery(id+"F0.wireOp",EDGE,"E500"),sQuery(id+"F0.wireOp",EDGE,"E501"),sQuery(id+"F0.wireOp",EDGE,"E502"),sQuery(id+"F0.wireOp",EDGE,"E503"),sQuery(id+"F0.wireOp",EDGE,"E504"),sQuery(id+"F0.wireOp",EDGE,"E505"),sQuery(id+"F0.wireOp",EDGE,"E506"),sQuery(id+"F0.wireOp",EDGE,"E507"),sQuery(id+"F0.wireOp",EDGE,"E508"),sQuery(id+"F0.wireOp",EDGE,"E509"),sQuery(id+"F0.wireOp",EDGE,"E510"),sQuery(id+"F0.wireOp",EDGE,"E511"),sQuery(id+"F0.wireOp",EDGE,"E512"),sQuery(id+"F0.wireOp",EDGE,"E513"),sQuery(id+"F0.wireOp",EDGE,"E514"),sQuery(id+"F0.wireOp",EDGE,"E515"),sQuery(id+"F0.wireOp",EDGE,"E516"),sQuery(id+"F0.wireOp",EDGE,"E517"),sQuery(id+"F0.wireOp",EDGE,"E518"),sQuery(id+"F0.wireOp",EDGE,"E519"),sQuery(id+"F0.wireOp",EDGE,"E520"),sQuery(id+"F0.wireOp",EDGE,"E521"),sQuery(id+"F0.wireOp",EDGE,"E522"),sQuery(id+"F0.wireOp",EDGE,"E523"),sQuery(id+"F0.wireOp",EDGE,"E524"),sQuery(id+"F0.wireOp",EDGE,"E525"),sQuery(id+"F0.wireOp",EDGE,"E526"),sQuery(id+"F0.wireOp",EDGE,"E527"),sQuery(id+"F0.wireOp",EDGE,"E528"),sQuery(id+"F0.wireOp",EDGE,"E529"),sQuery(id+"F0.wireOp",EDGE,"E530"),sQuery(id+"F0.wireOp",EDGE,"E531"),sQuery(id+"F0.wireOp",EDGE,"E532"),sQuery(id+"F0.wireOp",EDGE,"E533"),sQuery(id+"F0.wireOp",EDGE,"E534"),sQuery(id+"F0.wireOp",EDGE,"E535"),sQuery(id+"F0.wireOp",EDGE,"E536"),sQuery(id+"F0.wireOp",EDGE,"E537"),sQuery(id+"F0.wireOp",EDGE,"E538"),sQuery(id+"F0.wireOp",EDGE,"E539"),sQuery(id+"F0.wireOp",EDGE,"E540"),sQuery(id+"F0.wireOp",EDGE,"E541"),sQuery(id+"F0.wireOp",EDGE,"E542"),sQuery(id+"F0.wireOp",EDGE,"E543"),sQuery(id+"F0.wireOp",EDGE,"E544"),sQuery(id+"F0.wireOp",EDGE,"E545"),sQuery(id+"F0.wireOp",EDGE,"E546"),sQuery(id+"F0.wireOp",EDGE,"E547"),sQuery(id+"F0.wireOp",EDGE,"E548"),sQuery(id+"F0.wireOp",EDGE,"E549"),sQuery(id+"F0.wireOp",EDGE,"E550"),sQuery(id+"F0.wireOp",EDGE,"E551"),sQuery(id+"F0.wireOp",EDGE,"E552"),sQuery(id+"F0.wireOp",EDGE,"E553"),sQuery(id+"F0.wireOp",EDGE,"E554"),sQuery(id+"F0.wireOp",EDGE,"E555"),sQuery(id+"F0.wireOp",EDGE,"E556"),sQuery(id+"F0.wireOp",EDGE,"E557"),sQuery(id+"F0.wireOp",EDGE,"E558"),sQuery(id+"F0.wireOp",EDGE,"E559"),sQuery(id+"F0.wireOp",EDGE,"E560"),sQuery(id+"F0.wireOp",EDGE,"E561"),sQuery(id+"F0.wireOp",EDGE,"E562"),sQuery(id+"F0.wireOp",EDGE,"E563"),sQuery(id+"F0.wireOp",EDGE,"E564"),sQuery(id+"F0.wireOp",EDGE,"E565"),sQuery(id+"F0.wireOp",EDGE,"E566"),sQuery(id+"F0.wireOp",EDGE,"E567"),sQuery(id+"F0.wireOp",EDGE,"E568"),sQuery(id+"F0.wireOp",EDGE,"E569"),sQuery(id+"F0.wireOp",EDGE,"E570"),sQuery(id+"F0.wireOp",EDGE,"E571"),sQuery(id+"F0.wireOp",EDGE,"E572"),sQuery(id+"F0.wireOp",EDGE,"E573"),sQuery(id+"F0.wireOp",EDGE,"E574"),sQuery(id+"F0.wireOp",EDGE,"E575"),sQuery(id+"F0.wireOp",EDGE,"E576"),sQuery(id+"F0.wireOp",EDGE,"E577"),sQuery(id+"F0.wireOp",EDGE,"E578"),sQuery(id+"F0.wireOp",EDGE,"E579"),sQuery(id+"F0.wireOp",EDGE,"E580"),sQuery(id+"F0.wireOp",EDGE,"E581"),sQuery(id+"F0.wireOp",EDGE,"E582"),sQuery(id+"F0.wireOp",EDGE,"E583"),sQuery(id+"F0.wireOp",EDGE,"E584"),sQuery(id+"F0.wireOp",EDGE,"E585"),sQuery(id+"F0.wireOp",EDGE,"E586"),sQuery(id+"F0.wireOp",EDGE,"E587"),sQuery(id+"F0.wireOp",EDGE,"E588"),sQuery(id+"F0.wireOp",EDGE,"E589"),sQuery(id+"F0.wireOp",EDGE,"E590"),sQuery(id+"F0.wireOp",EDGE,"E591"),sQuery(id+"F0.wireOp",EDGE,"E592"),sQuery(id+"F0.wireOp",EDGE,"E593"),sQuery(id+"F0.wireOp",EDGE,"E594"),sQuery(id+"F0.wireOp",EDGE,"E595"),sQuery(id+"F0.wireOp",EDGE,"E596"),sQuery(id+"F0.wireOp",EDGE,"E597"),sQuery(id+"F0.wireOp",EDGE,"E598"),sQuery(id+"F0.wireOp",EDGE,"E599"),sQuery(id+"F0.wireOp",EDGE,"E600"),sQuery(id+"F0.wireOp",EDGE,"E601"),sQuery(id+"F0.wireOp",EDGE,"E602"),sQuery(id+"F0.wireOp",EDGE,"E603"),sQuery(id+"F0.wireOp",EDGE,"E604"),sQuery(id+"F0.wireOp",EDGE,"E605"),sQuery(id+"F0.wireOp",EDGE,"E606"),sQuery(id+"F0.wireOp",EDGE,"E607"),sQuery(id+"F0.wireOp",EDGE,"E608"),sQuery(id+"F0.wireOp",EDGE,"E609"),sQuery(id+"F0.wireOp",EDGE,"E610"),sQuery(id+"F0.wireOp",EDGE,"E611"),sQuery(id+"F0.wireOp",EDGE,"E612"),sQuery(id+"F0.wireOp",EDGE,"E613"),sQuery(id+"F0.wireOp",EDGE,"E614"),sQuery(id+"F0.wireOp",EDGE,"E615"),sQuery(id+"F0.wireOp",EDGE,"E616"),sQuery(id+"F0.wireOp",EDGE,"E617"),sQuery(id+"F0.wireOp",EDGE,"E618"),sQuery(id+"F0.wireOp",EDGE,"E619"),sQuery(id+"F0.wireOp",EDGE,"E620"),sQuery(id+"F0.wireOp",EDGE,"E621"),sQuery(id+"F0.wireOp",EDGE,"E622"),sQuery(id+"F0.wireOp",EDGE,"E623"),sQuery(id+"F0.wireOp",EDGE,"E624"),sQuery(id+"F0.wireOp",EDGE,"E625"),sQuery(id+"F0.wireOp",EDGE,"E626"),sQuery(id+"F0.wireOp",EDGE,"E627"),sQuery(id+"F0.wireOp",EDGE,"E628"),sQuery(id+"F0.wireOp",EDGE,"E629"),sQuery(id+"F0.wireOp",EDGE,"E630"),sQuery(id+"F0.wireOp",EDGE,"E631"),sQuery(id+"F0.wireOp",EDGE,"E632"),sQuery(id+"F0.wireOp",EDGE,"E633"),sQuery(id+"F0.wireOp",EDGE,"E634"),sQuery(id+"F0.wireOp",EDGE,"E635")])]});
            hole(context, id + "F9", {"style" : HoleStyle.SIMPLE, "endStyle" : HoleEndStyle.THROUGH, "oppositeDirection" : true, "holeDiameter" : 3 * mm, "tappedDepth" : 12 * mm, "tapClearance" : 3, "locations" : qUnion([Q0]), "scope" : qUnion([Q1])});
        }
        {
            var Q0;
            Q0=qCreatedBy(makeId("Top.planeOp"),FACE);
            var sketch = newSketch(context, id + "F10", { "sketchPlane" : qUnion([Q0])});
            skCircle(sketch, "E637", {"center": v(0, 0) * mm, "radius": 1.9 * mm});
            skSolve(sketch);
        }
        {
            var Q0;
            Q0=sQuery(id+"F10.wireOp",VERTEX,"E637.center");
            var Q1;
            Q1=makeQuery(id+"F1.opExtrude","SWEPT_BODY",BODY,{"disambiguationData":[OSD([sQuery(id+"F0.wireOp",EDGE,"E244"),sQuery(id+"F0.wireOp",EDGE,"E245"),sQuery(id+"F0.wireOp",EDGE,"E246"),sQuery(id+"F0.wireOp",EDGE,"E247"),sQuery(id+"F0.wireOp",EDGE,"E248"),sQuery(id+"F0.wireOp",EDGE,"E249"),sQuery(id+"F0.wireOp",EDGE,"E250"),sQuery(id+"F0.wireOp",EDGE,"E251"),sQuery(id+"F0.wireOp",EDGE,"E252"),sQuery(id+"F0.wireOp",EDGE,"E253"),sQuery(id+"F0.wireOp",EDGE,"E254"),sQuery(id+"F0.wireOp",EDGE,"E255"),sQuery(id+"F0.wireOp",EDGE,"E256"),sQuery(id+"F0.wireOp",EDGE,"E257"),sQuery(id+"F0.wireOp",EDGE,"E258"),sQuery(id+"F0.wireOp",EDGE,"E259"),sQuery(id+"F0.wireOp",EDGE,"E260"),sQuery(id+"F0.wireOp",EDGE,"E261"),sQuery(id+"F0.wireOp",EDGE,"E262"),sQuery(id+"F0.wireOp",EDGE,"E263"),sQuery(id+"F0.wireOp",EDGE,"E264"),sQuery(id+"F0.wireOp",EDGE,"E265"),sQuery(id+"F0.wireOp",EDGE,"E266"),sQuery(id+"F0.wireOp",EDGE,"E267"),sQuery(id+"F0.wireOp",EDGE,"E268"),sQuery(id+"F0.wireOp",EDGE,"E269"),sQuery(id+"F0.wireOp",EDGE,"E270"),sQuery(id+"F0.wireOp",EDGE,"E271"),sQuery(id+"F0.wireOp",EDGE,"E272"),sQuery(id+"F0.wireOp",EDGE,"E273"),sQuery(id+"F0.wireOp",EDGE,"E274"),sQuery(id+"F0.wireOp",EDGE,"E275"),sQuery(id+"F0.wireOp",EDGE,"E276"),sQuery(id+"F0.wireOp",EDGE,"E277"),sQuery(id+"F0.wireOp",EDGE,"E278"),sQuery(id+"F0.wireOp",EDGE,"E279"),sQuery(id+"F0.wireOp",EDGE,"E280"),sQuery(id+"F0.wireOp",EDGE,"E281"),sQuery(id+"F0.wireOp",EDGE,"E282"),sQuery(id+"F0.wireOp",EDGE,"E283"),sQuery(id+"F0.wireOp",EDGE,"E284"),sQuery(id+"F0.wireOp",EDGE,"E285"),sQuery(id+"F0.wireOp",EDGE,"E286"),sQuery(id+"F0.wireOp",EDGE,"E287"),sQuery(id+"F0.wireOp",EDGE,"E288"),sQuery(id+"F0.wireOp",EDGE,"E289"),sQuery(id+"F0.wireOp",EDGE,"E290"),sQuery(id+"F0.wireOp",EDGE,"E291"),sQuery(id+"F0.wireOp",EDGE,"E292"),sQuery(id+"F0.wireOp",EDGE,"E293"),sQuery(id+"F0.wireOp",EDGE,"E294"),sQuery(id+"F0.wireOp",EDGE,"E295"),sQuery(id+"F0.wireOp",EDGE,"E296"),sQuery(id+"F0.wireOp",EDGE,"E297"),sQuery(id+"F0.wireOp",EDGE,"E298"),sQuery(id+"F0.wireOp",EDGE,"E299"),sQuery(id+"F0.wireOp",EDGE,"E300"),sQuery(id+"F0.wireOp",EDGE,"E301"),sQuery(id+"F0.wireOp",EDGE,"E302"),sQuery(id+"F0.wireOp",EDGE,"E303"),sQuery(id+"F0.wireOp",EDGE,"E304"),sQuery(id+"F0.wireOp",EDGE,"E305"),sQuery(id+"F0.wireOp",EDGE,"E306"),sQuery(id+"F0.wireOp",EDGE,"E307"),sQuery(id+"F0.wireOp",EDGE,"E308"),sQuery(id+"F0.wireOp",EDGE,"E309"),sQuery(id+"F0.wireOp",EDGE,"E310"),sQuery(id+"F0.wireOp",EDGE,"E311"),sQuery(id+"F0.wireOp",EDGE,"E312"),sQuery(id+"F0.wireOp",EDGE,"E313"),sQuery(id+"F0.wireOp",EDGE,"E314"),sQuery(id+"F0.wireOp",EDGE,"E315"),sQuery(id+"F0.wireOp",EDGE,"E316"),sQuery(id+"F0.wireOp",EDGE,"E317"),sQuery(id+"F0.wireOp",EDGE,"E318"),sQuery(id+"F0.wireOp",EDGE,"E319"),sQuery(id+"F0.wireOp",EDGE,"E320"),sQuery(id+"F0.wireOp",EDGE,"E321"),sQuery(id+"F0.wireOp",EDGE,"E322"),sQuery(id+"F0.wireOp",EDGE,"E323"),sQuery(id+"F0.wireOp",EDGE,"E324"),sQuery(id+"F0.wireOp",EDGE,"E325"),sQuery(id+"F0.wireOp",EDGE,"E326"),sQuery(id+"F0.wireOp",EDGE,"E327"),sQuery(id+"F0.wireOp",EDGE,"E328"),sQuery(id+"F0.wireOp",EDGE,"E329"),sQuery(id+"F0.wireOp",EDGE,"E330"),sQuery(id+"F0.wireOp",EDGE,"E331"),sQuery(id+"F0.wireOp",EDGE,"E332"),sQuery(id+"F0.wireOp",EDGE,"E333"),sQuery(id+"F0.wireOp",EDGE,"E334"),sQuery(id+"F0.wireOp",EDGE,"E335"),sQuery(id+"F0.wireOp",EDGE,"E336"),sQuery(id+"F0.wireOp",EDGE,"E337"),sQuery(id+"F0.wireOp",EDGE,"E338"),sQuery(id+"F0.wireOp",EDGE,"E339"),sQuery(id+"F0.wireOp",EDGE,"E340"),sQuery(id+"F0.wireOp",EDGE,"E341"),sQuery(id+"F0.wireOp",EDGE,"E342"),sQuery(id+"F0.wireOp",EDGE,"E343"),sQuery(id+"F0.wireOp",EDGE,"E344"),sQuery(id+"F0.wireOp",EDGE,"E345"),sQuery(id+"F0.wireOp",EDGE,"E346"),sQuery(id+"F0.wireOp",EDGE,"E347"),sQuery(id+"F0.wireOp",EDGE,"E348"),sQuery(id+"F0.wireOp",EDGE,"E349"),sQuery(id+"F0.wireOp",EDGE,"E350"),sQuery(id+"F0.wireOp",EDGE,"E351"),sQuery(id+"F0.wireOp",EDGE,"E352"),sQuery(id+"F0.wireOp",EDGE,"E353"),sQuery(id+"F0.wireOp",EDGE,"E354"),sQuery(id+"F0.wireOp",EDGE,"E355"),sQuery(id+"F0.wireOp",EDGE,"E356"),sQuery(id+"F0.wireOp",EDGE,"E357"),sQuery(id+"F0.wireOp",EDGE,"E358"),sQuery(id+"F0.wireOp",EDGE,"E359"),sQuery(id+"F0.wireOp",EDGE,"E360"),sQuery(id+"F0.wireOp",EDGE,"E361"),sQuery(id+"F0.wireOp",EDGE,"E362"),sQuery(id+"F0.wireOp",EDGE,"E363"),sQuery(id+"F0.wireOp",EDGE,"E364"),sQuery(id+"F0.wireOp",EDGE,"E365"),sQuery(id+"F0.wireOp",EDGE,"E366"),sQuery(id+"F0.wireOp",EDGE,"E367"),sQuery(id+"F0.wireOp",EDGE,"E368"),sQuery(id+"F0.wireOp",EDGE,"E369"),sQuery(id+"F0.wireOp",EDGE,"E370"),sQuery(id+"F0.wireOp",EDGE,"E371"),sQuery(id+"F0.wireOp",EDGE,"E372"),sQuery(id+"F0.wireOp",EDGE,"E373"),sQuery(id+"F0.wireOp",EDGE,"E374"),sQuery(id+"F0.wireOp",EDGE,"E375"),sQuery(id+"F0.wireOp",EDGE,"E376"),sQuery(id+"F0.wireOp",EDGE,"E377"),sQuery(id+"F0.wireOp",EDGE,"E378"),sQuery(id+"F0.wireOp",EDGE,"E379"),sQuery(id+"F0.wireOp",EDGE,"E380"),sQuery(id+"F0.wireOp",EDGE,"E381"),sQuery(id+"F0.wireOp",EDGE,"E382"),sQuery(id+"F0.wireOp",EDGE,"E383"),sQuery(id+"F0.wireOp",EDGE,"E384"),sQuery(id+"F0.wireOp",EDGE,"E385"),sQuery(id+"F0.wireOp",EDGE,"E386"),sQuery(id+"F0.wireOp",EDGE,"E387"),sQuery(id+"F0.wireOp",EDGE,"E388"),sQuery(id+"F0.wireOp",EDGE,"E389"),sQuery(id+"F0.wireOp",EDGE,"E390"),sQuery(id+"F0.wireOp",EDGE,"E391"),sQuery(id+"F0.wireOp",EDGE,"E392"),sQuery(id+"F0.wireOp",EDGE,"E393"),sQuery(id+"F0.wireOp",EDGE,"E394"),sQuery(id+"F0.wireOp",EDGE,"E395"),sQuery(id+"F0.wireOp",EDGE,"E396"),sQuery(id+"F0.wireOp",EDGE,"E397"),sQuery(id+"F0.wireOp",EDGE,"E398"),sQuery(id+"F0.wireOp",EDGE,"E399"),sQuery(id+"F0.wireOp",EDGE,"E400"),sQuery(id+"F0.wireOp",EDGE,"E401"),sQuery(id+"F0.wireOp",EDGE,"E402"),sQuery(id+"F0.wireOp",EDGE,"E403"),sQuery(id+"F0.wireOp",EDGE,"E404"),sQuery(id+"F0.wireOp",EDGE,"E405"),sQuery(id+"F0.wireOp",EDGE,"E406"),sQuery(id+"F0.wireOp",EDGE,"E407"),sQuery(id+"F0.wireOp",EDGE,"E408"),sQuery(id+"F0.wireOp",EDGE,"E409"),sQuery(id+"F0.wireOp",EDGE,"E410"),sQuery(id+"F0.wireOp",EDGE,"E411"),sQuery(id+"F0.wireOp",EDGE,"E412"),sQuery(id+"F0.wireOp",EDGE,"E413"),sQuery(id+"F0.wireOp",EDGE,"E414"),sQuery(id+"F0.wireOp",EDGE,"E415"),sQuery(id+"F0.wireOp",EDGE,"E416"),sQuery(id+"F0.wireOp",EDGE,"E417"),sQuery(id+"F0.wireOp",EDGE,"E418"),sQuery(id+"F0.wireOp",EDGE,"E419"),sQuery(id+"F0.wireOp",EDGE,"E420"),sQuery(id+"F0.wireOp",EDGE,"E421"),sQuery(id+"F0.wireOp",EDGE,"E422"),sQuery(id+"F0.wireOp",EDGE,"E423"),sQuery(id+"F0.wireOp",EDGE,"E424"),sQuery(id+"F0.wireOp",EDGE,"E425"),sQuery(id+"F0.wireOp",EDGE,"E426"),sQuery(id+"F0.wireOp",EDGE,"E427"),sQuery(id+"F0.wireOp",EDGE,"E428"),sQuery(id+"F0.wireOp",EDGE,"E429"),sQuery(id+"F0.wireOp",EDGE,"E430"),sQuery(id+"F0.wireOp",EDGE,"E431"),sQuery(id+"F0.wireOp",EDGE,"E432"),sQuery(id+"F0.wireOp",EDGE,"E433"),sQuery(id+"F0.wireOp",EDGE,"E434"),sQuery(id+"F0.wireOp",EDGE,"E435"),sQuery(id+"F0.wireOp",EDGE,"E436"),sQuery(id+"F0.wireOp",EDGE,"E437"),sQuery(id+"F0.wireOp",EDGE,"E438"),sQuery(id+"F0.wireOp",EDGE,"E439"),sQuery(id+"F0.wireOp",EDGE,"E440"),sQuery(id+"F0.wireOp",EDGE,"E441"),sQuery(id+"F0.wireOp",EDGE,"E442"),sQuery(id+"F0.wireOp",EDGE,"E443"),sQuery(id+"F0.wireOp",EDGE,"E444"),sQuery(id+"F0.wireOp",EDGE,"E445"),sQuery(id+"F0.wireOp",EDGE,"E446"),sQuery(id+"F0.wireOp",EDGE,"E447"),sQuery(id+"F0.wireOp",EDGE,"E448"),sQuery(id+"F0.wireOp",EDGE,"E449"),sQuery(id+"F0.wireOp",EDGE,"E450"),sQuery(id+"F0.wireOp",EDGE,"E451"),sQuery(id+"F0.wireOp",EDGE,"E452"),sQuery(id+"F0.wireOp",EDGE,"E453"),sQuery(id+"F0.wireOp",EDGE,"E454"),sQuery(id+"F0.wireOp",EDGE,"E455"),sQuery(id+"F0.wireOp",EDGE,"E456"),sQuery(id+"F0.wireOp",EDGE,"E457"),sQuery(id+"F0.wireOp",EDGE,"E458"),sQuery(id+"F0.wireOp",EDGE,"E459"),sQuery(id+"F0.wireOp",EDGE,"E460"),sQuery(id+"F0.wireOp",EDGE,"E461"),sQuery(id+"F0.wireOp",EDGE,"E462"),sQuery(id+"F0.wireOp",EDGE,"E463"),sQuery(id+"F0.wireOp",EDGE,"E464"),sQuery(id+"F0.wireOp",EDGE,"E465"),sQuery(id+"F0.wireOp",EDGE,"E466"),sQuery(id+"F0.wireOp",EDGE,"E467"),sQuery(id+"F0.wireOp",EDGE,"E468"),sQuery(id+"F0.wireOp",EDGE,"E469"),sQuery(id+"F0.wireOp",EDGE,"E470"),sQuery(id+"F0.wireOp",EDGE,"E471"),sQuery(id+"F0.wireOp",EDGE,"E472"),sQuery(id+"F0.wireOp",EDGE,"E473"),sQuery(id+"F0.wireOp",EDGE,"E474"),sQuery(id+"F0.wireOp",EDGE,"E475"),sQuery(id+"F0.wireOp",EDGE,"E476"),sQuery(id+"F0.wireOp",EDGE,"E477"),sQuery(id+"F0.wireOp",EDGE,"E478"),sQuery(id+"F0.wireOp",EDGE,"E479"),sQuery(id+"F0.wireOp",EDGE,"E480"),sQuery(id+"F0.wireOp",EDGE,"E481"),sQuery(id+"F0.wireOp",EDGE,"E482"),sQuery(id+"F0.wireOp",EDGE,"E483"),sQuery(id+"F0.wireOp",EDGE,"E484"),sQuery(id+"F0.wireOp",EDGE,"E485"),sQuery(id+"F0.wireOp",EDGE,"E486"),sQuery(id+"F0.wireOp",EDGE,"E487"),sQuery(id+"F0.wireOp",EDGE,"E488"),sQuery(id+"F0.wireOp",EDGE,"E489"),sQuery(id+"F0.wireOp",EDGE,"E490"),sQuery(id+"F0.wireOp",EDGE,"E491"),sQuery(id+"F0.wireOp",EDGE,"E492"),sQuery(id+"F0.wireOp",EDGE,"E493"),sQuery(id+"F0.wireOp",EDGE,"E494"),sQuery(id+"F0.wireOp",EDGE,"E495"),sQuery(id+"F0.wireOp",EDGE,"E496"),sQuery(id+"F0.wireOp",EDGE,"E497"),sQuery(id+"F0.wireOp",EDGE,"E498"),sQuery(id+"F0.wireOp",EDGE,"E499"),sQuery(id+"F0.wireOp",EDGE,"E500"),sQuery(id+"F0.wireOp",EDGE,"E501"),sQuery(id+"F0.wireOp",EDGE,"E502"),sQuery(id+"F0.wireOp",EDGE,"E503"),sQuery(id+"F0.wireOp",EDGE,"E504"),sQuery(id+"F0.wireOp",EDGE,"E505"),sQuery(id+"F0.wireOp",EDGE,"E506"),sQuery(id+"F0.wireOp",EDGE,"E507"),sQuery(id+"F0.wireOp",EDGE,"E508"),sQuery(id+"F0.wireOp",EDGE,"E509"),sQuery(id+"F0.wireOp",EDGE,"E510"),sQuery(id+"F0.wireOp",EDGE,"E511"),sQuery(id+"F0.wireOp",EDGE,"E512"),sQuery(id+"F0.wireOp",EDGE,"E513"),sQuery(id+"F0.wireOp",EDGE,"E514"),sQuery(id+"F0.wireOp",EDGE,"E515"),sQuery(id+"F0.wireOp",EDGE,"E516"),sQuery(id+"F0.wireOp",EDGE,"E517"),sQuery(id+"F0.wireOp",EDGE,"E518"),sQuery(id+"F0.wireOp",EDGE,"E519"),sQuery(id+"F0.wireOp",EDGE,"E520"),sQuery(id+"F0.wireOp",EDGE,"E521"),sQuery(id+"F0.wireOp",EDGE,"E522"),sQuery(id+"F0.wireOp",EDGE,"E523"),sQuery(id+"F0.wireOp",EDGE,"E524"),sQuery(id+"F0.wireOp",EDGE,"E525"),sQuery(id+"F0.wireOp",EDGE,"E526"),sQuery(id+"F0.wireOp",EDGE,"E527"),sQuery(id+"F0.wireOp",EDGE,"E528"),sQuery(id+"F0.wireOp",EDGE,"E529"),sQuery(id+"F0.wireOp",EDGE,"E530"),sQuery(id+"F0.wireOp",EDGE,"E531"),sQuery(id+"F0.wireOp",EDGE,"E532"),sQuery(id+"F0.wireOp",EDGE,"E533"),sQuery(id+"F0.wireOp",EDGE,"E534"),sQuery(id+"F0.wireOp",EDGE,"E535"),sQuery(id+"F0.wireOp",EDGE,"E536"),sQuery(id+"F0.wireOp",EDGE,"E537"),sQuery(id+"F0.wireOp",EDGE,"E538"),sQuery(id+"F0.wireOp",EDGE,"E539"),sQuery(id+"F0.wireOp",EDGE,"E540"),sQuery(id+"F0.wireOp",EDGE,"E541"),sQuery(id+"F0.wireOp",EDGE,"E542"),sQuery(id+"F0.wireOp",EDGE,"E543"),sQuery(id+"F0.wireOp",EDGE,"E544"),sQuery(id+"F0.wireOp",EDGE,"E545"),sQuery(id+"F0.wireOp",EDGE,"E546"),sQuery(id+"F0.wireOp",EDGE,"E547"),sQuery(id+"F0.wireOp",EDGE,"E548"),sQuery(id+"F0.wireOp",EDGE,"E549"),sQuery(id+"F0.wireOp",EDGE,"E550"),sQuery(id+"F0.wireOp",EDGE,"E551"),sQuery(id+"F0.wireOp",EDGE,"E552"),sQuery(id+"F0.wireOp",EDGE,"E553"),sQuery(id+"F0.wireOp",EDGE,"E554"),sQuery(id+"F0.wireOp",EDGE,"E555"),sQuery(id+"F0.wireOp",EDGE,"E556"),sQuery(id+"F0.wireOp",EDGE,"E557"),sQuery(id+"F0.wireOp",EDGE,"E558"),sQuery(id+"F0.wireOp",EDGE,"E559"),sQuery(id+"F0.wireOp",EDGE,"E560"),sQuery(id+"F0.wireOp",EDGE,"E561"),sQuery(id+"F0.wireOp",EDGE,"E562"),sQuery(id+"F0.wireOp",EDGE,"E563"),sQuery(id+"F0.wireOp",EDGE,"E564"),sQuery(id+"F0.wireOp",EDGE,"E565"),sQuery(id+"F0.wireOp",EDGE,"E566"),sQuery(id+"F0.wireOp",EDGE,"E567"),sQuery(id+"F0.wireOp",EDGE,"E568"),sQuery(id+"F0.wireOp",EDGE,"E569"),sQuery(id+"F0.wireOp",EDGE,"E570"),sQuery(id+"F0.wireOp",EDGE,"E571"),sQuery(id+"F0.wireOp",EDGE,"E572"),sQuery(id+"F0.wireOp",EDGE,"E573"),sQuery(id+"F0.wireOp",EDGE,"E574"),sQuery(id+"F0.wireOp",EDGE,"E575"),sQuery(id+"F0.wireOp",EDGE,"E576"),sQuery(id+"F0.wireOp",EDGE,"E577"),sQuery(id+"F0.wireOp",EDGE,"E578"),sQuery(id+"F0.wireOp",EDGE,"E579"),sQuery(id+"F0.wireOp",EDGE,"E580"),sQuery(id+"F0.wireOp",EDGE,"E581"),sQuery(id+"F0.wireOp",EDGE,"E582"),sQuery(id+"F0.wireOp",EDGE,"E583"),sQuery(id+"F0.wireOp",EDGE,"E584"),sQuery(id+"F0.wireOp",EDGE,"E585"),sQuery(id+"F0.wireOp",EDGE,"E586"),sQuery(id+"F0.wireOp",EDGE,"E587"),sQuery(id+"F0.wireOp",EDGE,"E588"),sQuery(id+"F0.wireOp",EDGE,"E589"),sQuery(id+"F0.wireOp",EDGE,"E590"),sQuery(id+"F0.wireOp",EDGE,"E591"),sQuery(id+"F0.wireOp",EDGE,"E592"),sQuery(id+"F0.wireOp",EDGE,"E593"),sQuery(id+"F0.wireOp",EDGE,"E594"),sQuery(id+"F0.wireOp",EDGE,"E595"),sQuery(id+"F0.wireOp",EDGE,"E596"),sQuery(id+"F0.wireOp",EDGE,"E597"),sQuery(id+"F0.wireOp",EDGE,"E598"),sQuery(id+"F0.wireOp",EDGE,"E599"),sQuery(id+"F0.wireOp",EDGE,"E600"),sQuery(id+"F0.wireOp",EDGE,"E601"),sQuery(id+"F0.wireOp",EDGE,"E602"),sQuery(id+"F0.wireOp",EDGE,"E603"),sQuery(id+"F0.wireOp",EDGE,"E604"),sQuery(id+"F0.wireOp",EDGE,"E605"),sQuery(id+"F0.wireOp",EDGE,"E606"),sQuery(id+"F0.wireOp",EDGE,"E607"),sQuery(id+"F0.wireOp",EDGE,"E608"),sQuery(id+"F0.wireOp",EDGE,"E609"),sQuery(id+"F0.wireOp",EDGE,"E610"),sQuery(id+"F0.wireOp",EDGE,"E611"),sQuery(id+"F0.wireOp",EDGE,"E612"),sQuery(id+"F0.wireOp",EDGE,"E613"),sQuery(id+"F0.wireOp",EDGE,"E614"),sQuery(id+"F0.wireOp",EDGE,"E615"),sQuery(id+"F0.wireOp",EDGE,"E616"),sQuery(id+"F0.wireOp",EDGE,"E617"),sQuery(id+"F0.wireOp",EDGE,"E618"),sQuery(id+"F0.wireOp",EDGE,"E619"),sQuery(id+"F0.wireOp",EDGE,"E620"),sQuery(id+"F0.wireOp",EDGE,"E621"),sQuery(id+"F0.wireOp",EDGE,"E622"),sQuery(id+"F0.wireOp",EDGE,"E623"),sQuery(id+"F0.wireOp",EDGE,"E624"),sQuery(id+"F0.wireOp",EDGE,"E625"),sQuery(id+"F0.wireOp",EDGE,"E626"),sQuery(id+"F0.wireOp",EDGE,"E627"),sQuery(id+"F0.wireOp",EDGE,"E628"),sQuery(id+"F0.wireOp",EDGE,"E629"),sQuery(id+"F0.wireOp",EDGE,"E630"),sQuery(id+"F0.wireOp",EDGE,"E631"),sQuery(id+"F0.wireOp",EDGE,"E632"),sQuery(id+"F0.wireOp",EDGE,"E633"),sQuery(id+"F0.wireOp",EDGE,"E634"),sQuery(id+"F0.wireOp",EDGE,"E635")])]});
            hole(context, id + "F11", {"style" : HoleStyle.SIMPLE, "endStyle" : HoleEndStyle.BLIND, "oppositeDirection" : true, "holeDiameter" : 6.32 * mm, "holeDepth" : 10 * mm, "tappedDepth" : 12 * mm, "tapClearance" : 3, "locations" : qUnion([Q0]), "scope" : qUnion([Q1])});
        }
    });
